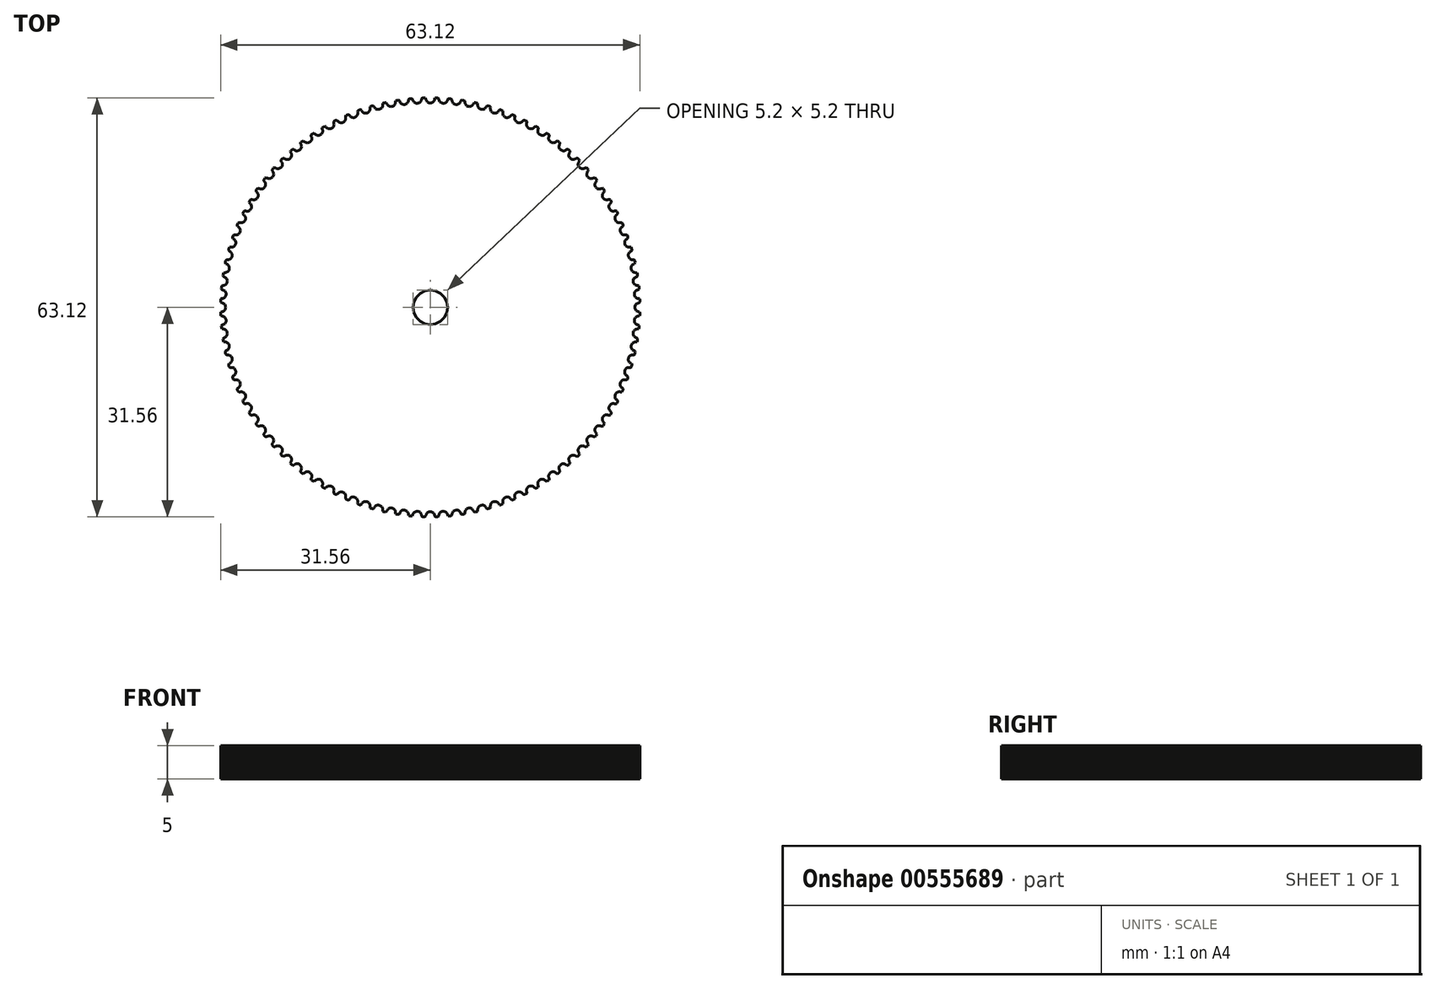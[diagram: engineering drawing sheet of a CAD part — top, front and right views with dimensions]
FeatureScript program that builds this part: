
annotation { "Feature Type Name" : "Feature", "Feature Type Description" : "" }
export const myFeature = defineFeature(function(context is Context, id is Id, definition is map)
    precondition{}
    {
        {
            assignVariable(context, id + "F0", {"name" : "thMat", "anyValue" : 5 * mm});
        }
        {
            var Q0;
            Q0=qCreatedBy(makeId("Top.planeOp"),FACE);
            var sketch = newSketch(context, id + "F1", { "sketchPlane" : qUnion([Q0])});
            skLineSegment(sketch, "E0", {"start": v(1, -31.56) * mm, "end": v(1.14, -31.56) * mm});
            skLineSegment(sketch, "E1", {"start": v(1.14, -31.56) * mm, "end": v(1.25, -31.51) * mm});
            skLineSegment(sketch, "E2", {"start": v(1.25, -31.51) * mm, "end": v(1.3, -31.42) * mm});
            skLineSegment(sketch, "E3", {"start": v(1.3, -31.42) * mm, "end": v(1.31, -31.3) * mm});
            skLineSegment(sketch, "E4", {"start": v(1.31, -31.3) * mm, "end": v(1.34, -31.2) * mm});
            skLineSegment(sketch, "E5", {"start": v(1.34, -31.2) * mm, "end": v(1.38, -31.1) * mm});
            skLineSegment(sketch, "E6", {"start": v(1.38, -31.1) * mm, "end": v(1.44, -31) * mm});
            skLineSegment(sketch, "E7", {"start": v(1.44, -31) * mm, "end": v(1.54, -30.9) * mm});
            skLineSegment(sketch, "E8", {"start": v(1.54, -30.9) * mm, "end": v(1.66, -30.82) * mm});
            skLineSegment(sketch, "E9", {"start": v(1.66, -30.82) * mm, "end": v(1.8, -30.76) * mm});
            skLineSegment(sketch, "E10", {"start": v(1.8, -30.76) * mm, "end": v(1.93, -30.74) * mm});
            skLineSegment(sketch, "E11", {"start": v(1.93, -30.74) * mm, "end": v(2.08, -30.75) * mm});
            skLineSegment(sketch, "E12", {"start": v(2.08, -30.75) * mm, "end": v(2.22, -30.78) * mm});
            skLineSegment(sketch, "E13", {"start": v(2.22, -30.78) * mm, "end": v(2.35, -30.84) * mm});
            skLineSegment(sketch, "E14", {"start": v(2.35, -30.84) * mm, "end": v(2.46, -30.93) * mm});
            skLineSegment(sketch, "E15", {"start": v(2.46, -30.93) * mm, "end": v(2.53, -31.02) * mm});
            skLineSegment(sketch, "E16", {"start": v(2.53, -31.02) * mm, "end": v(2.58, -31.12) * mm});
            skLineSegment(sketch, "E17", {"start": v(2.58, -31.12) * mm, "end": v(2.62, -31.22) * mm});
            skLineSegment(sketch, "E18", {"start": v(2.62, -31.22) * mm, "end": v(2.65, -31.33) * mm});
            skLineSegment(sketch, "E19", {"start": v(2.65, -31.33) * mm, "end": v(2.71, -31.42) * mm});
            skLineSegment(sketch, "E20", {"start": v(2.71, -31.42) * mm, "end": v(2.83, -31.45) * mm});
            skLineSegment(sketch, "E21", {"start": v(2.83, -31.45) * mm, "end": v(2.97, -31.44) * mm});
            skLineSegment(sketch, "E22", {"start": v(2.97, -31.44) * mm, "end": v(3.12, -31.42) * mm});
            skLineSegment(sketch, "E23", {"start": v(3.12, -31.42) * mm, "end": v(3.22, -31.37) * mm});
            skLineSegment(sketch, "E24", {"start": v(3.22, -31.37) * mm, "end": v(3.27, -31.27) * mm});
            skLineSegment(sketch, "E25", {"start": v(3.27, -31.27) * mm, "end": v(3.28, -31.16) * mm});
            skLineSegment(sketch, "E26", {"start": v(3.28, -31.16) * mm, "end": v(3.3, -31.05) * mm});
            skLineSegment(sketch, "E27", {"start": v(3.3, -31.05) * mm, "end": v(3.33, -30.95) * mm});
            skLineSegment(sketch, "E28", {"start": v(3.33, -30.95) * mm, "end": v(3.38, -30.85) * mm});
            skLineSegment(sketch, "E29", {"start": v(3.38, -30.85) * mm, "end": v(3.47, -30.74) * mm});
            skLineSegment(sketch, "E30", {"start": v(3.47, -30.74) * mm, "end": v(3.59, -30.65) * mm});
            skLineSegment(sketch, "E31", {"start": v(3.59, -30.65) * mm, "end": v(3.72, -30.6) * mm});
            skLineSegment(sketch, "E32", {"start": v(3.72, -30.6) * mm, "end": v(3.86, -30.56) * mm});
            skLineSegment(sketch, "E33", {"start": v(3.86, -30.56) * mm, "end": v(4, -30.55) * mm});
            skLineSegment(sketch, "E34", {"start": v(4, -30.55) * mm, "end": v(4.15, -30.58) * mm});
            skLineSegment(sketch, "E35", {"start": v(4.15, -30.58) * mm, "end": v(4.28, -30.63) * mm});
            skLineSegment(sketch, "E36", {"start": v(4.28, -30.63) * mm, "end": v(4.4, -30.72) * mm});
            skLineSegment(sketch, "E37", {"start": v(4.4, -30.72) * mm, "end": v(4.47, -30.8) * mm});
            skLineSegment(sketch, "E38", {"start": v(4.47, -30.8) * mm, "end": v(4.53, -30.9) * mm});
            skLineSegment(sketch, "E39", {"start": v(4.53, -30.9) * mm, "end": v(4.58, -31) * mm});
            skLineSegment(sketch, "E40", {"start": v(4.58, -31) * mm, "end": v(4.61, -31.1) * mm});
            skLineSegment(sketch, "E41", {"start": v(4.61, -31.1) * mm, "end": v(4.68, -31.19) * mm});
            skLineSegment(sketch, "E42", {"start": v(4.68, -31.19) * mm, "end": v(4.8, -31.21) * mm});
            skLineSegment(sketch, "E43", {"start": v(4.8, -31.21) * mm, "end": v(4.94, -31.19) * mm});
            skLineSegment(sketch, "E44", {"start": v(4.94, -31.19) * mm, "end": v(5.08, -31.16) * mm});
            skLineSegment(sketch, "E45", {"start": v(5.08, -31.16) * mm, "end": v(5.19, -31.1) * mm});
            skLineSegment(sketch, "E46", {"start": v(5.19, -31.1) * mm, "end": v(5.22, -31) * mm});
            skLineSegment(sketch, "E47", {"start": v(5.22, -31) * mm, "end": v(5.23, -30.9) * mm});
            skLineSegment(sketch, "E48", {"start": v(5.23, -30.9) * mm, "end": v(5.24, -30.79) * mm});
            skLineSegment(sketch, "E49", {"start": v(5.24, -30.79) * mm, "end": v(5.27, -30.68) * mm});
            skLineSegment(sketch, "E50", {"start": v(5.27, -30.68) * mm, "end": v(5.31, -30.57) * mm});
            skLineSegment(sketch, "E51", {"start": v(5.31, -30.57) * mm, "end": v(5.4, -30.46) * mm});
            skLineSegment(sketch, "E52", {"start": v(5.4, -30.46) * mm, "end": v(5.5, -30.36) * mm});
            skLineSegment(sketch, "E53", {"start": v(5.5, -30.36) * mm, "end": v(5.63, -30.3) * mm});
            skLineSegment(sketch, "E54", {"start": v(5.63, -30.3) * mm, "end": v(5.77, -30.26) * mm});
            skLineSegment(sketch, "E55", {"start": v(5.77, -30.26) * mm, "end": v(5.92, -30.24) * mm});
            skLineSegment(sketch, "E56", {"start": v(5.92, -30.24) * mm, "end": v(6.06, -30.26) * mm});
            skLineSegment(sketch, "E57", {"start": v(6.06, -30.26) * mm, "end": v(6.2, -30.3) * mm});
            skLineSegment(sketch, "E58", {"start": v(6.2, -30.3) * mm, "end": v(6.32, -30.38) * mm});
            skLineSegment(sketch, "E59", {"start": v(6.32, -30.38) * mm, "end": v(6.4, -30.46) * mm});
            skLineSegment(sketch, "E60", {"start": v(6.4, -30.46) * mm, "end": v(6.46, -30.55) * mm});
            skLineSegment(sketch, "E61", {"start": v(6.46, -30.55) * mm, "end": v(6.51, -30.65) * mm});
            skLineSegment(sketch, "E62", {"start": v(6.51, -30.65) * mm, "end": v(6.56, -30.75) * mm});
            skLineSegment(sketch, "E63", {"start": v(6.56, -30.75) * mm, "end": v(6.63, -30.83) * mm});
            skLineSegment(sketch, "E64", {"start": v(6.63, -30.83) * mm, "end": v(6.74, -30.85) * mm});
            skLineSegment(sketch, "E65", {"start": v(6.74, -30.85) * mm, "end": v(6.89, -30.82) * mm});
            skLineSegment(sketch, "E66", {"start": v(6.89, -30.82) * mm, "end": v(7.03, -30.78) * mm});
            skLineSegment(sketch, "E67", {"start": v(7.03, -30.78) * mm, "end": v(7.13, -30.72) * mm});
            skLineSegment(sketch, "E68", {"start": v(7.13, -30.72) * mm, "end": v(7.16, -30.62) * mm});
            skLineSegment(sketch, "E69", {"start": v(7.16, -30.62) * mm, "end": v(7.16, -30.5) * mm});
            skLineSegment(sketch, "E70", {"start": v(7.16, -30.5) * mm, "end": v(7.16, -30.4) * mm});
            skLineSegment(sketch, "E71", {"start": v(7.16, -30.4) * mm, "end": v(7.19, -30.29) * mm});
            skLineSegment(sketch, "E72", {"start": v(7.19, -30.29) * mm, "end": v(7.22, -30.18) * mm});
            skLineSegment(sketch, "E73", {"start": v(7.22, -30.18) * mm, "end": v(7.3, -30.06) * mm});
            skLineSegment(sketch, "E74", {"start": v(7.3, -30.06) * mm, "end": v(7.4, -29.96) * mm});
            skLineSegment(sketch, "E75", {"start": v(7.4, -29.96) * mm, "end": v(7.52, -29.88) * mm});
            skLineSegment(sketch, "E76", {"start": v(7.52, -29.88) * mm, "end": v(7.66, -29.83) * mm});
            skLineSegment(sketch, "E77", {"start": v(7.66, -29.83) * mm, "end": v(7.8, -29.81) * mm});
            skLineSegment(sketch, "E78", {"start": v(7.8, -29.81) * mm, "end": v(7.95, -29.82) * mm});
            skLineSegment(sketch, "E79", {"start": v(7.95, -29.82) * mm, "end": v(8.09, -29.86) * mm});
            skLineSegment(sketch, "E80", {"start": v(8.09, -29.86) * mm, "end": v(8.21, -29.92) * mm});
            skLineSegment(sketch, "E81", {"start": v(8.21, -29.92) * mm, "end": v(8.3, -30) * mm});
            skLineSegment(sketch, "E82", {"start": v(8.3, -30) * mm, "end": v(8.37, -30.09) * mm});
            skLineSegment(sketch, "E83", {"start": v(8.37, -30.09) * mm, "end": v(8.43, -30.18) * mm});
            skLineSegment(sketch, "E84", {"start": v(8.43, -30.18) * mm, "end": v(8.47, -30.28) * mm});
            skLineSegment(sketch, "E85", {"start": v(8.47, -30.28) * mm, "end": v(8.55, -30.36) * mm});
            skLineSegment(sketch, "E86", {"start": v(8.55, -30.36) * mm, "end": v(8.67, -30.36) * mm});
            skLineSegment(sketch, "E87", {"start": v(8.67, -30.36) * mm, "end": v(8.8, -30.32) * mm});
            skLineSegment(sketch, "E88", {"start": v(8.8, -30.32) * mm, "end": v(8.95, -30.28) * mm});
            skLineSegment(sketch, "E89", {"start": v(8.95, -30.28) * mm, "end": v(9.04, -30.21) * mm});
            skLineSegment(sketch, "E90", {"start": v(9.04, -30.21) * mm, "end": v(9.07, -30.1) * mm});
            skLineSegment(sketch, "E91", {"start": v(9.07, -30.1) * mm, "end": v(9.06, -30) * mm});
            skLineSegment(sketch, "E92", {"start": v(9.06, -30) * mm, "end": v(9.06, -29.89) * mm});
            skLineSegment(sketch, "E93", {"start": v(9.06, -29.89) * mm, "end": v(9.07, -29.78) * mm});
            skLineSegment(sketch, "E94", {"start": v(9.07, -29.78) * mm, "end": v(9.1, -29.67) * mm});
            skLineSegment(sketch, "E95", {"start": v(9.1, -29.67) * mm, "end": v(9.17, -29.54) * mm});
            skLineSegment(sketch, "E96", {"start": v(9.17, -29.54) * mm, "end": v(9.27, -29.44) * mm});
            skLineSegment(sketch, "E97", {"start": v(9.27, -29.44) * mm, "end": v(9.39, -29.35) * mm});
            skLineSegment(sketch, "E98", {"start": v(9.39, -29.35) * mm, "end": v(9.52, -29.3) * mm});
            skLineSegment(sketch, "E99", {"start": v(9.52, -29.3) * mm, "end": v(9.66, -29.26) * mm});
            skLineSegment(sketch, "E100", {"start": v(9.66, -29.26) * mm, "end": v(9.8, -29.26) * mm});
            skLineSegment(sketch, "E101", {"start": v(9.8, -29.26) * mm, "end": v(9.94, -29.29) * mm});
            skLineSegment(sketch, "E102", {"start": v(9.94, -29.29) * mm, "end": v(10.07, -29.35) * mm});
            skLineSegment(sketch, "E103", {"start": v(10.07, -29.35) * mm, "end": v(10.16, -29.42) * mm});
            skLineSegment(sketch, "E104", {"start": v(10.16, -29.42) * mm, "end": v(10.24, -29.5) * mm});
            skLineSegment(sketch, "E105", {"start": v(10.24, -29.5) * mm, "end": v(10.3, -29.6) * mm});
            skLineSegment(sketch, "E106", {"start": v(10.3, -29.6) * mm, "end": v(10.36, -29.69) * mm});
            skLineSegment(sketch, "E107", {"start": v(10.36, -29.69) * mm, "end": v(10.44, -29.76) * mm});
            skLineSegment(sketch, "E108", {"start": v(10.44, -29.76) * mm, "end": v(10.56, -29.76) * mm});
            skLineSegment(sketch, "E109", {"start": v(10.56, -29.76) * mm, "end": v(10.7, -29.71) * mm});
            skLineSegment(sketch, "E110", {"start": v(10.7, -29.71) * mm, "end": v(10.83, -29.66) * mm});
            skLineSegment(sketch, "E111", {"start": v(10.83, -29.66) * mm, "end": v(10.92, -29.58) * mm});
            skLineSegment(sketch, "E112", {"start": v(10.92, -29.58) * mm, "end": v(10.94, -29.48) * mm});
            skLineSegment(sketch, "E113", {"start": v(10.94, -29.48) * mm, "end": v(10.92, -29.37) * mm});
            skLineSegment(sketch, "E114", {"start": v(10.92, -29.37) * mm, "end": v(10.92, -29.26) * mm});
            skLineSegment(sketch, "E115", {"start": v(10.92, -29.26) * mm, "end": v(10.92, -29.15) * mm});
            skLineSegment(sketch, "E116", {"start": v(10.92, -29.15) * mm, "end": v(10.95, -29.04) * mm});
            skLineSegment(sketch, "E117", {"start": v(10.95, -29.04) * mm, "end": v(11, -28.9) * mm});
            skLineSegment(sketch, "E118", {"start": v(11, -28.9) * mm, "end": v(11.1, -28.8) * mm});
            skLineSegment(sketch, "E119", {"start": v(11.1, -28.8) * mm, "end": v(11.2, -28.7) * mm});
            skLineSegment(sketch, "E120", {"start": v(11.2, -28.7) * mm, "end": v(11.34, -28.64) * mm});
            skLineSegment(sketch, "E121", {"start": v(11.34, -28.64) * mm, "end": v(11.48, -28.6) * mm});
            skLineSegment(sketch, "E122", {"start": v(11.48, -28.6) * mm, "end": v(11.62, -28.59) * mm});
            skLineSegment(sketch, "E123", {"start": v(11.62, -28.59) * mm, "end": v(11.76, -28.6) * mm});
            skLineSegment(sketch, "E124", {"start": v(11.76, -28.6) * mm, "end": v(11.9, -28.66) * mm});
            skLineSegment(sketch, "E125", {"start": v(11.9, -28.66) * mm, "end": v(11.99, -28.73) * mm});
            skLineSegment(sketch, "E126", {"start": v(11.99, -28.73) * mm, "end": v(12.07, -28.8) * mm});
            skLineSegment(sketch, "E127", {"start": v(12.07, -28.8) * mm, "end": v(12.14, -28.89) * mm});
            skLineSegment(sketch, "E128", {"start": v(12.14, -28.89) * mm, "end": v(12.2, -28.98) * mm});
            skLineSegment(sketch, "E129", {"start": v(12.2, -28.98) * mm, "end": v(12.29, -29.04) * mm});
            skLineSegment(sketch, "E130", {"start": v(12.29, -29.04) * mm, "end": v(12.4, -29.04) * mm});
            skLineSegment(sketch, "E131", {"start": v(12.4, -29.04) * mm, "end": v(12.54, -28.98) * mm});
            skLineSegment(sketch, "E132", {"start": v(12.54, -28.98) * mm, "end": v(12.68, -28.92) * mm});
            skLineSegment(sketch, "E133", {"start": v(12.68, -28.92) * mm, "end": v(12.76, -28.84) * mm});
            skLineSegment(sketch, "E134", {"start": v(12.76, -28.84) * mm, "end": v(12.77, -28.73) * mm});
            skLineSegment(sketch, "E135", {"start": v(12.77, -28.73) * mm, "end": v(12.74, -28.62) * mm});
            skLineSegment(sketch, "E136", {"start": v(12.74, -28.62) * mm, "end": v(12.73, -28.52) * mm});
            skLineSegment(sketch, "E137", {"start": v(12.73, -28.52) * mm, "end": v(12.73, -28.4) * mm});
            skLineSegment(sketch, "E138", {"start": v(12.73, -28.4) * mm, "end": v(12.75, -28.3) * mm});
            skLineSegment(sketch, "E139", {"start": v(12.75, -28.3) * mm, "end": v(12.8, -28.16) * mm});
            skLineSegment(sketch, "E140", {"start": v(12.8, -28.16) * mm, "end": v(12.88, -28.04) * mm});
            skLineSegment(sketch, "E141", {"start": v(12.88, -28.04) * mm, "end": v(13, -27.94) * mm});
            skLineSegment(sketch, "E142", {"start": v(13, -27.94) * mm, "end": v(13.11, -27.87) * mm});
            skLineSegment(sketch, "E143", {"start": v(13.11, -27.87) * mm, "end": v(13.25, -27.82) * mm});
            skLineSegment(sketch, "E144", {"start": v(13.25, -27.82) * mm, "end": v(13.4, -27.8) * mm});
            skLineSegment(sketch, "E145", {"start": v(13.4, -27.8) * mm, "end": v(13.54, -27.81) * mm});
            skLineSegment(sketch, "E146", {"start": v(13.54, -27.81) * mm, "end": v(13.67, -27.86) * mm});
            skLineSegment(sketch, "E147", {"start": v(13.67, -27.86) * mm, "end": v(13.77, -27.92) * mm});
            skLineSegment(sketch, "E148", {"start": v(13.77, -27.92) * mm, "end": v(13.86, -27.99) * mm});
            skLineSegment(sketch, "E149", {"start": v(13.86, -27.99) * mm, "end": v(13.93, -28.07) * mm});
            skLineSegment(sketch, "E150", {"start": v(13.93, -28.07) * mm, "end": v(14, -28.15) * mm});
            skLineSegment(sketch, "E151", {"start": v(14, -28.15) * mm, "end": v(14.09, -28.21) * mm});
            skLineSegment(sketch, "E152", {"start": v(14.09, -28.21) * mm, "end": v(14.2, -28.2) * mm});
            skLineSegment(sketch, "E153", {"start": v(14.2, -28.2) * mm, "end": v(14.34, -28.14) * mm});
            skLineSegment(sketch, "E154", {"start": v(14.34, -28.14) * mm, "end": v(14.47, -28.07) * mm});
            skLineSegment(sketch, "E155", {"start": v(14.47, -28.07) * mm, "end": v(14.55, -27.98) * mm});
            skLineSegment(sketch, "E156", {"start": v(14.55, -27.98) * mm, "end": v(14.55, -27.87) * mm});
            skLineSegment(sketch, "E157", {"start": v(14.55, -27.87) * mm, "end": v(14.52, -27.77) * mm});
            skLineSegment(sketch, "E158", {"start": v(14.52, -27.77) * mm, "end": v(14.5, -27.66) * mm});
            skLineSegment(sketch, "E159", {"start": v(14.5, -27.66) * mm, "end": v(14.5, -27.55) * mm});
            skLineSegment(sketch, "E160", {"start": v(14.5, -27.55) * mm, "end": v(14.5, -27.43) * mm});
            skLineSegment(sketch, "E161", {"start": v(14.5, -27.43) * mm, "end": v(14.54, -27.3) * mm});
            skLineSegment(sketch, "E162", {"start": v(14.54, -27.3) * mm, "end": v(14.62, -27.18) * mm});
            skLineSegment(sketch, "E163", {"start": v(14.62, -27.18) * mm, "end": v(14.72, -27.07) * mm});
            skLineSegment(sketch, "E164", {"start": v(14.72, -27.07) * mm, "end": v(14.84, -27) * mm});
            skLineSegment(sketch, "E165", {"start": v(14.84, -27) * mm, "end": v(14.97, -26.93) * mm});
            skLineSegment(sketch, "E166", {"start": v(14.97, -26.93) * mm, "end": v(15.11, -26.9) * mm});
            skLineSegment(sketch, "E167", {"start": v(15.11, -26.9) * mm, "end": v(15.26, -26.9) * mm});
            skLineSegment(sketch, "E168", {"start": v(15.26, -26.9) * mm, "end": v(15.4, -26.94) * mm});
            skLineSegment(sketch, "E169", {"start": v(15.4, -26.94) * mm, "end": v(15.5, -27) * mm});
            skLineSegment(sketch, "E170", {"start": v(15.5, -27) * mm, "end": v(15.59, -27.06) * mm});
            skLineSegment(sketch, "E171", {"start": v(15.59, -27.06) * mm, "end": v(15.67, -27.14) * mm});
            skLineSegment(sketch, "E172", {"start": v(15.67, -27.14) * mm, "end": v(15.74, -27.22) * mm});
            skLineSegment(sketch, "E173", {"start": v(15.74, -27.22) * mm, "end": v(15.83, -27.27) * mm});
            skLineSegment(sketch, "E174", {"start": v(15.83, -27.27) * mm, "end": v(15.95, -27.25) * mm});
            skLineSegment(sketch, "E175", {"start": v(15.95, -27.25) * mm, "end": v(16.07, -27.18) * mm});
            skLineSegment(sketch, "E176", {"start": v(16.07, -27.18) * mm, "end": v(16.2, -27.1) * mm});
            skLineSegment(sketch, "E177", {"start": v(16.2, -27.1) * mm, "end": v(16.27, -27.01) * mm});
            skLineSegment(sketch, "E178", {"start": v(16.27, -27.01) * mm, "end": v(16.27, -26.9) * mm});
            skLineSegment(sketch, "E179", {"start": v(16.27, -26.9) * mm, "end": v(16.23, -26.8) * mm});
            skLineSegment(sketch, "E180", {"start": v(16.23, -26.8) * mm, "end": v(16.2, -26.7) * mm});
            skLineSegment(sketch, "E181", {"start": v(16.2, -26.7) * mm, "end": v(16.2, -26.58) * mm});
            skLineSegment(sketch, "E182", {"start": v(16.2, -26.58) * mm, "end": v(16.2, -26.47) * mm});
            skLineSegment(sketch, "E183", {"start": v(16.2, -26.47) * mm, "end": v(16.23, -26.33) * mm});
            skLineSegment(sketch, "E184", {"start": v(16.23, -26.33) * mm, "end": v(16.3, -26.2) * mm});
            skLineSegment(sketch, "E185", {"start": v(16.3, -26.2) * mm, "end": v(16.4, -26.1) * mm});
            skLineSegment(sketch, "E186", {"start": v(16.4, -26.1) * mm, "end": v(16.5, -26) * mm});
            skLineSegment(sketch, "E187", {"start": v(16.5, -26) * mm, "end": v(16.63, -25.94) * mm});
            skLineSegment(sketch, "E188", {"start": v(16.63, -25.94) * mm, "end": v(16.77, -25.9) * mm});
            skLineSegment(sketch, "E189", {"start": v(16.77, -25.9) * mm, "end": v(16.92, -25.9) * mm});
            skLineSegment(sketch, "E190", {"start": v(16.92, -25.9) * mm, "end": v(17.06, -25.92) * mm});
            skLineSegment(sketch, "E191", {"start": v(17.06, -25.92) * mm, "end": v(17.16, -25.97) * mm});
            skLineSegment(sketch, "E192", {"start": v(17.16, -25.97) * mm, "end": v(17.25, -26.03) * mm});
            skLineSegment(sketch, "E193", {"start": v(17.25, -26.03) * mm, "end": v(17.34, -26.1) * mm});
            skLineSegment(sketch, "E194", {"start": v(17.34, -26.1) * mm, "end": v(17.42, -26.18) * mm});
            skLineSegment(sketch, "E195", {"start": v(17.42, -26.18) * mm, "end": v(17.51, -26.23) * mm});
            skLineSegment(sketch, "E196", {"start": v(17.51, -26.23) * mm, "end": v(17.63, -26.2) * mm});
            skLineSegment(sketch, "E197", {"start": v(17.63, -26.2) * mm, "end": v(17.75, -26.12) * mm});
            skLineSegment(sketch, "E198", {"start": v(17.75, -26.12) * mm, "end": v(17.87, -26.03) * mm});
            skLineSegment(sketch, "E199", {"start": v(17.87, -26.03) * mm, "end": v(17.94, -25.94) * mm});
            skLineSegment(sketch, "E200", {"start": v(17.94, -25.94) * mm, "end": v(17.93, -25.83) * mm});
            skLineSegment(sketch, "E201", {"start": v(17.93, -25.83) * mm, "end": v(17.88, -25.73) * mm});
            skLineSegment(sketch, "E202", {"start": v(17.88, -25.73) * mm, "end": v(17.85, -25.62) * mm});
            skLineSegment(sketch, "E203", {"start": v(17.85, -25.62) * mm, "end": v(17.83, -25.51) * mm});
            skLineSegment(sketch, "E204", {"start": v(17.83, -25.51) * mm, "end": v(17.82, -25.4) * mm});
            skLineSegment(sketch, "E205", {"start": v(17.82, -25.4) * mm, "end": v(17.85, -25.26) * mm});
            skLineSegment(sketch, "E206", {"start": v(17.85, -25.26) * mm, "end": v(17.91, -25.13) * mm});
            skLineSegment(sketch, "E207", {"start": v(17.91, -25.13) * mm, "end": v(18, -25.02) * mm});
            skLineSegment(sketch, "E208", {"start": v(18, -25.02) * mm, "end": v(18.1, -24.92) * mm});
            skLineSegment(sketch, "E209", {"start": v(18.1, -24.92) * mm, "end": v(18.23, -24.85) * mm});
            skLineSegment(sketch, "E210", {"start": v(18.23, -24.85) * mm, "end": v(18.37, -24.8) * mm});
            skLineSegment(sketch, "E211", {"start": v(18.37, -24.8) * mm, "end": v(18.5, -24.78) * mm});
            skLineSegment(sketch, "E212", {"start": v(18.5, -24.78) * mm, "end": v(18.65, -24.8) * mm});
            skLineSegment(sketch, "E213", {"start": v(18.65, -24.8) * mm, "end": v(18.76, -24.84) * mm});
            skLineSegment(sketch, "E214", {"start": v(18.76, -24.84) * mm, "end": v(18.85, -24.9) * mm});
            skLineSegment(sketch, "E215", {"start": v(18.85, -24.9) * mm, "end": v(18.94, -24.96) * mm});
            skLineSegment(sketch, "E216", {"start": v(18.94, -24.96) * mm, "end": v(19.03, -25.03) * mm});
            skLineSegment(sketch, "E217", {"start": v(19.03, -25.03) * mm, "end": v(19.13, -25.08) * mm});
            skLineSegment(sketch, "E218", {"start": v(19.13, -25.08) * mm, "end": v(19.24, -25.04) * mm});
            skLineSegment(sketch, "E219", {"start": v(19.24, -25.04) * mm, "end": v(19.35, -24.95) * mm});
            skLineSegment(sketch, "E220", {"start": v(19.35, -24.95) * mm, "end": v(19.47, -24.86) * mm});
            skLineSegment(sketch, "E221", {"start": v(19.47, -24.86) * mm, "end": v(19.53, -24.76) * mm});
            skLineSegment(sketch, "E222", {"start": v(19.53, -24.76) * mm, "end": v(19.51, -24.65) * mm});
            skLineSegment(sketch, "E223", {"start": v(19.51, -24.65) * mm, "end": v(19.46, -24.56) * mm});
            skLineSegment(sketch, "E224", {"start": v(19.46, -24.56) * mm, "end": v(19.42, -24.45) * mm});
            skLineSegment(sketch, "E225", {"start": v(19.42, -24.45) * mm, "end": v(19.4, -24.34) * mm});
            skLineSegment(sketch, "E226", {"start": v(19.4, -24.34) * mm, "end": v(19.38, -24.23) * mm});
            skLineSegment(sketch, "E227", {"start": v(19.38, -24.23) * mm, "end": v(19.4, -24.09) * mm});
            skLineSegment(sketch, "E228", {"start": v(19.4, -24.09) * mm, "end": v(19.45, -23.96) * mm});
            skLineSegment(sketch, "E229", {"start": v(19.45, -23.96) * mm, "end": v(19.53, -23.84) * mm});
            skLineSegment(sketch, "E230", {"start": v(19.53, -23.84) * mm, "end": v(19.63, -23.73) * mm});
            skLineSegment(sketch, "E231", {"start": v(19.63, -23.73) * mm, "end": v(19.75, -23.65) * mm});
            skLineSegment(sketch, "E232", {"start": v(19.75, -23.65) * mm, "end": v(19.89, -23.6) * mm});
            skLineSegment(sketch, "E233", {"start": v(19.89, -23.6) * mm, "end": v(20.03, -23.57) * mm});
            skLineSegment(sketch, "E234", {"start": v(20.03, -23.57) * mm, "end": v(20.17, -23.58) * mm});
            skLineSegment(sketch, "E235", {"start": v(20.17, -23.58) * mm, "end": v(20.28, -23.62) * mm});
            skLineSegment(sketch, "E236", {"start": v(20.28, -23.62) * mm, "end": v(20.38, -23.66) * mm});
            skLineSegment(sketch, "E237", {"start": v(20.38, -23.66) * mm, "end": v(20.47, -23.72) * mm});
            skLineSegment(sketch, "E238", {"start": v(20.47, -23.72) * mm, "end": v(20.56, -23.79) * mm});
            skLineSegment(sketch, "E239", {"start": v(20.56, -23.79) * mm, "end": v(20.66, -23.82) * mm});
            skLineSegment(sketch, "E240", {"start": v(20.66, -23.82) * mm, "end": v(20.77, -23.78) * mm});
            skLineSegment(sketch, "E241", {"start": v(20.77, -23.78) * mm, "end": v(20.88, -23.69) * mm});
            skLineSegment(sketch, "E242", {"start": v(20.88, -23.69) * mm, "end": v(21, -23.59) * mm});
            skLineSegment(sketch, "E243", {"start": v(21, -23.59) * mm, "end": v(21.05, -23.49) * mm});
            skLineSegment(sketch, "E244", {"start": v(21.05, -23.49) * mm, "end": v(21.02, -23.38) * mm});
            skLineSegment(sketch, "E245", {"start": v(21.02, -23.38) * mm, "end": v(20.97, -23.29) * mm});
            skLineSegment(sketch, "E246", {"start": v(20.97, -23.29) * mm, "end": v(20.92, -23.19) * mm});
            skLineSegment(sketch, "E247", {"start": v(20.92, -23.19) * mm, "end": v(20.89, -23.08) * mm});
            skLineSegment(sketch, "E248", {"start": v(20.89, -23.08) * mm, "end": v(20.87, -22.97) * mm});
            skLineSegment(sketch, "E249", {"start": v(20.87, -22.97) * mm, "end": v(20.88, -22.82) * mm});
            skLineSegment(sketch, "E250", {"start": v(20.88, -22.82) * mm, "end": v(20.92, -22.69) * mm});
            skLineSegment(sketch, "E251", {"start": v(20.92, -22.69) * mm, "end": v(20.99, -22.56) * mm});
            skLineSegment(sketch, "E252", {"start": v(20.99, -22.56) * mm, "end": v(21.08, -22.45) * mm});
            skLineSegment(sketch, "E253", {"start": v(21.08, -22.45) * mm, "end": v(21.2, -22.36) * mm});
            skLineSegment(sketch, "E254", {"start": v(21.2, -22.36) * mm, "end": v(21.33, -22.3) * mm});
            skLineSegment(sketch, "E255", {"start": v(21.33, -22.3) * mm, "end": v(21.47, -22.27) * mm});
            skLineSegment(sketch, "E256", {"start": v(21.47, -22.27) * mm, "end": v(21.61, -22.27) * mm});
            skLineSegment(sketch, "E257", {"start": v(21.61, -22.27) * mm, "end": v(21.72, -22.3) * mm});
            skLineSegment(sketch, "E258", {"start": v(21.72, -22.3) * mm, "end": v(21.83, -22.34) * mm});
            skLineSegment(sketch, "E259", {"start": v(21.83, -22.34) * mm, "end": v(21.92, -22.39) * mm});
            skLineSegment(sketch, "E260", {"start": v(21.92, -22.39) * mm, "end": v(22.01, -22.45) * mm});
            skLineSegment(sketch, "E261", {"start": v(22.01, -22.45) * mm, "end": v(22.12, -22.48) * mm});
            skLineSegment(sketch, "E262", {"start": v(22.12, -22.48) * mm, "end": v(22.22, -22.43) * mm});
            skLineSegment(sketch, "E263", {"start": v(22.22, -22.43) * mm, "end": v(22.33, -22.33) * mm});
            skLineSegment(sketch, "E264", {"start": v(22.33, -22.33) * mm, "end": v(22.43, -22.22) * mm});
            skLineSegment(sketch, "E265", {"start": v(22.43, -22.22) * mm, "end": v(22.48, -22.12) * mm});
            skLineSegment(sketch, "E266", {"start": v(22.48, -22.12) * mm, "end": v(22.45, -22.01) * mm});
            skLineSegment(sketch, "E267", {"start": v(22.45, -22.01) * mm, "end": v(22.39, -21.92) * mm});
            skLineSegment(sketch, "E268", {"start": v(22.39, -21.92) * mm, "end": v(22.34, -21.83) * mm});
            skLineSegment(sketch, "E269", {"start": v(22.34, -21.83) * mm, "end": v(22.3, -21.72) * mm});
            skLineSegment(sketch, "E270", {"start": v(22.3, -21.72) * mm, "end": v(22.27, -21.61) * mm});
            skLineSegment(sketch, "E271", {"start": v(22.27, -21.61) * mm, "end": v(22.27, -21.47) * mm});
            skLineSegment(sketch, "E272", {"start": v(22.27, -21.47) * mm, "end": v(22.3, -21.33) * mm});
            skLineSegment(sketch, "E273", {"start": v(22.3, -21.33) * mm, "end": v(22.36, -21.2) * mm});
            skLineSegment(sketch, "E274", {"start": v(22.36, -21.2) * mm, "end": v(22.45, -21.08) * mm});
            skLineSegment(sketch, "E275", {"start": v(22.45, -21.08) * mm, "end": v(22.56, -20.99) * mm});
            skLineSegment(sketch, "E276", {"start": v(22.56, -20.99) * mm, "end": v(22.69, -20.92) * mm});
            skLineSegment(sketch, "E277", {"start": v(22.69, -20.92) * mm, "end": v(22.82, -20.88) * mm});
            skLineSegment(sketch, "E278", {"start": v(22.82, -20.88) * mm, "end": v(22.97, -20.87) * mm});
            skLineSegment(sketch, "E279", {"start": v(22.97, -20.87) * mm, "end": v(23.08, -20.89) * mm});
            skLineSegment(sketch, "E280", {"start": v(23.08, -20.89) * mm, "end": v(23.19, -20.92) * mm});
            skLineSegment(sketch, "E281", {"start": v(23.19, -20.92) * mm, "end": v(23.29, -20.97) * mm});
            skLineSegment(sketch, "E282", {"start": v(23.29, -20.97) * mm, "end": v(23.38, -21.02) * mm});
            skLineSegment(sketch, "E283", {"start": v(23.38, -21.02) * mm, "end": v(23.49, -21.05) * mm});
            skLineSegment(sketch, "E284", {"start": v(23.49, -21.05) * mm, "end": v(23.59, -21) * mm});
            skLineSegment(sketch, "E285", {"start": v(23.59, -21) * mm, "end": v(23.69, -20.88) * mm});
            skLineSegment(sketch, "E286", {"start": v(23.69, -20.88) * mm, "end": v(23.78, -20.77) * mm});
            skLineSegment(sketch, "E287", {"start": v(23.78, -20.77) * mm, "end": v(23.82, -20.66) * mm});
            skLineSegment(sketch, "E288", {"start": v(23.82, -20.66) * mm, "end": v(23.79, -20.56) * mm});
            skLineSegment(sketch, "E289", {"start": v(23.79, -20.56) * mm, "end": v(23.72, -20.47) * mm});
            skLineSegment(sketch, "E290", {"start": v(23.72, -20.47) * mm, "end": v(23.66, -20.38) * mm});
            skLineSegment(sketch, "E291", {"start": v(23.66, -20.38) * mm, "end": v(23.62, -20.28) * mm});
            skLineSegment(sketch, "E292", {"start": v(23.62, -20.28) * mm, "end": v(23.58, -20.17) * mm});
            skLineSegment(sketch, "E293", {"start": v(23.58, -20.17) * mm, "end": v(23.57, -20.03) * mm});
            skLineSegment(sketch, "E294", {"start": v(23.57, -20.03) * mm, "end": v(23.6, -19.89) * mm});
            skLineSegment(sketch, "E295", {"start": v(23.6, -19.89) * mm, "end": v(23.65, -19.75) * mm});
            skLineSegment(sketch, "E296", {"start": v(23.65, -19.75) * mm, "end": v(23.73, -19.63) * mm});
            skLineSegment(sketch, "E297", {"start": v(23.73, -19.63) * mm, "end": v(23.84, -19.53) * mm});
            skLineSegment(sketch, "E298", {"start": v(23.84, -19.53) * mm, "end": v(23.96, -19.45) * mm});
            skLineSegment(sketch, "E299", {"start": v(23.96, -19.45) * mm, "end": v(24.09, -19.4) * mm});
            skLineSegment(sketch, "E300", {"start": v(24.09, -19.4) * mm, "end": v(24.23, -19.38) * mm});
            skLineSegment(sketch, "E301", {"start": v(24.23, -19.38) * mm, "end": v(24.34, -19.4) * mm});
            skLineSegment(sketch, "E302", {"start": v(24.34, -19.4) * mm, "end": v(24.45, -19.42) * mm});
            skLineSegment(sketch, "E303", {"start": v(24.45, -19.42) * mm, "end": v(24.56, -19.46) * mm});
            skLineSegment(sketch, "E304", {"start": v(24.56, -19.46) * mm, "end": v(24.65, -19.51) * mm});
            skLineSegment(sketch, "E305", {"start": v(24.65, -19.51) * mm, "end": v(24.76, -19.53) * mm});
            skLineSegment(sketch, "E306", {"start": v(24.76, -19.53) * mm, "end": v(24.86, -19.47) * mm});
            skLineSegment(sketch, "E307", {"start": v(24.86, -19.47) * mm, "end": v(24.95, -19.35) * mm});
            skLineSegment(sketch, "E308", {"start": v(24.95, -19.35) * mm, "end": v(25.04, -19.24) * mm});
            skLineSegment(sketch, "E309", {"start": v(25.04, -19.24) * mm, "end": v(25.08, -19.13) * mm});
            skLineSegment(sketch, "E310", {"start": v(25.08, -19.13) * mm, "end": v(25.03, -19.03) * mm});
            skLineSegment(sketch, "E311", {"start": v(25.03, -19.03) * mm, "end": v(24.96, -18.94) * mm});
            skLineSegment(sketch, "E312", {"start": v(24.96, -18.94) * mm, "end": v(24.9, -18.85) * mm});
            skLineSegment(sketch, "E313", {"start": v(24.9, -18.85) * mm, "end": v(24.84, -18.76) * mm});
            skLineSegment(sketch, "E314", {"start": v(24.84, -18.76) * mm, "end": v(24.8, -18.65) * mm});
            skLineSegment(sketch, "E315", {"start": v(24.8, -18.65) * mm, "end": v(24.78, -18.5) * mm});
            skLineSegment(sketch, "E316", {"start": v(24.78, -18.5) * mm, "end": v(24.8, -18.37) * mm});
            skLineSegment(sketch, "E317", {"start": v(24.8, -18.37) * mm, "end": v(24.85, -18.23) * mm});
            skLineSegment(sketch, "E318", {"start": v(24.85, -18.23) * mm, "end": v(24.92, -18.1) * mm});
            skLineSegment(sketch, "E319", {"start": v(24.92, -18.1) * mm, "end": v(25.02, -18) * mm});
            skLineSegment(sketch, "E320", {"start": v(25.02, -18) * mm, "end": v(25.13, -17.91) * mm});
            skLineSegment(sketch, "E321", {"start": v(25.13, -17.91) * mm, "end": v(25.26, -17.85) * mm});
            skLineSegment(sketch, "E322", {"start": v(25.26, -17.85) * mm, "end": v(25.4, -17.82) * mm});
            skLineSegment(sketch, "E323", {"start": v(25.4, -17.82) * mm, "end": v(25.51, -17.83) * mm});
            skLineSegment(sketch, "E324", {"start": v(25.51, -17.83) * mm, "end": v(25.62, -17.85) * mm});
            skLineSegment(sketch, "E325", {"start": v(25.62, -17.85) * mm, "end": v(25.73, -17.88) * mm});
            skLineSegment(sketch, "E326", {"start": v(25.73, -17.88) * mm, "end": v(25.83, -17.93) * mm});
            skLineSegment(sketch, "E327", {"start": v(25.83, -17.93) * mm, "end": v(25.94, -17.94) * mm});
            skLineSegment(sketch, "E328", {"start": v(25.94, -17.94) * mm, "end": v(26.03, -17.87) * mm});
            skLineSegment(sketch, "E329", {"start": v(26.03, -17.87) * mm, "end": v(26.12, -17.75) * mm});
            skLineSegment(sketch, "E330", {"start": v(26.12, -17.75) * mm, "end": v(26.2, -17.63) * mm});
            skLineSegment(sketch, "E331", {"start": v(26.2, -17.63) * mm, "end": v(26.23, -17.51) * mm});
            skLineSegment(sketch, "E332", {"start": v(26.23, -17.51) * mm, "end": v(26.18, -17.42) * mm});
            skLineSegment(sketch, "E333", {"start": v(26.18, -17.42) * mm, "end": v(26.1, -17.34) * mm});
            skLineSegment(sketch, "E334", {"start": v(26.1, -17.34) * mm, "end": v(26.03, -17.25) * mm});
            skLineSegment(sketch, "E335", {"start": v(26.03, -17.25) * mm, "end": v(25.97, -17.16) * mm});
            skLineSegment(sketch, "E336", {"start": v(25.97, -17.16) * mm, "end": v(25.92, -17.06) * mm});
            skLineSegment(sketch, "E337", {"start": v(25.92, -17.06) * mm, "end": v(25.9, -16.92) * mm});
            skLineSegment(sketch, "E338", {"start": v(25.9, -16.92) * mm, "end": v(25.9, -16.77) * mm});
            skLineSegment(sketch, "E339", {"start": v(25.9, -16.77) * mm, "end": v(25.94, -16.63) * mm});
            skLineSegment(sketch, "E340", {"start": v(25.94, -16.63) * mm, "end": v(26, -16.5) * mm});
            skLineSegment(sketch, "E341", {"start": v(26, -16.5) * mm, "end": v(26.1, -16.4) * mm});
            skLineSegment(sketch, "E342", {"start": v(26.1, -16.4) * mm, "end": v(26.2, -16.3) * mm});
            skLineSegment(sketch, "E343", {"start": v(26.2, -16.3) * mm, "end": v(26.33, -16.23) * mm});
            skLineSegment(sketch, "E344", {"start": v(26.33, -16.23) * mm, "end": v(26.47, -16.2) * mm});
            skLineSegment(sketch, "E345", {"start": v(26.47, -16.2) * mm, "end": v(26.58, -16.2) * mm});
            skLineSegment(sketch, "E346", {"start": v(26.58, -16.2) * mm, "end": v(26.7, -16.2) * mm});
            skLineSegment(sketch, "E347", {"start": v(26.7, -16.2) * mm, "end": v(26.8, -16.23) * mm});
            skLineSegment(sketch, "E348", {"start": v(26.8, -16.23) * mm, "end": v(26.9, -16.27) * mm});
            skLineSegment(sketch, "E349", {"start": v(26.9, -16.27) * mm, "end": v(27.01, -16.27) * mm});
            skLineSegment(sketch, "E350", {"start": v(27.01, -16.27) * mm, "end": v(27.1, -16.2) * mm});
            skLineSegment(sketch, "E351", {"start": v(27.1, -16.2) * mm, "end": v(27.18, -16.07) * mm});
            skLineSegment(sketch, "E352", {"start": v(27.18, -16.07) * mm, "end": v(27.25, -15.95) * mm});
            skLineSegment(sketch, "E353", {"start": v(27.25, -15.95) * mm, "end": v(27.27, -15.83) * mm});
            skLineSegment(sketch, "E354", {"start": v(27.27, -15.83) * mm, "end": v(27.22, -15.74) * mm});
            skLineSegment(sketch, "E355", {"start": v(27.22, -15.74) * mm, "end": v(27.14, -15.67) * mm});
            skLineSegment(sketch, "E356", {"start": v(27.14, -15.67) * mm, "end": v(27.06, -15.59) * mm});
            skLineSegment(sketch, "E357", {"start": v(27.06, -15.59) * mm, "end": v(27, -15.5) * mm});
            skLineSegment(sketch, "E358", {"start": v(27, -15.5) * mm, "end": v(26.94, -15.4) * mm});
            skLineSegment(sketch, "E359", {"start": v(26.94, -15.4) * mm, "end": v(26.9, -15.26) * mm});
            skLineSegment(sketch, "E360", {"start": v(26.9, -15.26) * mm, "end": v(26.9, -15.11) * mm});
            skLineSegment(sketch, "E361", {"start": v(26.9, -15.11) * mm, "end": v(26.93, -14.97) * mm});
            skLineSegment(sketch, "E362", {"start": v(26.93, -14.97) * mm, "end": v(27, -14.84) * mm});
            skLineSegment(sketch, "E363", {"start": v(27, -14.84) * mm, "end": v(27.07, -14.72) * mm});
            skLineSegment(sketch, "E364", {"start": v(27.07, -14.72) * mm, "end": v(27.18, -14.62) * mm});
            skLineSegment(sketch, "E365", {"start": v(27.18, -14.62) * mm, "end": v(27.3, -14.54) * mm});
            skLineSegment(sketch, "E366", {"start": v(27.3, -14.54) * mm, "end": v(27.43, -14.5) * mm});
            skLineSegment(sketch, "E367", {"start": v(27.43, -14.5) * mm, "end": v(27.55, -14.5) * mm});
            skLineSegment(sketch, "E368", {"start": v(27.55, -14.5) * mm, "end": v(27.66, -14.5) * mm});
            skLineSegment(sketch, "E369", {"start": v(27.66, -14.5) * mm, "end": v(27.77, -14.52) * mm});
            skLineSegment(sketch, "E370", {"start": v(27.77, -14.52) * mm, "end": v(27.87, -14.55) * mm});
            skLineSegment(sketch, "E371", {"start": v(27.87, -14.55) * mm, "end": v(27.98, -14.55) * mm});
            skLineSegment(sketch, "E372", {"start": v(27.98, -14.55) * mm, "end": v(28.07, -14.47) * mm});
            skLineSegment(sketch, "E373", {"start": v(28.07, -14.47) * mm, "end": v(28.14, -14.34) * mm});
            skLineSegment(sketch, "E374", {"start": v(28.14, -14.34) * mm, "end": v(28.2, -14.2) * mm});
            skLineSegment(sketch, "E375", {"start": v(28.2, -14.2) * mm, "end": v(28.21, -14.09) * mm});
            skLineSegment(sketch, "E376", {"start": v(28.21, -14.09) * mm, "end": v(28.15, -14) * mm});
            skLineSegment(sketch, "E377", {"start": v(28.15, -14) * mm, "end": v(28.07, -13.93) * mm});
            skLineSegment(sketch, "E378", {"start": v(28.07, -13.93) * mm, "end": v(27.99, -13.86) * mm});
            skLineSegment(sketch, "E379", {"start": v(27.99, -13.86) * mm, "end": v(27.92, -13.77) * mm});
            skLineSegment(sketch, "E380", {"start": v(27.92, -13.77) * mm, "end": v(27.86, -13.67) * mm});
            skLineSegment(sketch, "E381", {"start": v(27.86, -13.67) * mm, "end": v(27.81, -13.54) * mm});
            skLineSegment(sketch, "E382", {"start": v(27.81, -13.54) * mm, "end": v(27.8, -13.4) * mm});
            skLineSegment(sketch, "E383", {"start": v(27.8, -13.4) * mm, "end": v(27.82, -13.25) * mm});
            skLineSegment(sketch, "E384", {"start": v(27.82, -13.25) * mm, "end": v(27.87, -13.11) * mm});
            skLineSegment(sketch, "E385", {"start": v(27.87, -13.11) * mm, "end": v(27.94, -13) * mm});
            skLineSegment(sketch, "E386", {"start": v(27.94, -13) * mm, "end": v(28.04, -12.88) * mm});
            skLineSegment(sketch, "E387", {"start": v(28.04, -12.88) * mm, "end": v(28.16, -12.8) * mm});
            skLineSegment(sketch, "E388", {"start": v(28.16, -12.8) * mm, "end": v(28.3, -12.75) * mm});
            skLineSegment(sketch, "E389", {"start": v(28.3, -12.75) * mm, "end": v(28.4, -12.73) * mm});
            skLineSegment(sketch, "E390", {"start": v(28.4, -12.73) * mm, "end": v(28.52, -12.73) * mm});
            skLineSegment(sketch, "E391", {"start": v(28.52, -12.73) * mm, "end": v(28.62, -12.74) * mm});
            skLineSegment(sketch, "E392", {"start": v(28.62, -12.74) * mm, "end": v(28.73, -12.77) * mm});
            skLineSegment(sketch, "E393", {"start": v(28.73, -12.77) * mm, "end": v(28.84, -12.76) * mm});
            skLineSegment(sketch, "E394", {"start": v(28.84, -12.76) * mm, "end": v(28.92, -12.68) * mm});
            skLineSegment(sketch, "E395", {"start": v(28.92, -12.68) * mm, "end": v(28.98, -12.54) * mm});
            skLineSegment(sketch, "E396", {"start": v(28.98, -12.54) * mm, "end": v(29.04, -12.4) * mm});
            skLineSegment(sketch, "E397", {"start": v(29.04, -12.4) * mm, "end": v(29.04, -12.29) * mm});
            skLineSegment(sketch, "E398", {"start": v(29.04, -12.29) * mm, "end": v(28.98, -12.2) * mm});
            skLineSegment(sketch, "E399", {"start": v(28.98, -12.2) * mm, "end": v(28.89, -12.14) * mm});
            skLineSegment(sketch, "E400", {"start": v(28.89, -12.14) * mm, "end": v(28.8, -12.07) * mm});
            skLineSegment(sketch, "E401", {"start": v(28.8, -12.07) * mm, "end": v(28.73, -11.99) * mm});
            skLineSegment(sketch, "E402", {"start": v(28.73, -11.99) * mm, "end": v(28.66, -11.9) * mm});
            skLineSegment(sketch, "E403", {"start": v(28.66, -11.9) * mm, "end": v(28.6, -11.76) * mm});
            skLineSegment(sketch, "E404", {"start": v(28.6, -11.76) * mm, "end": v(28.59, -11.62) * mm});
            skLineSegment(sketch, "E405", {"start": v(28.59, -11.62) * mm, "end": v(28.6, -11.48) * mm});
            skLineSegment(sketch, "E406", {"start": v(28.6, -11.48) * mm, "end": v(28.64, -11.34) * mm});
            skLineSegment(sketch, "E407", {"start": v(28.64, -11.34) * mm, "end": v(28.7, -11.2) * mm});
            skLineSegment(sketch, "E408", {"start": v(28.7, -11.2) * mm, "end": v(28.8, -11.1) * mm});
            skLineSegment(sketch, "E409", {"start": v(28.8, -11.1) * mm, "end": v(28.9, -11) * mm});
            skLineSegment(sketch, "E410", {"start": v(28.9, -11) * mm, "end": v(29.04, -10.95) * mm});
            skLineSegment(sketch, "E411", {"start": v(29.04, -10.95) * mm, "end": v(29.15, -10.92) * mm});
            skLineSegment(sketch, "E412", {"start": v(29.15, -10.92) * mm, "end": v(29.26, -10.92) * mm});
            skLineSegment(sketch, "E413", {"start": v(29.26, -10.92) * mm, "end": v(29.37, -10.92) * mm});
            skLineSegment(sketch, "E414", {"start": v(29.37, -10.92) * mm, "end": v(29.48, -10.94) * mm});
            skLineSegment(sketch, "E415", {"start": v(29.48, -10.94) * mm, "end": v(29.58, -10.92) * mm});
            skLineSegment(sketch, "E416", {"start": v(29.58, -10.92) * mm, "end": v(29.66, -10.83) * mm});
            skLineSegment(sketch, "E417", {"start": v(29.66, -10.83) * mm, "end": v(29.71, -10.7) * mm});
            skLineSegment(sketch, "E418", {"start": v(29.71, -10.7) * mm, "end": v(29.76, -10.56) * mm});
            skLineSegment(sketch, "E419", {"start": v(29.76, -10.56) * mm, "end": v(29.76, -10.44) * mm});
            skLineSegment(sketch, "E420", {"start": v(29.76, -10.44) * mm, "end": v(29.69, -10.36) * mm});
            skLineSegment(sketch, "E421", {"start": v(29.69, -10.36) * mm, "end": v(29.6, -10.3) * mm});
            skLineSegment(sketch, "E422", {"start": v(29.6, -10.3) * mm, "end": v(29.5, -10.24) * mm});
            skLineSegment(sketch, "E423", {"start": v(29.5, -10.24) * mm, "end": v(29.42, -10.16) * mm});
            skLineSegment(sketch, "E424", {"start": v(29.42, -10.16) * mm, "end": v(29.35, -10.07) * mm});
            skLineSegment(sketch, "E425", {"start": v(29.35, -10.07) * mm, "end": v(29.29, -9.94) * mm});
            skLineSegment(sketch, "E426", {"start": v(29.29, -9.94) * mm, "end": v(29.26, -9.8) * mm});
            skLineSegment(sketch, "E427", {"start": v(29.26, -9.8) * mm, "end": v(29.26, -9.66) * mm});
            skLineSegment(sketch, "E428", {"start": v(29.26, -9.66) * mm, "end": v(29.3, -9.52) * mm});
            skLineSegment(sketch, "E429", {"start": v(29.3, -9.52) * mm, "end": v(29.35, -9.39) * mm});
            skLineSegment(sketch, "E430", {"start": v(29.35, -9.39) * mm, "end": v(29.44, -9.27) * mm});
            skLineSegment(sketch, "E431", {"start": v(29.44, -9.27) * mm, "end": v(29.54, -9.17) * mm});
            skLineSegment(sketch, "E432", {"start": v(29.54, -9.17) * mm, "end": v(29.67, -9.1) * mm});
            skLineSegment(sketch, "E433", {"start": v(29.67, -9.1) * mm, "end": v(29.78, -9.07) * mm});
            skLineSegment(sketch, "E434", {"start": v(29.78, -9.07) * mm, "end": v(29.89, -9.06) * mm});
            skLineSegment(sketch, "E435", {"start": v(29.89, -9.06) * mm, "end": v(30, -9.06) * mm});
            skLineSegment(sketch, "E436", {"start": v(30, -9.06) * mm, "end": v(30.1, -9.07) * mm});
            skLineSegment(sketch, "E437", {"start": v(30.1, -9.07) * mm, "end": v(30.21, -9.04) * mm});
            skLineSegment(sketch, "E438", {"start": v(30.21, -9.04) * mm, "end": v(30.28, -8.95) * mm});
            skLineSegment(sketch, "E439", {"start": v(30.28, -8.95) * mm, "end": v(30.32, -8.8) * mm});
            skLineSegment(sketch, "E440", {"start": v(30.32, -8.8) * mm, "end": v(30.36, -8.67) * mm});
            skLineSegment(sketch, "E441", {"start": v(30.36, -8.67) * mm, "end": v(30.36, -8.55) * mm});
            skLineSegment(sketch, "E442", {"start": v(30.36, -8.55) * mm, "end": v(30.28, -8.47) * mm});
            skLineSegment(sketch, "E443", {"start": v(30.28, -8.47) * mm, "end": v(30.18, -8.43) * mm});
            skLineSegment(sketch, "E444", {"start": v(30.18, -8.43) * mm, "end": v(30.09, -8.37) * mm});
            skLineSegment(sketch, "E445", {"start": v(30.09, -8.37) * mm, "end": v(30, -8.3) * mm});
            skLineSegment(sketch, "E446", {"start": v(30, -8.3) * mm, "end": v(29.92, -8.21) * mm});
            skLineSegment(sketch, "E447", {"start": v(29.92, -8.21) * mm, "end": v(29.86, -8.09) * mm});
            skLineSegment(sketch, "E448", {"start": v(29.86, -8.09) * mm, "end": v(29.82, -7.95) * mm});
            skLineSegment(sketch, "E449", {"start": v(29.82, -7.95) * mm, "end": v(29.81, -7.8) * mm});
            skLineSegment(sketch, "E450", {"start": v(29.81, -7.8) * mm, "end": v(29.83, -7.66) * mm});
            skLineSegment(sketch, "E451", {"start": v(29.83, -7.66) * mm, "end": v(29.88, -7.52) * mm});
            skLineSegment(sketch, "E452", {"start": v(29.88, -7.52) * mm, "end": v(29.96, -7.4) * mm});
            skLineSegment(sketch, "E453", {"start": v(29.96, -7.4) * mm, "end": v(30.06, -7.3) * mm});
            skLineSegment(sketch, "E454", {"start": v(30.06, -7.3) * mm, "end": v(30.18, -7.22) * mm});
            skLineSegment(sketch, "E455", {"start": v(30.18, -7.22) * mm, "end": v(30.29, -7.19) * mm});
            skLineSegment(sketch, "E456", {"start": v(30.29, -7.19) * mm, "end": v(30.4, -7.16) * mm});
            skLineSegment(sketch, "E457", {"start": v(30.4, -7.16) * mm, "end": v(30.5, -7.16) * mm});
            skLineSegment(sketch, "E458", {"start": v(30.5, -7.16) * mm, "end": v(30.62, -7.16) * mm});
            skLineSegment(sketch, "E459", {"start": v(30.62, -7.16) * mm, "end": v(30.72, -7.13) * mm});
            skLineSegment(sketch, "E460", {"start": v(30.72, -7.13) * mm, "end": v(30.78, -7.03) * mm});
            skLineSegment(sketch, "E461", {"start": v(30.78, -7.03) * mm, "end": v(30.82, -6.89) * mm});
            skLineSegment(sketch, "E462", {"start": v(30.82, -6.89) * mm, "end": v(30.85, -6.74) * mm});
            skLineSegment(sketch, "E463", {"start": v(30.85, -6.74) * mm, "end": v(30.83, -6.63) * mm});
            skLineSegment(sketch, "E464", {"start": v(30.83, -6.63) * mm, "end": v(30.75, -6.56) * mm});
            skLineSegment(sketch, "E465", {"start": v(30.75, -6.56) * mm, "end": v(30.65, -6.51) * mm});
            skLineSegment(sketch, "E466", {"start": v(30.65, -6.51) * mm, "end": v(30.55, -6.46) * mm});
            skLineSegment(sketch, "E467", {"start": v(30.55, -6.46) * mm, "end": v(30.46, -6.4) * mm});
            skLineSegment(sketch, "E468", {"start": v(30.46, -6.4) * mm, "end": v(30.38, -6.32) * mm});
            skLineSegment(sketch, "E469", {"start": v(30.38, -6.32) * mm, "end": v(30.3, -6.2) * mm});
            skLineSegment(sketch, "E470", {"start": v(30.3, -6.2) * mm, "end": v(30.26, -6.06) * mm});
            skLineSegment(sketch, "E471", {"start": v(30.26, -6.06) * mm, "end": v(30.24, -5.92) * mm});
            skLineSegment(sketch, "E472", {"start": v(30.24, -5.92) * mm, "end": v(30.26, -5.77) * mm});
            skLineSegment(sketch, "E473", {"start": v(30.26, -5.77) * mm, "end": v(30.3, -5.63) * mm});
            skLineSegment(sketch, "E474", {"start": v(30.3, -5.63) * mm, "end": v(30.36, -5.5) * mm});
            skLineSegment(sketch, "E475", {"start": v(30.36, -5.5) * mm, "end": v(30.46, -5.4) * mm});
            skLineSegment(sketch, "E476", {"start": v(30.46, -5.4) * mm, "end": v(30.57, -5.31) * mm});
            skLineSegment(sketch, "E477", {"start": v(30.57, -5.31) * mm, "end": v(30.68, -5.27) * mm});
            skLineSegment(sketch, "E478", {"start": v(30.68, -5.27) * mm, "end": v(30.79, -5.24) * mm});
            skLineSegment(sketch, "E479", {"start": v(30.79, -5.24) * mm, "end": v(30.9, -5.23) * mm});
            skLineSegment(sketch, "E480", {"start": v(30.9, -5.23) * mm, "end": v(31, -5.22) * mm});
            skLineSegment(sketch, "E481", {"start": v(31, -5.22) * mm, "end": v(31.1, -5.19) * mm});
            skLineSegment(sketch, "E482", {"start": v(31.1, -5.19) * mm, "end": v(31.16, -5.08) * mm});
            skLineSegment(sketch, "E483", {"start": v(31.16, -5.08) * mm, "end": v(31.19, -4.94) * mm});
            skLineSegment(sketch, "E484", {"start": v(31.19, -4.94) * mm, "end": v(31.21, -4.8) * mm});
            skLineSegment(sketch, "E485", {"start": v(31.21, -4.8) * mm, "end": v(31.19, -4.68) * mm});
            skLineSegment(sketch, "E486", {"start": v(31.19, -4.68) * mm, "end": v(31.1, -4.61) * mm});
            skLineSegment(sketch, "E487", {"start": v(31.1, -4.61) * mm, "end": v(31, -4.58) * mm});
            skLineSegment(sketch, "E488", {"start": v(31, -4.58) * mm, "end": v(30.9, -4.53) * mm});
            skLineSegment(sketch, "E489", {"start": v(30.9, -4.53) * mm, "end": v(30.8, -4.47) * mm});
            skLineSegment(sketch, "E490", {"start": v(30.8, -4.47) * mm, "end": v(30.72, -4.4) * mm});
            skLineSegment(sketch, "E491", {"start": v(30.72, -4.4) * mm, "end": v(30.63, -4.28) * mm});
            skLineSegment(sketch, "E492", {"start": v(30.63, -4.28) * mm, "end": v(30.58, -4.15) * mm});
            skLineSegment(sketch, "E493", {"start": v(30.58, -4.15) * mm, "end": v(30.55, -4) * mm});
            skLineSegment(sketch, "E494", {"start": v(30.55, -4) * mm, "end": v(30.56, -3.86) * mm});
            skLineSegment(sketch, "E495", {"start": v(30.56, -3.86) * mm, "end": v(30.6, -3.72) * mm});
            skLineSegment(sketch, "E496", {"start": v(30.6, -3.72) * mm, "end": v(30.65, -3.59) * mm});
            skLineSegment(sketch, "E497", {"start": v(30.65, -3.59) * mm, "end": v(30.74, -3.47) * mm});
            skLineSegment(sketch, "E498", {"start": v(30.74, -3.47) * mm, "end": v(30.85, -3.38) * mm});
            skLineSegment(sketch, "E499", {"start": v(30.85, -3.38) * mm, "end": v(30.95, -3.33) * mm});
            skLineSegment(sketch, "E500", {"start": v(30.95, -3.33) * mm, "end": v(31.05, -3.3) * mm});
            skLineSegment(sketch, "E501", {"start": v(31.05, -3.3) * mm, "end": v(31.16, -3.28) * mm});
            skLineSegment(sketch, "E502", {"start": v(31.16, -3.28) * mm, "end": v(31.27, -3.27) * mm});
            skLineSegment(sketch, "E503", {"start": v(31.27, -3.27) * mm, "end": v(31.37, -3.22) * mm});
            skLineSegment(sketch, "E504", {"start": v(31.37, -3.22) * mm, "end": v(31.42, -3.12) * mm});
            skLineSegment(sketch, "E505", {"start": v(31.42, -3.12) * mm, "end": v(31.44, -2.97) * mm});
            skLineSegment(sketch, "E506", {"start": v(31.44, -2.97) * mm, "end": v(31.45, -2.83) * mm});
            skLineSegment(sketch, "E507", {"start": v(31.45, -2.83) * mm, "end": v(31.42, -2.71) * mm});
            skLineSegment(sketch, "E508", {"start": v(31.42, -2.71) * mm, "end": v(31.33, -2.65) * mm});
            skLineSegment(sketch, "E509", {"start": v(31.33, -2.65) * mm, "end": v(31.22, -2.62) * mm});
            skLineSegment(sketch, "E510", {"start": v(31.22, -2.62) * mm, "end": v(31.12, -2.58) * mm});
            skLineSegment(sketch, "E511", {"start": v(31.12, -2.58) * mm, "end": v(31.02, -2.53) * mm});
            skLineSegment(sketch, "E512", {"start": v(31.02, -2.53) * mm, "end": v(30.93, -2.46) * mm});
            skLineSegment(sketch, "E513", {"start": v(30.93, -2.46) * mm, "end": v(30.84, -2.35) * mm});
            skLineSegment(sketch, "E514", {"start": v(30.84, -2.35) * mm, "end": v(30.78, -2.22) * mm});
            skLineSegment(sketch, "E515", {"start": v(30.78, -2.22) * mm, "end": v(30.75, -2.08) * mm});
            skLineSegment(sketch, "E516", {"start": v(30.75, -2.08) * mm, "end": v(30.74, -1.93) * mm});
            skLineSegment(sketch, "E517", {"start": v(30.74, -1.93) * mm, "end": v(30.76, -1.8) * mm});
            skLineSegment(sketch, "E518", {"start": v(30.76, -1.8) * mm, "end": v(30.82, -1.66) * mm});
            skLineSegment(sketch, "E519", {"start": v(30.82, -1.66) * mm, "end": v(30.9, -1.54) * mm});
            skLineSegment(sketch, "E520", {"start": v(30.9, -1.54) * mm, "end": v(31, -1.44) * mm});
            skLineSegment(sketch, "E521", {"start": v(31, -1.44) * mm, "end": v(31.1, -1.38) * mm});
            skLineSegment(sketch, "E522", {"start": v(31.1, -1.38) * mm, "end": v(31.2, -1.34) * mm});
            skLineSegment(sketch, "E523", {"start": v(31.2, -1.34) * mm, "end": v(31.3, -1.31) * mm});
            skLineSegment(sketch, "E524", {"start": v(31.3, -1.31) * mm, "end": v(31.42, -1.3) * mm});
            skLineSegment(sketch, "E525", {"start": v(31.42, -1.3) * mm, "end": v(31.51, -1.25) * mm});
            skLineSegment(sketch, "E526", {"start": v(31.51, -1.25) * mm, "end": v(31.56, -1.14) * mm});
            skLineSegment(sketch, "E527", {"start": v(31.56, -1.14) * mm, "end": v(31.56, -1) * mm});
            skLineSegment(sketch, "E528", {"start": v(31.56, -1) * mm, "end": v(31.56, -0.84) * mm});
            skLineSegment(sketch, "E529", {"start": v(31.56, -0.84) * mm, "end": v(31.53, -0.73) * mm});
            skLineSegment(sketch, "E530", {"start": v(31.53, -0.73) * mm, "end": v(31.44, -0.68) * mm});
            skLineSegment(sketch, "E531", {"start": v(31.44, -0.68) * mm, "end": v(31.33, -0.66) * mm});
            skLineSegment(sketch, "E532", {"start": v(31.33, -0.66) * mm, "end": v(31.22, -0.62) * mm});
            skLineSegment(sketch, "E533", {"start": v(31.22, -0.62) * mm, "end": v(31.12, -0.57) * mm});
            skLineSegment(sketch, "E534", {"start": v(31.12, -0.57) * mm, "end": v(31.03, -0.51) * mm});
            skLineSegment(sketch, "E535", {"start": v(31.03, -0.51) * mm, "end": v(30.93, -0.4) * mm});
            skLineSegment(sketch, "E536", {"start": v(30.93, -0.4) * mm, "end": v(30.86, -0.28) * mm});
            skLineSegment(sketch, "E537", {"start": v(30.86, -0.28) * mm, "end": v(30.82, -0.14) * mm});
            skLineSegment(sketch, "E538", {"start": v(30.82, -0.14) * mm, "end": v(30.8, 0) * mm});
            skLineSegment(sketch, "E539", {"start": v(30.8, 0) * mm, "end": v(30.82, 0.14) * mm});
            skLineSegment(sketch, "E540", {"start": v(30.82, 0.14) * mm, "end": v(30.86, 0.28) * mm});
            skLineSegment(sketch, "E541", {"start": v(30.86, 0.28) * mm, "end": v(30.93, 0.4) * mm});
            skLineSegment(sketch, "E542", {"start": v(30.93, 0.4) * mm, "end": v(31.03, 0.51) * mm});
            skLineSegment(sketch, "E543", {"start": v(31.03, 0.51) * mm, "end": v(31.12, 0.57) * mm});
            skLineSegment(sketch, "E544", {"start": v(31.12, 0.57) * mm, "end": v(31.22, 0.62) * mm});
            skLineSegment(sketch, "E545", {"start": v(31.22, 0.62) * mm, "end": v(31.33, 0.66) * mm});
            skLineSegment(sketch, "E546", {"start": v(31.33, 0.66) * mm, "end": v(31.44, 0.68) * mm});
            skLineSegment(sketch, "E547", {"start": v(31.44, 0.68) * mm, "end": v(31.53, 0.73) * mm});
            skLineSegment(sketch, "E548", {"start": v(31.53, 0.73) * mm, "end": v(31.56, 0.84) * mm});
            skLineSegment(sketch, "E549", {"start": v(31.56, 0.84) * mm, "end": v(31.56, 1) * mm});
            skLineSegment(sketch, "E550", {"start": v(31.56, 1) * mm, "end": v(31.56, 1.14) * mm});
            skLineSegment(sketch, "E551", {"start": v(31.56, 1.14) * mm, "end": v(31.51, 1.25) * mm});
            skLineSegment(sketch, "E552", {"start": v(31.51, 1.25) * mm, "end": v(31.42, 1.3) * mm});
            skLineSegment(sketch, "E553", {"start": v(31.42, 1.3) * mm, "end": v(31.3, 1.31) * mm});
            skLineSegment(sketch, "E554", {"start": v(31.3, 1.31) * mm, "end": v(31.2, 1.34) * mm});
            skLineSegment(sketch, "E555", {"start": v(31.2, 1.34) * mm, "end": v(31.1, 1.38) * mm});
            skLineSegment(sketch, "E556", {"start": v(31.1, 1.38) * mm, "end": v(31, 1.44) * mm});
            skLineSegment(sketch, "E557", {"start": v(31, 1.44) * mm, "end": v(30.9, 1.54) * mm});
            skLineSegment(sketch, "E558", {"start": v(30.9, 1.54) * mm, "end": v(30.82, 1.66) * mm});
            skLineSegment(sketch, "E559", {"start": v(30.82, 1.66) * mm, "end": v(30.76, 1.8) * mm});
            skLineSegment(sketch, "E560", {"start": v(30.76, 1.8) * mm, "end": v(30.74, 1.93) * mm});
            skLineSegment(sketch, "E561", {"start": v(30.74, 1.93) * mm, "end": v(30.75, 2.08) * mm});
            skLineSegment(sketch, "E562", {"start": v(30.75, 2.08) * mm, "end": v(30.78, 2.22) * mm});
            skLineSegment(sketch, "E563", {"start": v(30.78, 2.22) * mm, "end": v(30.84, 2.35) * mm});
            skLineSegment(sketch, "E564", {"start": v(30.84, 2.35) * mm, "end": v(30.93, 2.46) * mm});
            skLineSegment(sketch, "E565", {"start": v(30.93, 2.46) * mm, "end": v(31.02, 2.53) * mm});
            skLineSegment(sketch, "E566", {"start": v(31.02, 2.53) * mm, "end": v(31.12, 2.58) * mm});
            skLineSegment(sketch, "E567", {"start": v(31.12, 2.58) * mm, "end": v(31.22, 2.62) * mm});
            skLineSegment(sketch, "E568", {"start": v(31.22, 2.62) * mm, "end": v(31.33, 2.65) * mm});
            skLineSegment(sketch, "E569", {"start": v(31.33, 2.65) * mm, "end": v(31.42, 2.71) * mm});
            skLineSegment(sketch, "E570", {"start": v(31.42, 2.71) * mm, "end": v(31.45, 2.83) * mm});
            skLineSegment(sketch, "E571", {"start": v(31.45, 2.83) * mm, "end": v(31.44, 2.97) * mm});
            skLineSegment(sketch, "E572", {"start": v(31.44, 2.97) * mm, "end": v(31.42, 3.12) * mm});
            skLineSegment(sketch, "E573", {"start": v(31.42, 3.12) * mm, "end": v(31.37, 3.22) * mm});
            skLineSegment(sketch, "E574", {"start": v(31.37, 3.22) * mm, "end": v(31.27, 3.27) * mm});
            skLineSegment(sketch, "E575", {"start": v(31.27, 3.27) * mm, "end": v(31.16, 3.28) * mm});
            skLineSegment(sketch, "E576", {"start": v(31.16, 3.28) * mm, "end": v(31.05, 3.3) * mm});
            skLineSegment(sketch, "E577", {"start": v(31.05, 3.3) * mm, "end": v(30.95, 3.33) * mm});
            skLineSegment(sketch, "E578", {"start": v(30.95, 3.33) * mm, "end": v(30.85, 3.38) * mm});
            skLineSegment(sketch, "E579", {"start": v(30.85, 3.38) * mm, "end": v(30.74, 3.47) * mm});
            skLineSegment(sketch, "E580", {"start": v(30.74, 3.47) * mm, "end": v(30.65, 3.59) * mm});
            skLineSegment(sketch, "E581", {"start": v(30.65, 3.59) * mm, "end": v(30.6, 3.72) * mm});
            skLineSegment(sketch, "E582", {"start": v(30.6, 3.72) * mm, "end": v(30.56, 3.86) * mm});
            skLineSegment(sketch, "E583", {"start": v(30.56, 3.86) * mm, "end": v(30.55, 4) * mm});
            skLineSegment(sketch, "E584", {"start": v(30.55, 4) * mm, "end": v(30.58, 4.15) * mm});
            skLineSegment(sketch, "E585", {"start": v(30.58, 4.15) * mm, "end": v(30.63, 4.28) * mm});
            skLineSegment(sketch, "E586", {"start": v(30.63, 4.28) * mm, "end": v(30.72, 4.4) * mm});
            skLineSegment(sketch, "E587", {"start": v(30.72, 4.4) * mm, "end": v(30.8, 4.47) * mm});
            skLineSegment(sketch, "E588", {"start": v(30.8, 4.47) * mm, "end": v(30.9, 4.53) * mm});
            skLineSegment(sketch, "E589", {"start": v(30.9, 4.53) * mm, "end": v(31, 4.58) * mm});
            skLineSegment(sketch, "E590", {"start": v(31, 4.58) * mm, "end": v(31.1, 4.61) * mm});
            skLineSegment(sketch, "E591", {"start": v(31.1, 4.61) * mm, "end": v(31.19, 4.68) * mm});
            skLineSegment(sketch, "E592", {"start": v(31.19, 4.68) * mm, "end": v(31.21, 4.8) * mm});
            skLineSegment(sketch, "E593", {"start": v(31.21, 4.8) * mm, "end": v(31.19, 4.94) * mm});
            skLineSegment(sketch, "E594", {"start": v(31.19, 4.94) * mm, "end": v(31.16, 5.08) * mm});
            skLineSegment(sketch, "E595", {"start": v(31.16, 5.08) * mm, "end": v(31.1, 5.19) * mm});
            skLineSegment(sketch, "E596", {"start": v(31.1, 5.19) * mm, "end": v(31, 5.22) * mm});
            skLineSegment(sketch, "E597", {"start": v(31, 5.22) * mm, "end": v(30.9, 5.23) * mm});
            skLineSegment(sketch, "E598", {"start": v(30.9, 5.23) * mm, "end": v(30.79, 5.24) * mm});
            skLineSegment(sketch, "E599", {"start": v(30.79, 5.24) * mm, "end": v(30.68, 5.27) * mm});
            skLineSegment(sketch, "E600", {"start": v(30.68, 5.27) * mm, "end": v(30.57, 5.31) * mm});
            skLineSegment(sketch, "E601", {"start": v(30.57, 5.31) * mm, "end": v(30.46, 5.4) * mm});
            skLineSegment(sketch, "E602", {"start": v(30.46, 5.4) * mm, "end": v(30.36, 5.5) * mm});
            skLineSegment(sketch, "E603", {"start": v(30.36, 5.5) * mm, "end": v(30.3, 5.63) * mm});
            skLineSegment(sketch, "E604", {"start": v(30.3, 5.63) * mm, "end": v(30.26, 5.77) * mm});
            skLineSegment(sketch, "E605", {"start": v(30.26, 5.77) * mm, "end": v(30.24, 5.92) * mm});
            skLineSegment(sketch, "E606", {"start": v(30.24, 5.92) * mm, "end": v(30.26, 6.06) * mm});
            skLineSegment(sketch, "E607", {"start": v(30.26, 6.06) * mm, "end": v(30.3, 6.2) * mm});
            skLineSegment(sketch, "E608", {"start": v(30.3, 6.2) * mm, "end": v(30.38, 6.32) * mm});
            skLineSegment(sketch, "E609", {"start": v(30.38, 6.32) * mm, "end": v(30.46, 6.4) * mm});
            skLineSegment(sketch, "E610", {"start": v(30.46, 6.4) * mm, "end": v(30.55, 6.46) * mm});
            skLineSegment(sketch, "E611", {"start": v(30.55, 6.46) * mm, "end": v(30.65, 6.51) * mm});
            skLineSegment(sketch, "E612", {"start": v(30.65, 6.51) * mm, "end": v(30.75, 6.56) * mm});
            skLineSegment(sketch, "E613", {"start": v(30.75, 6.56) * mm, "end": v(30.83, 6.63) * mm});
            skLineSegment(sketch, "E614", {"start": v(30.83, 6.63) * mm, "end": v(30.85, 6.74) * mm});
            skLineSegment(sketch, "E615", {"start": v(30.85, 6.74) * mm, "end": v(30.82, 6.89) * mm});
            skLineSegment(sketch, "E616", {"start": v(30.82, 6.89) * mm, "end": v(30.78, 7.03) * mm});
            skLineSegment(sketch, "E617", {"start": v(30.78, 7.03) * mm, "end": v(30.72, 7.13) * mm});
            skLineSegment(sketch, "E618", {"start": v(30.72, 7.13) * mm, "end": v(30.62, 7.16) * mm});
            skLineSegment(sketch, "E619", {"start": v(30.62, 7.16) * mm, "end": v(30.5, 7.16) * mm});
            skLineSegment(sketch, "E620", {"start": v(30.5, 7.16) * mm, "end": v(30.4, 7.16) * mm});
            skLineSegment(sketch, "E621", {"start": v(30.4, 7.16) * mm, "end": v(30.29, 7.19) * mm});
            skLineSegment(sketch, "E622", {"start": v(30.29, 7.19) * mm, "end": v(30.18, 7.22) * mm});
            skLineSegment(sketch, "E623", {"start": v(30.18, 7.22) * mm, "end": v(30.06, 7.3) * mm});
            skLineSegment(sketch, "E624", {"start": v(30.06, 7.3) * mm, "end": v(29.96, 7.4) * mm});
            skLineSegment(sketch, "E625", {"start": v(29.96, 7.4) * mm, "end": v(29.88, 7.52) * mm});
            skLineSegment(sketch, "E626", {"start": v(29.88, 7.52) * mm, "end": v(29.83, 7.66) * mm});
            skLineSegment(sketch, "E627", {"start": v(29.83, 7.66) * mm, "end": v(29.81, 7.8) * mm});
            skLineSegment(sketch, "E628", {"start": v(29.81, 7.8) * mm, "end": v(29.82, 7.95) * mm});
            skLineSegment(sketch, "E629", {"start": v(29.82, 7.95) * mm, "end": v(29.86, 8.09) * mm});
            skLineSegment(sketch, "E630", {"start": v(29.86, 8.09) * mm, "end": v(29.92, 8.21) * mm});
            skLineSegment(sketch, "E631", {"start": v(29.92, 8.21) * mm, "end": v(30, 8.3) * mm});
            skLineSegment(sketch, "E632", {"start": v(30, 8.3) * mm, "end": v(30.09, 8.37) * mm});
            skLineSegment(sketch, "E633", {"start": v(30.09, 8.37) * mm, "end": v(30.18, 8.43) * mm});
            skLineSegment(sketch, "E634", {"start": v(30.18, 8.43) * mm, "end": v(30.28, 8.47) * mm});
            skLineSegment(sketch, "E635", {"start": v(30.28, 8.47) * mm, "end": v(30.36, 8.55) * mm});
            skLineSegment(sketch, "E636", {"start": v(30.36, 8.55) * mm, "end": v(30.36, 8.67) * mm});
            skLineSegment(sketch, "E637", {"start": v(30.36, 8.67) * mm, "end": v(30.32, 8.8) * mm});
            skLineSegment(sketch, "E638", {"start": v(30.32, 8.8) * mm, "end": v(30.28, 8.95) * mm});
            skLineSegment(sketch, "E639", {"start": v(30.28, 8.95) * mm, "end": v(30.21, 9.04) * mm});
            skLineSegment(sketch, "E640", {"start": v(30.21, 9.04) * mm, "end": v(30.1, 9.07) * mm});
            skLineSegment(sketch, "E641", {"start": v(30.1, 9.07) * mm, "end": v(30, 9.06) * mm});
            skLineSegment(sketch, "E642", {"start": v(30, 9.06) * mm, "end": v(29.89, 9.06) * mm});
            skLineSegment(sketch, "E643", {"start": v(29.89, 9.06) * mm, "end": v(29.78, 9.07) * mm});
            skLineSegment(sketch, "E644", {"start": v(29.78, 9.07) * mm, "end": v(29.67, 9.1) * mm});
            skLineSegment(sketch, "E645", {"start": v(29.67, 9.1) * mm, "end": v(29.54, 9.17) * mm});
            skLineSegment(sketch, "E646", {"start": v(29.54, 9.17) * mm, "end": v(29.44, 9.27) * mm});
            skLineSegment(sketch, "E647", {"start": v(29.44, 9.27) * mm, "end": v(29.35, 9.39) * mm});
            skLineSegment(sketch, "E648", {"start": v(29.35, 9.39) * mm, "end": v(29.3, 9.52) * mm});
            skLineSegment(sketch, "E649", {"start": v(29.3, 9.52) * mm, "end": v(29.26, 9.66) * mm});
            skLineSegment(sketch, "E650", {"start": v(29.26, 9.66) * mm, "end": v(29.26, 9.8) * mm});
            skLineSegment(sketch, "E651", {"start": v(29.26, 9.8) * mm, "end": v(29.29, 9.94) * mm});
            skLineSegment(sketch, "E652", {"start": v(29.29, 9.94) * mm, "end": v(29.35, 10.07) * mm});
            skLineSegment(sketch, "E653", {"start": v(29.35, 10.07) * mm, "end": v(29.42, 10.16) * mm});
            skLineSegment(sketch, "E654", {"start": v(29.42, 10.16) * mm, "end": v(29.5, 10.24) * mm});
            skLineSegment(sketch, "E655", {"start": v(29.5, 10.24) * mm, "end": v(29.6, 10.3) * mm});
            skLineSegment(sketch, "E656", {"start": v(29.6, 10.3) * mm, "end": v(29.69, 10.36) * mm});
            skLineSegment(sketch, "E657", {"start": v(29.69, 10.36) * mm, "end": v(29.76, 10.44) * mm});
            skLineSegment(sketch, "E658", {"start": v(29.76, 10.44) * mm, "end": v(29.76, 10.56) * mm});
            skLineSegment(sketch, "E659", {"start": v(29.76, 10.56) * mm, "end": v(29.71, 10.7) * mm});
            skLineSegment(sketch, "E660", {"start": v(29.71, 10.7) * mm, "end": v(29.66, 10.83) * mm});
            skLineSegment(sketch, "E661", {"start": v(29.66, 10.83) * mm, "end": v(29.58, 10.92) * mm});
            skLineSegment(sketch, "E662", {"start": v(29.58, 10.92) * mm, "end": v(29.48, 10.94) * mm});
            skLineSegment(sketch, "E663", {"start": v(29.48, 10.94) * mm, "end": v(29.37, 10.92) * mm});
            skLineSegment(sketch, "E664", {"start": v(29.37, 10.92) * mm, "end": v(29.26, 10.92) * mm});
            skLineSegment(sketch, "E665", {"start": v(29.26, 10.92) * mm, "end": v(29.15, 10.92) * mm});
            skLineSegment(sketch, "E666", {"start": v(29.15, 10.92) * mm, "end": v(29.04, 10.95) * mm});
            skLineSegment(sketch, "E667", {"start": v(29.04, 10.95) * mm, "end": v(28.9, 11) * mm});
            skLineSegment(sketch, "E668", {"start": v(28.9, 11) * mm, "end": v(28.8, 11.1) * mm});
            skLineSegment(sketch, "E669", {"start": v(28.8, 11.1) * mm, "end": v(28.7, 11.2) * mm});
            skLineSegment(sketch, "E670", {"start": v(28.7, 11.2) * mm, "end": v(28.64, 11.34) * mm});
            skLineSegment(sketch, "E671", {"start": v(28.64, 11.34) * mm, "end": v(28.6, 11.48) * mm});
            skLineSegment(sketch, "E672", {"start": v(28.6, 11.48) * mm, "end": v(28.59, 11.62) * mm});
            skLineSegment(sketch, "E673", {"start": v(28.59, 11.62) * mm, "end": v(28.6, 11.76) * mm});
            skLineSegment(sketch, "E674", {"start": v(28.6, 11.76) * mm, "end": v(28.66, 11.9) * mm});
            skLineSegment(sketch, "E675", {"start": v(28.66, 11.9) * mm, "end": v(28.73, 11.99) * mm});
            skLineSegment(sketch, "E676", {"start": v(28.73, 11.99) * mm, "end": v(28.8, 12.07) * mm});
            skLineSegment(sketch, "E677", {"start": v(28.8, 12.07) * mm, "end": v(28.89, 12.14) * mm});
            skLineSegment(sketch, "E678", {"start": v(28.89, 12.14) * mm, "end": v(28.98, 12.2) * mm});
            skLineSegment(sketch, "E679", {"start": v(28.98, 12.2) * mm, "end": v(29.04, 12.29) * mm});
            skLineSegment(sketch, "E680", {"start": v(29.04, 12.29) * mm, "end": v(29.04, 12.4) * mm});
            skLineSegment(sketch, "E681", {"start": v(29.04, 12.4) * mm, "end": v(28.98, 12.54) * mm});
            skLineSegment(sketch, "E682", {"start": v(28.98, 12.54) * mm, "end": v(28.92, 12.68) * mm});
            skLineSegment(sketch, "E683", {"start": v(28.92, 12.68) * mm, "end": v(28.84, 12.76) * mm});
            skLineSegment(sketch, "E684", {"start": v(28.84, 12.76) * mm, "end": v(28.73, 12.77) * mm});
            skLineSegment(sketch, "E685", {"start": v(28.73, 12.77) * mm, "end": v(28.62, 12.74) * mm});
            skLineSegment(sketch, "E686", {"start": v(28.62, 12.74) * mm, "end": v(28.52, 12.73) * mm});
            skLineSegment(sketch, "E687", {"start": v(28.52, 12.73) * mm, "end": v(28.4, 12.73) * mm});
            skLineSegment(sketch, "E688", {"start": v(28.4, 12.73) * mm, "end": v(28.3, 12.75) * mm});
            skLineSegment(sketch, "E689", {"start": v(28.3, 12.75) * mm, "end": v(28.16, 12.8) * mm});
            skLineSegment(sketch, "E690", {"start": v(28.16, 12.8) * mm, "end": v(28.04, 12.88) * mm});
            skLineSegment(sketch, "E691", {"start": v(28.04, 12.88) * mm, "end": v(27.94, 13) * mm});
            skLineSegment(sketch, "E692", {"start": v(27.94, 13) * mm, "end": v(27.87, 13.11) * mm});
            skLineSegment(sketch, "E693", {"start": v(27.87, 13.11) * mm, "end": v(27.82, 13.25) * mm});
            skLineSegment(sketch, "E694", {"start": v(27.82, 13.25) * mm, "end": v(27.8, 13.4) * mm});
            skLineSegment(sketch, "E695", {"start": v(27.8, 13.4) * mm, "end": v(27.81, 13.54) * mm});
            skLineSegment(sketch, "E696", {"start": v(27.81, 13.54) * mm, "end": v(27.86, 13.67) * mm});
            skLineSegment(sketch, "E697", {"start": v(27.86, 13.67) * mm, "end": v(27.92, 13.77) * mm});
            skLineSegment(sketch, "E698", {"start": v(27.92, 13.77) * mm, "end": v(27.99, 13.86) * mm});
            skLineSegment(sketch, "E699", {"start": v(27.99, 13.86) * mm, "end": v(28.07, 13.93) * mm});
            skLineSegment(sketch, "E700", {"start": v(28.07, 13.93) * mm, "end": v(28.15, 14) * mm});
            skLineSegment(sketch, "E701", {"start": v(28.15, 14) * mm, "end": v(28.21, 14.09) * mm});
            skLineSegment(sketch, "E702", {"start": v(28.21, 14.09) * mm, "end": v(28.2, 14.2) * mm});
            skLineSegment(sketch, "E703", {"start": v(28.2, 14.2) * mm, "end": v(28.14, 14.34) * mm});
            skLineSegment(sketch, "E704", {"start": v(28.14, 14.34) * mm, "end": v(28.07, 14.47) * mm});
            skLineSegment(sketch, "E705", {"start": v(28.07, 14.47) * mm, "end": v(27.98, 14.55) * mm});
            skLineSegment(sketch, "E706", {"start": v(27.98, 14.55) * mm, "end": v(27.87, 14.55) * mm});
            skLineSegment(sketch, "E707", {"start": v(27.87, 14.55) * mm, "end": v(27.77, 14.52) * mm});
            skLineSegment(sketch, "E708", {"start": v(27.77, 14.52) * mm, "end": v(27.66, 14.5) * mm});
            skLineSegment(sketch, "E709", {"start": v(27.66, 14.5) * mm, "end": v(27.55, 14.5) * mm});
            skLineSegment(sketch, "E710", {"start": v(27.55, 14.5) * mm, "end": v(27.43, 14.5) * mm});
            skLineSegment(sketch, "E711", {"start": v(27.43, 14.5) * mm, "end": v(27.3, 14.54) * mm});
            skLineSegment(sketch, "E712", {"start": v(27.3, 14.54) * mm, "end": v(27.18, 14.62) * mm});
            skLineSegment(sketch, "E713", {"start": v(27.18, 14.62) * mm, "end": v(27.07, 14.72) * mm});
            skLineSegment(sketch, "E714", {"start": v(27.07, 14.72) * mm, "end": v(27, 14.84) * mm});
            skLineSegment(sketch, "E715", {"start": v(27, 14.84) * mm, "end": v(26.93, 14.97) * mm});
            skLineSegment(sketch, "E716", {"start": v(26.93, 14.97) * mm, "end": v(26.9, 15.11) * mm});
            skLineSegment(sketch, "E717", {"start": v(26.9, 15.11) * mm, "end": v(26.9, 15.26) * mm});
            skLineSegment(sketch, "E718", {"start": v(26.9, 15.26) * mm, "end": v(26.94, 15.4) * mm});
            skLineSegment(sketch, "E719", {"start": v(26.94, 15.4) * mm, "end": v(27, 15.5) * mm});
            skLineSegment(sketch, "E720", {"start": v(27, 15.5) * mm, "end": v(27.06, 15.59) * mm});
            skLineSegment(sketch, "E721", {"start": v(27.06, 15.59) * mm, "end": v(27.14, 15.67) * mm});
            skLineSegment(sketch, "E722", {"start": v(27.14, 15.67) * mm, "end": v(27.22, 15.74) * mm});
            skLineSegment(sketch, "E723", {"start": v(27.22, 15.74) * mm, "end": v(27.27, 15.83) * mm});
            skLineSegment(sketch, "E724", {"start": v(27.27, 15.83) * mm, "end": v(27.25, 15.95) * mm});
            skLineSegment(sketch, "E725", {"start": v(27.25, 15.95) * mm, "end": v(27.18, 16.07) * mm});
            skLineSegment(sketch, "E726", {"start": v(27.18, 16.07) * mm, "end": v(27.1, 16.2) * mm});
            skLineSegment(sketch, "E727", {"start": v(27.1, 16.2) * mm, "end": v(27.01, 16.27) * mm});
            skLineSegment(sketch, "E728", {"start": v(27.01, 16.27) * mm, "end": v(26.9, 16.27) * mm});
            skLineSegment(sketch, "E729", {"start": v(26.9, 16.27) * mm, "end": v(26.8, 16.23) * mm});
            skLineSegment(sketch, "E730", {"start": v(26.8, 16.23) * mm, "end": v(26.7, 16.2) * mm});
            skLineSegment(sketch, "E731", {"start": v(26.7, 16.2) * mm, "end": v(26.58, 16.2) * mm});
            skLineSegment(sketch, "E732", {"start": v(26.58, 16.2) * mm, "end": v(26.47, 16.2) * mm});
            skLineSegment(sketch, "E733", {"start": v(26.47, 16.2) * mm, "end": v(26.33, 16.23) * mm});
            skLineSegment(sketch, "E734", {"start": v(26.33, 16.23) * mm, "end": v(26.2, 16.3) * mm});
            skLineSegment(sketch, "E735", {"start": v(26.2, 16.3) * mm, "end": v(26.1, 16.4) * mm});
            skLineSegment(sketch, "E736", {"start": v(26.1, 16.4) * mm, "end": v(26, 16.5) * mm});
            skLineSegment(sketch, "E737", {"start": v(26, 16.5) * mm, "end": v(25.94, 16.63) * mm});
            skLineSegment(sketch, "E738", {"start": v(25.94, 16.63) * mm, "end": v(25.9, 16.77) * mm});
            skLineSegment(sketch, "E739", {"start": v(25.9, 16.77) * mm, "end": v(25.9, 16.92) * mm});
            skLineSegment(sketch, "E740", {"start": v(25.9, 16.92) * mm, "end": v(25.92, 17.06) * mm});
            skLineSegment(sketch, "E741", {"start": v(25.92, 17.06) * mm, "end": v(25.97, 17.16) * mm});
            skLineSegment(sketch, "E742", {"start": v(25.97, 17.16) * mm, "end": v(26.03, 17.25) * mm});
            skLineSegment(sketch, "E743", {"start": v(26.03, 17.25) * mm, "end": v(26.1, 17.34) * mm});
            skLineSegment(sketch, "E744", {"start": v(26.1, 17.34) * mm, "end": v(26.18, 17.42) * mm});
            skLineSegment(sketch, "E745", {"start": v(26.18, 17.42) * mm, "end": v(26.23, 17.51) * mm});
            skLineSegment(sketch, "E746", {"start": v(26.23, 17.51) * mm, "end": v(26.2, 17.63) * mm});
            skLineSegment(sketch, "E747", {"start": v(26.2, 17.63) * mm, "end": v(26.12, 17.75) * mm});
            skLineSegment(sketch, "E748", {"start": v(26.12, 17.75) * mm, "end": v(26.03, 17.87) * mm});
            skLineSegment(sketch, "E749", {"start": v(26.03, 17.87) * mm, "end": v(25.94, 17.94) * mm});
            skLineSegment(sketch, "E750", {"start": v(25.94, 17.94) * mm, "end": v(25.83, 17.93) * mm});
            skLineSegment(sketch, "E751", {"start": v(25.83, 17.93) * mm, "end": v(25.73, 17.88) * mm});
            skLineSegment(sketch, "E752", {"start": v(25.73, 17.88) * mm, "end": v(25.62, 17.85) * mm});
            skLineSegment(sketch, "E753", {"start": v(25.62, 17.85) * mm, "end": v(25.51, 17.83) * mm});
            skLineSegment(sketch, "E754", {"start": v(25.51, 17.83) * mm, "end": v(25.4, 17.82) * mm});
            skLineSegment(sketch, "E755", {"start": v(25.4, 17.82) * mm, "end": v(25.26, 17.85) * mm});
            skLineSegment(sketch, "E756", {"start": v(25.26, 17.85) * mm, "end": v(25.13, 17.91) * mm});
            skLineSegment(sketch, "E757", {"start": v(25.13, 17.91) * mm, "end": v(25.02, 18) * mm});
            skLineSegment(sketch, "E758", {"start": v(25.02, 18) * mm, "end": v(24.92, 18.1) * mm});
            skLineSegment(sketch, "E759", {"start": v(24.92, 18.1) * mm, "end": v(24.85, 18.23) * mm});
            skLineSegment(sketch, "E760", {"start": v(24.85, 18.23) * mm, "end": v(24.8, 18.37) * mm});
            skLineSegment(sketch, "E761", {"start": v(24.8, 18.37) * mm, "end": v(24.78, 18.5) * mm});
            skLineSegment(sketch, "E762", {"start": v(24.78, 18.5) * mm, "end": v(24.8, 18.65) * mm});
            skLineSegment(sketch, "E763", {"start": v(24.8, 18.65) * mm, "end": v(24.84, 18.76) * mm});
            skLineSegment(sketch, "E764", {"start": v(24.84, 18.76) * mm, "end": v(24.9, 18.85) * mm});
            skLineSegment(sketch, "E765", {"start": v(24.9, 18.85) * mm, "end": v(24.96, 18.94) * mm});
            skLineSegment(sketch, "E766", {"start": v(24.96, 18.94) * mm, "end": v(25.03, 19.03) * mm});
            skLineSegment(sketch, "E767", {"start": v(25.03, 19.03) * mm, "end": v(25.08, 19.13) * mm});
            skLineSegment(sketch, "E768", {"start": v(25.08, 19.13) * mm, "end": v(25.04, 19.24) * mm});
            skLineSegment(sketch, "E769", {"start": v(25.04, 19.24) * mm, "end": v(24.95, 19.35) * mm});
            skLineSegment(sketch, "E770", {"start": v(24.95, 19.35) * mm, "end": v(24.86, 19.47) * mm});
            skLineSegment(sketch, "E771", {"start": v(24.86, 19.47) * mm, "end": v(24.76, 19.53) * mm});
            skLineSegment(sketch, "E772", {"start": v(24.76, 19.53) * mm, "end": v(24.65, 19.51) * mm});
            skLineSegment(sketch, "E773", {"start": v(24.65, 19.51) * mm, "end": v(24.56, 19.46) * mm});
            skLineSegment(sketch, "E774", {"start": v(24.56, 19.46) * mm, "end": v(24.45, 19.42) * mm});
            skLineSegment(sketch, "E775", {"start": v(24.45, 19.42) * mm, "end": v(24.34, 19.4) * mm});
            skLineSegment(sketch, "E776", {"start": v(24.34, 19.4) * mm, "end": v(24.23, 19.38) * mm});
            skLineSegment(sketch, "E777", {"start": v(24.23, 19.38) * mm, "end": v(24.09, 19.4) * mm});
            skLineSegment(sketch, "E778", {"start": v(24.09, 19.4) * mm, "end": v(23.96, 19.45) * mm});
            skLineSegment(sketch, "E779", {"start": v(23.96, 19.45) * mm, "end": v(23.84, 19.53) * mm});
            skLineSegment(sketch, "E780", {"start": v(23.84, 19.53) * mm, "end": v(23.73, 19.63) * mm});
            skLineSegment(sketch, "E781", {"start": v(23.73, 19.63) * mm, "end": v(23.65, 19.75) * mm});
            skLineSegment(sketch, "E782", {"start": v(23.65, 19.75) * mm, "end": v(23.6, 19.89) * mm});
            skLineSegment(sketch, "E783", {"start": v(23.6, 19.89) * mm, "end": v(23.57, 20.03) * mm});
            skLineSegment(sketch, "E784", {"start": v(23.57, 20.03) * mm, "end": v(23.58, 20.17) * mm});
            skLineSegment(sketch, "E785", {"start": v(23.58, 20.17) * mm, "end": v(23.62, 20.28) * mm});
            skLineSegment(sketch, "E786", {"start": v(23.62, 20.28) * mm, "end": v(23.66, 20.38) * mm});
            skLineSegment(sketch, "E787", {"start": v(23.66, 20.38) * mm, "end": v(23.72, 20.47) * mm});
            skLineSegment(sketch, "E788", {"start": v(23.72, 20.47) * mm, "end": v(23.79, 20.56) * mm});
            skLineSegment(sketch, "E789", {"start": v(23.79, 20.56) * mm, "end": v(23.82, 20.66) * mm});
            skLineSegment(sketch, "E790", {"start": v(23.82, 20.66) * mm, "end": v(23.78, 20.77) * mm});
            skLineSegment(sketch, "E791", {"start": v(23.78, 20.77) * mm, "end": v(23.69, 20.88) * mm});
            skLineSegment(sketch, "E792", {"start": v(23.69, 20.88) * mm, "end": v(23.59, 21) * mm});
            skLineSegment(sketch, "E793", {"start": v(23.59, 21) * mm, "end": v(23.49, 21.05) * mm});
            skLineSegment(sketch, "E794", {"start": v(23.49, 21.05) * mm, "end": v(23.38, 21.02) * mm});
            skLineSegment(sketch, "E795", {"start": v(23.38, 21.02) * mm, "end": v(23.29, 20.97) * mm});
            skLineSegment(sketch, "E796", {"start": v(23.29, 20.97) * mm, "end": v(23.19, 20.92) * mm});
            skLineSegment(sketch, "E797", {"start": v(23.19, 20.92) * mm, "end": v(23.08, 20.89) * mm});
            skLineSegment(sketch, "E798", {"start": v(23.08, 20.89) * mm, "end": v(22.97, 20.87) * mm});
            skLineSegment(sketch, "E799", {"start": v(22.97, 20.87) * mm, "end": v(22.82, 20.88) * mm});
            skLineSegment(sketch, "E800", {"start": v(22.82, 20.88) * mm, "end": v(22.69, 20.92) * mm});
            skLineSegment(sketch, "E801", {"start": v(22.69, 20.92) * mm, "end": v(22.56, 20.99) * mm});
            skLineSegment(sketch, "E802", {"start": v(22.56, 20.99) * mm, "end": v(22.45, 21.08) * mm});
            skLineSegment(sketch, "E803", {"start": v(22.45, 21.08) * mm, "end": v(22.36, 21.2) * mm});
            skLineSegment(sketch, "E804", {"start": v(22.36, 21.2) * mm, "end": v(22.3, 21.33) * mm});
            skLineSegment(sketch, "E805", {"start": v(22.3, 21.33) * mm, "end": v(22.27, 21.47) * mm});
            skLineSegment(sketch, "E806", {"start": v(22.27, 21.47) * mm, "end": v(22.27, 21.61) * mm});
            skLineSegment(sketch, "E807", {"start": v(22.27, 21.61) * mm, "end": v(22.3, 21.72) * mm});
            skLineSegment(sketch, "E808", {"start": v(22.3, 21.72) * mm, "end": v(22.34, 21.83) * mm});
            skLineSegment(sketch, "E809", {"start": v(22.34, 21.83) * mm, "end": v(22.39, 21.92) * mm});
            skLineSegment(sketch, "E810", {"start": v(22.39, 21.92) * mm, "end": v(22.45, 22.01) * mm});
            skLineSegment(sketch, "E811", {"start": v(22.45, 22.01) * mm, "end": v(22.48, 22.12) * mm});
            skLineSegment(sketch, "E812", {"start": v(22.48, 22.12) * mm, "end": v(22.43, 22.22) * mm});
            skLineSegment(sketch, "E813", {"start": v(22.43, 22.22) * mm, "end": v(22.33, 22.33) * mm});
            skLineSegment(sketch, "E814", {"start": v(22.33, 22.33) * mm, "end": v(22.22, 22.43) * mm});
            skLineSegment(sketch, "E815", {"start": v(22.22, 22.43) * mm, "end": v(22.12, 22.48) * mm});
            skLineSegment(sketch, "E816", {"start": v(22.12, 22.48) * mm, "end": v(22.01, 22.45) * mm});
            skLineSegment(sketch, "E817", {"start": v(22.01, 22.45) * mm, "end": v(21.92, 22.39) * mm});
            skLineSegment(sketch, "E818", {"start": v(21.92, 22.39) * mm, "end": v(21.83, 22.34) * mm});
            skLineSegment(sketch, "E819", {"start": v(21.83, 22.34) * mm, "end": v(21.72, 22.3) * mm});
            skLineSegment(sketch, "E820", {"start": v(21.72, 22.3) * mm, "end": v(21.61, 22.27) * mm});
            skLineSegment(sketch, "E821", {"start": v(21.61, 22.27) * mm, "end": v(21.47, 22.27) * mm});
            skLineSegment(sketch, "E822", {"start": v(21.47, 22.27) * mm, "end": v(21.33, 22.3) * mm});
            skLineSegment(sketch, "E823", {"start": v(21.33, 22.3) * mm, "end": v(21.2, 22.36) * mm});
            skLineSegment(sketch, "E824", {"start": v(21.2, 22.36) * mm, "end": v(21.08, 22.45) * mm});
            skLineSegment(sketch, "E825", {"start": v(21.08, 22.45) * mm, "end": v(20.99, 22.56) * mm});
            skLineSegment(sketch, "E826", {"start": v(20.99, 22.56) * mm, "end": v(20.92, 22.69) * mm});
            skLineSegment(sketch, "E827", {"start": v(20.92, 22.69) * mm, "end": v(20.88, 22.82) * mm});
            skLineSegment(sketch, "E828", {"start": v(20.88, 22.82) * mm, "end": v(20.87, 22.97) * mm});
            skLineSegment(sketch, "E829", {"start": v(20.87, 22.97) * mm, "end": v(20.89, 23.08) * mm});
            skLineSegment(sketch, "E830", {"start": v(20.89, 23.08) * mm, "end": v(20.92, 23.19) * mm});
            skLineSegment(sketch, "E831", {"start": v(20.92, 23.19) * mm, "end": v(20.97, 23.29) * mm});
            skLineSegment(sketch, "E832", {"start": v(20.97, 23.29) * mm, "end": v(21.02, 23.38) * mm});
            skLineSegment(sketch, "E833", {"start": v(21.02, 23.38) * mm, "end": v(21.05, 23.49) * mm});
            skLineSegment(sketch, "E834", {"start": v(21.05, 23.49) * mm, "end": v(21, 23.59) * mm});
            skLineSegment(sketch, "E835", {"start": v(21, 23.59) * mm, "end": v(20.88, 23.69) * mm});
            skLineSegment(sketch, "E836", {"start": v(20.88, 23.69) * mm, "end": v(20.77, 23.78) * mm});
            skLineSegment(sketch, "E837", {"start": v(20.77, 23.78) * mm, "end": v(20.66, 23.82) * mm});
            skLineSegment(sketch, "E838", {"start": v(20.66, 23.82) * mm, "end": v(20.56, 23.79) * mm});
            skLineSegment(sketch, "E839", {"start": v(20.56, 23.79) * mm, "end": v(20.47, 23.72) * mm});
            skLineSegment(sketch, "E840", {"start": v(20.47, 23.72) * mm, "end": v(20.38, 23.66) * mm});
            skLineSegment(sketch, "E841", {"start": v(20.38, 23.66) * mm, "end": v(20.28, 23.62) * mm});
            skLineSegment(sketch, "E842", {"start": v(20.28, 23.62) * mm, "end": v(20.17, 23.58) * mm});
            skLineSegment(sketch, "E843", {"start": v(20.17, 23.58) * mm, "end": v(20.03, 23.57) * mm});
            skLineSegment(sketch, "E844", {"start": v(20.03, 23.57) * mm, "end": v(19.89, 23.6) * mm});
            skLineSegment(sketch, "E845", {"start": v(19.89, 23.6) * mm, "end": v(19.75, 23.65) * mm});
            skLineSegment(sketch, "E846", {"start": v(19.75, 23.65) * mm, "end": v(19.63, 23.73) * mm});
            skLineSegment(sketch, "E847", {"start": v(19.63, 23.73) * mm, "end": v(19.53, 23.84) * mm});
            skLineSegment(sketch, "E848", {"start": v(19.53, 23.84) * mm, "end": v(19.45, 23.96) * mm});
            skLineSegment(sketch, "E849", {"start": v(19.45, 23.96) * mm, "end": v(19.4, 24.09) * mm});
            skLineSegment(sketch, "E850", {"start": v(19.4, 24.09) * mm, "end": v(19.38, 24.23) * mm});
            skLineSegment(sketch, "E851", {"start": v(19.38, 24.23) * mm, "end": v(19.4, 24.34) * mm});
            skLineSegment(sketch, "E852", {"start": v(19.4, 24.34) * mm, "end": v(19.42, 24.45) * mm});
            skLineSegment(sketch, "E853", {"start": v(19.42, 24.45) * mm, "end": v(19.46, 24.56) * mm});
            skLineSegment(sketch, "E854", {"start": v(19.46, 24.56) * mm, "end": v(19.51, 24.65) * mm});
            skLineSegment(sketch, "E855", {"start": v(19.51, 24.65) * mm, "end": v(19.53, 24.76) * mm});
            skLineSegment(sketch, "E856", {"start": v(19.53, 24.76) * mm, "end": v(19.47, 24.86) * mm});
            skLineSegment(sketch, "E857", {"start": v(19.47, 24.86) * mm, "end": v(19.35, 24.95) * mm});
            skLineSegment(sketch, "E858", {"start": v(19.35, 24.95) * mm, "end": v(19.24, 25.04) * mm});
            skLineSegment(sketch, "E859", {"start": v(19.24, 25.04) * mm, "end": v(19.13, 25.08) * mm});
            skLineSegment(sketch, "E860", {"start": v(19.13, 25.08) * mm, "end": v(19.03, 25.03) * mm});
            skLineSegment(sketch, "E861", {"start": v(19.03, 25.03) * mm, "end": v(18.94, 24.96) * mm});
            skLineSegment(sketch, "E862", {"start": v(18.94, 24.96) * mm, "end": v(18.85, 24.9) * mm});
            skLineSegment(sketch, "E863", {"start": v(18.85, 24.9) * mm, "end": v(18.76, 24.84) * mm});
            skLineSegment(sketch, "E864", {"start": v(18.76, 24.84) * mm, "end": v(18.65, 24.8) * mm});
            skLineSegment(sketch, "E865", {"start": v(18.65, 24.8) * mm, "end": v(18.5, 24.78) * mm});
            skLineSegment(sketch, "E866", {"start": v(18.5, 24.78) * mm, "end": v(18.37, 24.8) * mm});
            skLineSegment(sketch, "E867", {"start": v(18.37, 24.8) * mm, "end": v(18.23, 24.85) * mm});
            skLineSegment(sketch, "E868", {"start": v(18.23, 24.85) * mm, "end": v(18.1, 24.92) * mm});
            skLineSegment(sketch, "E869", {"start": v(18.1, 24.92) * mm, "end": v(18, 25.02) * mm});
            skLineSegment(sketch, "E870", {"start": v(18, 25.02) * mm, "end": v(17.91, 25.13) * mm});
            skLineSegment(sketch, "E871", {"start": v(17.91, 25.13) * mm, "end": v(17.85, 25.26) * mm});
            skLineSegment(sketch, "E872", {"start": v(17.85, 25.26) * mm, "end": v(17.82, 25.4) * mm});
            skLineSegment(sketch, "E873", {"start": v(17.82, 25.4) * mm, "end": v(17.83, 25.51) * mm});
            skLineSegment(sketch, "E874", {"start": v(17.83, 25.51) * mm, "end": v(17.85, 25.62) * mm});
            skLineSegment(sketch, "E875", {"start": v(17.85, 25.62) * mm, "end": v(17.88, 25.73) * mm});
            skLineSegment(sketch, "E876", {"start": v(17.88, 25.73) * mm, "end": v(17.93, 25.83) * mm});
            skLineSegment(sketch, "E877", {"start": v(17.93, 25.83) * mm, "end": v(17.94, 25.94) * mm});
            skLineSegment(sketch, "E878", {"start": v(17.94, 25.94) * mm, "end": v(17.87, 26.03) * mm});
            skLineSegment(sketch, "E879", {"start": v(17.87, 26.03) * mm, "end": v(17.75, 26.12) * mm});
            skLineSegment(sketch, "E880", {"start": v(17.75, 26.12) * mm, "end": v(17.63, 26.2) * mm});
            skLineSegment(sketch, "E881", {"start": v(17.63, 26.2) * mm, "end": v(17.51, 26.23) * mm});
            skLineSegment(sketch, "E882", {"start": v(17.51, 26.23) * mm, "end": v(17.42, 26.18) * mm});
            skLineSegment(sketch, "E883", {"start": v(17.42, 26.18) * mm, "end": v(17.34, 26.1) * mm});
            skLineSegment(sketch, "E884", {"start": v(17.34, 26.1) * mm, "end": v(17.25, 26.03) * mm});
            skLineSegment(sketch, "E885", {"start": v(17.25, 26.03) * mm, "end": v(17.16, 25.97) * mm});
            skLineSegment(sketch, "E886", {"start": v(17.16, 25.97) * mm, "end": v(17.06, 25.92) * mm});
            skLineSegment(sketch, "E887", {"start": v(17.06, 25.92) * mm, "end": v(16.92, 25.9) * mm});
            skLineSegment(sketch, "E888", {"start": v(16.92, 25.9) * mm, "end": v(16.77, 25.9) * mm});
            skLineSegment(sketch, "E889", {"start": v(16.77, 25.9) * mm, "end": v(16.63, 25.94) * mm});
            skLineSegment(sketch, "E890", {"start": v(16.63, 25.94) * mm, "end": v(16.5, 26) * mm});
            skLineSegment(sketch, "E891", {"start": v(16.5, 26) * mm, "end": v(16.4, 26.1) * mm});
            skLineSegment(sketch, "E892", {"start": v(16.4, 26.1) * mm, "end": v(16.3, 26.2) * mm});
            skLineSegment(sketch, "E893", {"start": v(16.3, 26.2) * mm, "end": v(16.23, 26.33) * mm});
            skLineSegment(sketch, "E894", {"start": v(16.23, 26.33) * mm, "end": v(16.2, 26.47) * mm});
            skLineSegment(sketch, "E895", {"start": v(16.2, 26.47) * mm, "end": v(16.2, 26.58) * mm});
            skLineSegment(sketch, "E896", {"start": v(16.2, 26.58) * mm, "end": v(16.2, 26.7) * mm});
            skLineSegment(sketch, "E897", {"start": v(16.2, 26.7) * mm, "end": v(16.23, 26.8) * mm});
            skLineSegment(sketch, "E898", {"start": v(16.23, 26.8) * mm, "end": v(16.27, 26.9) * mm});
            skLineSegment(sketch, "E899", {"start": v(16.27, 26.9) * mm, "end": v(16.27, 27.01) * mm});
            skLineSegment(sketch, "E900", {"start": v(16.27, 27.01) * mm, "end": v(16.2, 27.1) * mm});
            skLineSegment(sketch, "E901", {"start": v(16.2, 27.1) * mm, "end": v(16.07, 27.18) * mm});
            skLineSegment(sketch, "E902", {"start": v(16.07, 27.18) * mm, "end": v(15.95, 27.25) * mm});
            skLineSegment(sketch, "E903", {"start": v(15.95, 27.25) * mm, "end": v(15.83, 27.27) * mm});
            skLineSegment(sketch, "E904", {"start": v(15.83, 27.27) * mm, "end": v(15.74, 27.22) * mm});
            skLineSegment(sketch, "E905", {"start": v(15.74, 27.22) * mm, "end": v(15.67, 27.14) * mm});
            skLineSegment(sketch, "E906", {"start": v(15.67, 27.14) * mm, "end": v(15.59, 27.06) * mm});
            skLineSegment(sketch, "E907", {"start": v(15.59, 27.06) * mm, "end": v(15.5, 27) * mm});
            skLineSegment(sketch, "E908", {"start": v(15.5, 27) * mm, "end": v(15.4, 26.94) * mm});
            skLineSegment(sketch, "E909", {"start": v(15.4, 26.94) * mm, "end": v(15.26, 26.9) * mm});
            skLineSegment(sketch, "E910", {"start": v(15.26, 26.9) * mm, "end": v(15.11, 26.9) * mm});
            skLineSegment(sketch, "E911", {"start": v(15.11, 26.9) * mm, "end": v(14.97, 26.93) * mm});
            skLineSegment(sketch, "E912", {"start": v(14.97, 26.93) * mm, "end": v(14.84, 27) * mm});
            skLineSegment(sketch, "E913", {"start": v(14.84, 27) * mm, "end": v(14.72, 27.07) * mm});
            skLineSegment(sketch, "E914", {"start": v(14.72, 27.07) * mm, "end": v(14.62, 27.18) * mm});
            skLineSegment(sketch, "E915", {"start": v(14.62, 27.18) * mm, "end": v(14.54, 27.3) * mm});
            skLineSegment(sketch, "E916", {"start": v(14.54, 27.3) * mm, "end": v(14.5, 27.43) * mm});
            skLineSegment(sketch, "E917", {"start": v(14.5, 27.43) * mm, "end": v(14.5, 27.55) * mm});
            skLineSegment(sketch, "E918", {"start": v(14.5, 27.55) * mm, "end": v(14.5, 27.66) * mm});
            skLineSegment(sketch, "E919", {"start": v(14.5, 27.66) * mm, "end": v(14.52, 27.77) * mm});
            skLineSegment(sketch, "E920", {"start": v(14.52, 27.77) * mm, "end": v(14.55, 27.87) * mm});
            skLineSegment(sketch, "E921", {"start": v(14.55, 27.87) * mm, "end": v(14.55, 27.98) * mm});
            skLineSegment(sketch, "E922", {"start": v(14.55, 27.98) * mm, "end": v(14.47, 28.07) * mm});
            skLineSegment(sketch, "E923", {"start": v(14.47, 28.07) * mm, "end": v(14.34, 28.14) * mm});
            skLineSegment(sketch, "E924", {"start": v(14.34, 28.14) * mm, "end": v(14.2, 28.2) * mm});
            skLineSegment(sketch, "E925", {"start": v(14.2, 28.2) * mm, "end": v(14.09, 28.21) * mm});
            skLineSegment(sketch, "E926", {"start": v(14.09, 28.21) * mm, "end": v(14, 28.15) * mm});
            skLineSegment(sketch, "E927", {"start": v(14, 28.15) * mm, "end": v(13.93, 28.07) * mm});
            skLineSegment(sketch, "E928", {"start": v(13.93, 28.07) * mm, "end": v(13.86, 27.99) * mm});
            skLineSegment(sketch, "E929", {"start": v(13.86, 27.99) * mm, "end": v(13.77, 27.92) * mm});
            skLineSegment(sketch, "E930", {"start": v(13.77, 27.92) * mm, "end": v(13.67, 27.86) * mm});
            skLineSegment(sketch, "E931", {"start": v(13.67, 27.86) * mm, "end": v(13.54, 27.81) * mm});
            skLineSegment(sketch, "E932", {"start": v(13.54, 27.81) * mm, "end": v(13.4, 27.8) * mm});
            skLineSegment(sketch, "E933", {"start": v(13.4, 27.8) * mm, "end": v(13.25, 27.82) * mm});
            skLineSegment(sketch, "E934", {"start": v(13.25, 27.82) * mm, "end": v(13.11, 27.87) * mm});
            skLineSegment(sketch, "E935", {"start": v(13.11, 27.87) * mm, "end": v(13, 27.94) * mm});
            skLineSegment(sketch, "E936", {"start": v(13, 27.94) * mm, "end": v(12.88, 28.04) * mm});
            skLineSegment(sketch, "E937", {"start": v(12.88, 28.04) * mm, "end": v(12.8, 28.16) * mm});
            skLineSegment(sketch, "E938", {"start": v(12.8, 28.16) * mm, "end": v(12.75, 28.3) * mm});
            skLineSegment(sketch, "E939", {"start": v(12.75, 28.3) * mm, "end": v(12.73, 28.4) * mm});
            skLineSegment(sketch, "E940", {"start": v(12.73, 28.4) * mm, "end": v(12.73, 28.52) * mm});
            skLineSegment(sketch, "E941", {"start": v(12.73, 28.52) * mm, "end": v(12.74, 28.62) * mm});
            skLineSegment(sketch, "E942", {"start": v(12.74, 28.62) * mm, "end": v(12.77, 28.73) * mm});
            skLineSegment(sketch, "E943", {"start": v(12.77, 28.73) * mm, "end": v(12.76, 28.84) * mm});
            skLineSegment(sketch, "E944", {"start": v(12.76, 28.84) * mm, "end": v(12.68, 28.92) * mm});
            skLineSegment(sketch, "E945", {"start": v(12.68, 28.92) * mm, "end": v(12.54, 28.98) * mm});
            skLineSegment(sketch, "E946", {"start": v(12.54, 28.98) * mm, "end": v(12.4, 29.04) * mm});
            skLineSegment(sketch, "E947", {"start": v(12.4, 29.04) * mm, "end": v(12.29, 29.04) * mm});
            skLineSegment(sketch, "E948", {"start": v(12.29, 29.04) * mm, "end": v(12.2, 28.98) * mm});
            skLineSegment(sketch, "E949", {"start": v(12.2, 28.98) * mm, "end": v(12.14, 28.89) * mm});
            skLineSegment(sketch, "E950", {"start": v(12.14, 28.89) * mm, "end": v(12.07, 28.8) * mm});
            skLineSegment(sketch, "E951", {"start": v(12.07, 28.8) * mm, "end": v(11.99, 28.73) * mm});
            skLineSegment(sketch, "E952", {"start": v(11.99, 28.73) * mm, "end": v(11.9, 28.66) * mm});
            skLineSegment(sketch, "E953", {"start": v(11.9, 28.66) * mm, "end": v(11.76, 28.6) * mm});
            skLineSegment(sketch, "E954", {"start": v(11.76, 28.6) * mm, "end": v(11.62, 28.59) * mm});
            skLineSegment(sketch, "E955", {"start": v(11.62, 28.59) * mm, "end": v(11.48, 28.6) * mm});
            skLineSegment(sketch, "E956", {"start": v(11.48, 28.6) * mm, "end": v(11.34, 28.64) * mm});
            skLineSegment(sketch, "E957", {"start": v(11.34, 28.64) * mm, "end": v(11.2, 28.7) * mm});
            skLineSegment(sketch, "E958", {"start": v(11.2, 28.7) * mm, "end": v(11.1, 28.8) * mm});
            skLineSegment(sketch, "E959", {"start": v(11.1, 28.8) * mm, "end": v(11, 28.9) * mm});
            skLineSegment(sketch, "E960", {"start": v(11, 28.9) * mm, "end": v(10.95, 29.04) * mm});
            skLineSegment(sketch, "E961", {"start": v(10.95, 29.04) * mm, "end": v(10.92, 29.15) * mm});
            skLineSegment(sketch, "E962", {"start": v(10.92, 29.15) * mm, "end": v(10.92, 29.26) * mm});
            skLineSegment(sketch, "E963", {"start": v(10.92, 29.26) * mm, "end": v(10.92, 29.37) * mm});
            skLineSegment(sketch, "E964", {"start": v(10.92, 29.37) * mm, "end": v(10.94, 29.48) * mm});
            skLineSegment(sketch, "E965", {"start": v(10.94, 29.48) * mm, "end": v(10.92, 29.58) * mm});
            skLineSegment(sketch, "E966", {"start": v(10.92, 29.58) * mm, "end": v(10.83, 29.66) * mm});
            skLineSegment(sketch, "E967", {"start": v(10.83, 29.66) * mm, "end": v(10.7, 29.71) * mm});
            skLineSegment(sketch, "E968", {"start": v(10.7, 29.71) * mm, "end": v(10.56, 29.76) * mm});
            skLineSegment(sketch, "E969", {"start": v(10.56, 29.76) * mm, "end": v(10.44, 29.76) * mm});
            skLineSegment(sketch, "E970", {"start": v(10.44, 29.76) * mm, "end": v(10.36, 29.69) * mm});
            skLineSegment(sketch, "E971", {"start": v(10.36, 29.69) * mm, "end": v(10.3, 29.6) * mm});
            skLineSegment(sketch, "E972", {"start": v(10.3, 29.6) * mm, "end": v(10.24, 29.5) * mm});
            skLineSegment(sketch, "E973", {"start": v(10.24, 29.5) * mm, "end": v(10.16, 29.42) * mm});
            skLineSegment(sketch, "E974", {"start": v(10.16, 29.42) * mm, "end": v(10.07, 29.35) * mm});
            skLineSegment(sketch, "E975", {"start": v(10.07, 29.35) * mm, "end": v(9.94, 29.29) * mm});
            skLineSegment(sketch, "E976", {"start": v(9.94, 29.29) * mm, "end": v(9.8, 29.26) * mm});
            skLineSegment(sketch, "E977", {"start": v(9.8, 29.26) * mm, "end": v(9.66, 29.26) * mm});
            skLineSegment(sketch, "E978", {"start": v(9.66, 29.26) * mm, "end": v(9.52, 29.3) * mm});
            skLineSegment(sketch, "E979", {"start": v(9.52, 29.3) * mm, "end": v(9.39, 29.35) * mm});
            skLineSegment(sketch, "E980", {"start": v(9.39, 29.35) * mm, "end": v(9.27, 29.44) * mm});
            skLineSegment(sketch, "E981", {"start": v(9.27, 29.44) * mm, "end": v(9.17, 29.54) * mm});
            skLineSegment(sketch, "E982", {"start": v(9.17, 29.54) * mm, "end": v(9.1, 29.67) * mm});
            skLineSegment(sketch, "E983", {"start": v(9.1, 29.67) * mm, "end": v(9.07, 29.78) * mm});
            skLineSegment(sketch, "E984", {"start": v(9.07, 29.78) * mm, "end": v(9.06, 29.89) * mm});
            skLineSegment(sketch, "E985", {"start": v(9.06, 29.89) * mm, "end": v(9.06, 30) * mm});
            skLineSegment(sketch, "E986", {"start": v(9.06, 30) * mm, "end": v(9.07, 30.1) * mm});
            skLineSegment(sketch, "E987", {"start": v(9.07, 30.1) * mm, "end": v(9.04, 30.21) * mm});
            skLineSegment(sketch, "E988", {"start": v(9.04, 30.21) * mm, "end": v(8.95, 30.28) * mm});
            skLineSegment(sketch, "E989", {"start": v(8.95, 30.28) * mm, "end": v(8.8, 30.32) * mm});
            skLineSegment(sketch, "E990", {"start": v(8.8, 30.32) * mm, "end": v(8.67, 30.36) * mm});
            skLineSegment(sketch, "E991", {"start": v(8.67, 30.36) * mm, "end": v(8.55, 30.36) * mm});
            skLineSegment(sketch, "E992", {"start": v(8.55, 30.36) * mm, "end": v(8.47, 30.28) * mm});
            skLineSegment(sketch, "E993", {"start": v(8.47, 30.28) * mm, "end": v(8.43, 30.18) * mm});
            skLineSegment(sketch, "E994", {"start": v(8.43, 30.18) * mm, "end": v(8.37, 30.09) * mm});
            skLineSegment(sketch, "E995", {"start": v(8.37, 30.09) * mm, "end": v(8.3, 30) * mm});
            skLineSegment(sketch, "E996", {"start": v(8.3, 30) * mm, "end": v(8.21, 29.92) * mm});
            skLineSegment(sketch, "E997", {"start": v(8.21, 29.92) * mm, "end": v(8.09, 29.86) * mm});
            skLineSegment(sketch, "E998", {"start": v(8.09, 29.86) * mm, "end": v(7.95, 29.82) * mm});
            skLineSegment(sketch, "E999", {"start": v(7.95, 29.82) * mm, "end": v(7.8, 29.81) * mm});
            skLineSegment(sketch, "E1000", {"start": v(7.8, 29.81) * mm, "end": v(7.66, 29.83) * mm});
            skLineSegment(sketch, "E1001", {"start": v(7.66, 29.83) * mm, "end": v(7.52, 29.88) * mm});
            skLineSegment(sketch, "E1002", {"start": v(7.52, 29.88) * mm, "end": v(7.4, 29.96) * mm});
            skLineSegment(sketch, "E1003", {"start": v(7.4, 29.96) * mm, "end": v(7.3, 30.06) * mm});
            skLineSegment(sketch, "E1004", {"start": v(7.3, 30.06) * mm, "end": v(7.22, 30.18) * mm});
            skLineSegment(sketch, "E1005", {"start": v(7.22, 30.18) * mm, "end": v(7.19, 30.29) * mm});
            skLineSegment(sketch, "E1006", {"start": v(7.19, 30.29) * mm, "end": v(7.16, 30.4) * mm});
            skLineSegment(sketch, "E1007", {"start": v(7.16, 30.4) * mm, "end": v(7.16, 30.5) * mm});
            skLineSegment(sketch, "E1008", {"start": v(7.16, 30.5) * mm, "end": v(7.16, 30.62) * mm});
            skLineSegment(sketch, "E1009", {"start": v(7.16, 30.62) * mm, "end": v(7.13, 30.72) * mm});
            skLineSegment(sketch, "E1010", {"start": v(7.13, 30.72) * mm, "end": v(7.03, 30.78) * mm});
            skLineSegment(sketch, "E1011", {"start": v(7.03, 30.78) * mm, "end": v(6.89, 30.82) * mm});
            skLineSegment(sketch, "E1012", {"start": v(6.89, 30.82) * mm, "end": v(6.74, 30.85) * mm});
            skLineSegment(sketch, "E1013", {"start": v(6.74, 30.85) * mm, "end": v(6.63, 30.83) * mm});
            skLineSegment(sketch, "E1014", {"start": v(6.63, 30.83) * mm, "end": v(6.56, 30.75) * mm});
            skLineSegment(sketch, "E1015", {"start": v(6.56, 30.75) * mm, "end": v(6.51, 30.65) * mm});
            skLineSegment(sketch, "E1016", {"start": v(6.51, 30.65) * mm, "end": v(6.46, 30.55) * mm});
            skLineSegment(sketch, "E1017", {"start": v(6.46, 30.55) * mm, "end": v(6.4, 30.46) * mm});
            skLineSegment(sketch, "E1018", {"start": v(6.4, 30.46) * mm, "end": v(6.32, 30.38) * mm});
            skLineSegment(sketch, "E1019", {"start": v(6.32, 30.38) * mm, "end": v(6.2, 30.3) * mm});
            skLineSegment(sketch, "E1020", {"start": v(6.2, 30.3) * mm, "end": v(6.06, 30.26) * mm});
            skLineSegment(sketch, "E1021", {"start": v(6.06, 30.26) * mm, "end": v(5.92, 30.24) * mm});
            skLineSegment(sketch, "E1022", {"start": v(5.92, 30.24) * mm, "end": v(5.77, 30.26) * mm});
            skLineSegment(sketch, "E1023", {"start": v(5.77, 30.26) * mm, "end": v(5.63, 30.3) * mm});
            skLineSegment(sketch, "E1024", {"start": v(5.63, 30.3) * mm, "end": v(5.5, 30.36) * mm});
            skLineSegment(sketch, "E1025", {"start": v(5.5, 30.36) * mm, "end": v(5.4, 30.46) * mm});
            skLineSegment(sketch, "E1026", {"start": v(5.4, 30.46) * mm, "end": v(5.31, 30.57) * mm});
            skLineSegment(sketch, "E1027", {"start": v(5.31, 30.57) * mm, "end": v(5.27, 30.68) * mm});
            skLineSegment(sketch, "E1028", {"start": v(5.27, 30.68) * mm, "end": v(5.24, 30.79) * mm});
            skLineSegment(sketch, "E1029", {"start": v(5.24, 30.79) * mm, "end": v(5.23, 30.9) * mm});
            skLineSegment(sketch, "E1030", {"start": v(5.23, 30.9) * mm, "end": v(5.22, 31) * mm});
            skLineSegment(sketch, "E1031", {"start": v(5.22, 31) * mm, "end": v(5.19, 31.1) * mm});
            skLineSegment(sketch, "E1032", {"start": v(5.19, 31.1) * mm, "end": v(5.08, 31.16) * mm});
            skLineSegment(sketch, "E1033", {"start": v(5.08, 31.16) * mm, "end": v(4.94, 31.19) * mm});
            skLineSegment(sketch, "E1034", {"start": v(4.94, 31.19) * mm, "end": v(4.8, 31.21) * mm});
            skLineSegment(sketch, "E1035", {"start": v(4.8, 31.21) * mm, "end": v(4.68, 31.19) * mm});
            skLineSegment(sketch, "E1036", {"start": v(4.68, 31.19) * mm, "end": v(4.61, 31.1) * mm});
            skLineSegment(sketch, "E1037", {"start": v(4.61, 31.1) * mm, "end": v(4.58, 31) * mm});
            skLineSegment(sketch, "E1038", {"start": v(4.58, 31) * mm, "end": v(4.53, 30.9) * mm});
            skLineSegment(sketch, "E1039", {"start": v(4.53, 30.9) * mm, "end": v(4.47, 30.8) * mm});
            skLineSegment(sketch, "E1040", {"start": v(4.47, 30.8) * mm, "end": v(4.4, 30.72) * mm});
            skLineSegment(sketch, "E1041", {"start": v(4.4, 30.72) * mm, "end": v(4.28, 30.63) * mm});
            skLineSegment(sketch, "E1042", {"start": v(4.28, 30.63) * mm, "end": v(4.15, 30.58) * mm});
            skLineSegment(sketch, "E1043", {"start": v(4.15, 30.58) * mm, "end": v(4, 30.55) * mm});
            skLineSegment(sketch, "E1044", {"start": v(4, 30.55) * mm, "end": v(3.86, 30.56) * mm});
            skLineSegment(sketch, "E1045", {"start": v(3.86, 30.56) * mm, "end": v(3.72, 30.6) * mm});
            skLineSegment(sketch, "E1046", {"start": v(3.72, 30.6) * mm, "end": v(3.59, 30.65) * mm});
            skLineSegment(sketch, "E1047", {"start": v(3.59, 30.65) * mm, "end": v(3.47, 30.74) * mm});
            skLineSegment(sketch, "E1048", {"start": v(3.47, 30.74) * mm, "end": v(3.38, 30.85) * mm});
            skLineSegment(sketch, "E1049", {"start": v(3.38, 30.85) * mm, "end": v(3.33, 30.95) * mm});
            skLineSegment(sketch, "E1050", {"start": v(3.33, 30.95) * mm, "end": v(3.3, 31.05) * mm});
            skLineSegment(sketch, "E1051", {"start": v(3.3, 31.05) * mm, "end": v(3.28, 31.16) * mm});
            skLineSegment(sketch, "E1052", {"start": v(3.28, 31.16) * mm, "end": v(3.27, 31.27) * mm});
            skLineSegment(sketch, "E1053", {"start": v(3.27, 31.27) * mm, "end": v(3.22, 31.37) * mm});
            skLineSegment(sketch, "E1054", {"start": v(3.22, 31.37) * mm, "end": v(3.12, 31.42) * mm});
            skLineSegment(sketch, "E1055", {"start": v(3.12, 31.42) * mm, "end": v(2.97, 31.44) * mm});
            skLineSegment(sketch, "E1056", {"start": v(2.97, 31.44) * mm, "end": v(2.83, 31.45) * mm});
            skLineSegment(sketch, "E1057", {"start": v(2.83, 31.45) * mm, "end": v(2.71, 31.42) * mm});
            skLineSegment(sketch, "E1058", {"start": v(2.71, 31.42) * mm, "end": v(2.65, 31.33) * mm});
            skLineSegment(sketch, "E1059", {"start": v(2.65, 31.33) * mm, "end": v(2.62, 31.22) * mm});
            skLineSegment(sketch, "E1060", {"start": v(2.62, 31.22) * mm, "end": v(2.58, 31.12) * mm});
            skLineSegment(sketch, "E1061", {"start": v(2.58, 31.12) * mm, "end": v(2.53, 31.02) * mm});
            skLineSegment(sketch, "E1062", {"start": v(2.53, 31.02) * mm, "end": v(2.46, 30.93) * mm});
            skLineSegment(sketch, "E1063", {"start": v(2.46, 30.93) * mm, "end": v(2.35, 30.84) * mm});
            skLineSegment(sketch, "E1064", {"start": v(2.35, 30.84) * mm, "end": v(2.22, 30.78) * mm});
            skLineSegment(sketch, "E1065", {"start": v(2.22, 30.78) * mm, "end": v(2.08, 30.75) * mm});
            skLineSegment(sketch, "E1066", {"start": v(2.08, 30.75) * mm, "end": v(1.93, 30.74) * mm});
            skLineSegment(sketch, "E1067", {"start": v(1.93, 30.74) * mm, "end": v(1.8, 30.76) * mm});
            skLineSegment(sketch, "E1068", {"start": v(1.8, 30.76) * mm, "end": v(1.66, 30.82) * mm});
            skLineSegment(sketch, "E1069", {"start": v(1.66, 30.82) * mm, "end": v(1.54, 30.9) * mm});
            skLineSegment(sketch, "E1070", {"start": v(1.54, 30.9) * mm, "end": v(1.44, 31) * mm});
            skLineSegment(sketch, "E1071", {"start": v(1.44, 31) * mm, "end": v(1.38, 31.1) * mm});
            skLineSegment(sketch, "E1072", {"start": v(1.38, 31.1) * mm, "end": v(1.34, 31.2) * mm});
            skLineSegment(sketch, "E1073", {"start": v(1.34, 31.2) * mm, "end": v(1.31, 31.3) * mm});
            skLineSegment(sketch, "E1074", {"start": v(1.31, 31.3) * mm, "end": v(1.3, 31.42) * mm});
            skLineSegment(sketch, "E1075", {"start": v(1.3, 31.42) * mm, "end": v(1.25, 31.51) * mm});
            skLineSegment(sketch, "E1076", {"start": v(1.25, 31.51) * mm, "end": v(1.14, 31.56) * mm});
            skLineSegment(sketch, "E1077", {"start": v(1.14, 31.56) * mm, "end": v(1, 31.56) * mm});
            skLineSegment(sketch, "E1078", {"start": v(1, 31.56) * mm, "end": v(0.84, 31.56) * mm});
            skLineSegment(sketch, "E1079", {"start": v(0.84, 31.56) * mm, "end": v(0.73, 31.53) * mm});
            skLineSegment(sketch, "E1080", {"start": v(0.73, 31.53) * mm, "end": v(0.68, 31.44) * mm});
            skLineSegment(sketch, "E1081", {"start": v(0.68, 31.44) * mm, "end": v(0.66, 31.33) * mm});
            skLineSegment(sketch, "E1082", {"start": v(0.66, 31.33) * mm, "end": v(0.62, 31.22) * mm});
            skLineSegment(sketch, "E1083", {"start": v(0.62, 31.22) * mm, "end": v(0.57, 31.12) * mm});
            skLineSegment(sketch, "E1084", {"start": v(0.57, 31.12) * mm, "end": v(0.51, 31.03) * mm});
            skLineSegment(sketch, "E1085", {"start": v(0.51, 31.03) * mm, "end": v(0.4, 30.93) * mm});
            skLineSegment(sketch, "E1086", {"start": v(0.4, 30.93) * mm, "end": v(0.28, 30.86) * mm});
            skLineSegment(sketch, "E1087", {"start": v(0.28, 30.86) * mm, "end": v(0.14, 30.82) * mm});
            skLineSegment(sketch, "E1088", {"start": v(0.14, 30.82) * mm, "end": v(0, 30.8) * mm});
            skLineSegment(sketch, "E1089", {"start": v(0, 30.8) * mm, "end": v(-0.14, 30.82) * mm});
            skLineSegment(sketch, "E1090", {"start": v(-0.14, 30.82) * mm, "end": v(-0.28, 30.86) * mm});
            skLineSegment(sketch, "E1091", {"start": v(-0.28, 30.86) * mm, "end": v(-0.4, 30.93) * mm});
            skLineSegment(sketch, "E1092", {"start": v(-0.4, 30.93) * mm, "end": v(-0.51, 31.03) * mm});
            skLineSegment(sketch, "E1093", {"start": v(-0.51, 31.03) * mm, "end": v(-0.57, 31.12) * mm});
            skLineSegment(sketch, "E1094", {"start": v(-0.57, 31.12) * mm, "end": v(-0.62, 31.22) * mm});
            skLineSegment(sketch, "E1095", {"start": v(-0.62, 31.22) * mm, "end": v(-0.66, 31.33) * mm});
            skLineSegment(sketch, "E1096", {"start": v(-0.66, 31.33) * mm, "end": v(-0.68, 31.44) * mm});
            skLineSegment(sketch, "E1097", {"start": v(-0.68, 31.44) * mm, "end": v(-0.73, 31.53) * mm});
            skLineSegment(sketch, "E1098", {"start": v(-0.73, 31.53) * mm, "end": v(-0.84, 31.56) * mm});
            skLineSegment(sketch, "E1099", {"start": v(-0.84, 31.56) * mm, "end": v(-1, 31.56) * mm});
            skLineSegment(sketch, "E1100", {"start": v(-1, 31.56) * mm, "end": v(-1.14, 31.56) * mm});
            skLineSegment(sketch, "E1101", {"start": v(-1.14, 31.56) * mm, "end": v(-1.25, 31.51) * mm});
            skLineSegment(sketch, "E1102", {"start": v(-1.25, 31.51) * mm, "end": v(-1.3, 31.42) * mm});
            skLineSegment(sketch, "E1103", {"start": v(-1.3, 31.42) * mm, "end": v(-1.31, 31.3) * mm});
            skLineSegment(sketch, "E1104", {"start": v(-1.31, 31.3) * mm, "end": v(-1.34, 31.2) * mm});
            skLineSegment(sketch, "E1105", {"start": v(-1.34, 31.2) * mm, "end": v(-1.38, 31.1) * mm});
            skLineSegment(sketch, "E1106", {"start": v(-1.38, 31.1) * mm, "end": v(-1.44, 31) * mm});
            skLineSegment(sketch, "E1107", {"start": v(-1.44, 31) * mm, "end": v(-1.54, 30.9) * mm});
            skLineSegment(sketch, "E1108", {"start": v(-1.54, 30.9) * mm, "end": v(-1.66, 30.82) * mm});
            skLineSegment(sketch, "E1109", {"start": v(-1.66, 30.82) * mm, "end": v(-1.8, 30.76) * mm});
            skLineSegment(sketch, "E1110", {"start": v(-1.8, 30.76) * mm, "end": v(-1.93, 30.74) * mm});
            skLineSegment(sketch, "E1111", {"start": v(-1.93, 30.74) * mm, "end": v(-2.08, 30.75) * mm});
            skLineSegment(sketch, "E1112", {"start": v(-2.08, 30.75) * mm, "end": v(-2.22, 30.78) * mm});
            skLineSegment(sketch, "E1113", {"start": v(-2.22, 30.78) * mm, "end": v(-2.35, 30.84) * mm});
            skLineSegment(sketch, "E1114", {"start": v(-2.35, 30.84) * mm, "end": v(-2.46, 30.93) * mm});
            skLineSegment(sketch, "E1115", {"start": v(-2.46, 30.93) * mm, "end": v(-2.53, 31.02) * mm});
            skLineSegment(sketch, "E1116", {"start": v(-2.53, 31.02) * mm, "end": v(-2.58, 31.12) * mm});
            skLineSegment(sketch, "E1117", {"start": v(-2.58, 31.12) * mm, "end": v(-2.62, 31.22) * mm});
            skLineSegment(sketch, "E1118", {"start": v(-2.62, 31.22) * mm, "end": v(-2.65, 31.33) * mm});
            skLineSegment(sketch, "E1119", {"start": v(-2.65, 31.33) * mm, "end": v(-2.71, 31.42) * mm});
            skLineSegment(sketch, "E1120", {"start": v(-2.71, 31.42) * mm, "end": v(-2.83, 31.45) * mm});
            skLineSegment(sketch, "E1121", {"start": v(-2.83, 31.45) * mm, "end": v(-2.97, 31.44) * mm});
            skLineSegment(sketch, "E1122", {"start": v(-2.97, 31.44) * mm, "end": v(-3.12, 31.42) * mm});
            skLineSegment(sketch, "E1123", {"start": v(-3.12, 31.42) * mm, "end": v(-3.22, 31.37) * mm});
            skLineSegment(sketch, "E1124", {"start": v(-3.22, 31.37) * mm, "end": v(-3.27, 31.27) * mm});
            skLineSegment(sketch, "E1125", {"start": v(-3.27, 31.27) * mm, "end": v(-3.28, 31.16) * mm});
            skLineSegment(sketch, "E1126", {"start": v(-3.28, 31.16) * mm, "end": v(-3.3, 31.05) * mm});
            skLineSegment(sketch, "E1127", {"start": v(-3.3, 31.05) * mm, "end": v(-3.33, 30.95) * mm});
            skLineSegment(sketch, "E1128", {"start": v(-3.33, 30.95) * mm, "end": v(-3.38, 30.85) * mm});
            skLineSegment(sketch, "E1129", {"start": v(-3.38, 30.85) * mm, "end": v(-3.47, 30.74) * mm});
            skLineSegment(sketch, "E1130", {"start": v(-3.47, 30.74) * mm, "end": v(-3.59, 30.65) * mm});
            skLineSegment(sketch, "E1131", {"start": v(-3.59, 30.65) * mm, "end": v(-3.72, 30.6) * mm});
            skLineSegment(sketch, "E1132", {"start": v(-3.72, 30.6) * mm, "end": v(-3.86, 30.56) * mm});
            skLineSegment(sketch, "E1133", {"start": v(-3.86, 30.56) * mm, "end": v(-4, 30.55) * mm});
            skLineSegment(sketch, "E1134", {"start": v(-4, 30.55) * mm, "end": v(-4.15, 30.58) * mm});
            skLineSegment(sketch, "E1135", {"start": v(-4.15, 30.58) * mm, "end": v(-4.28, 30.63) * mm});
            skLineSegment(sketch, "E1136", {"start": v(-4.28, 30.63) * mm, "end": v(-4.4, 30.72) * mm});
            skLineSegment(sketch, "E1137", {"start": v(-4.4, 30.72) * mm, "end": v(-4.47, 30.8) * mm});
            skLineSegment(sketch, "E1138", {"start": v(-4.47, 30.8) * mm, "end": v(-4.53, 30.9) * mm});
            skLineSegment(sketch, "E1139", {"start": v(-4.53, 30.9) * mm, "end": v(-4.58, 31) * mm});
            skLineSegment(sketch, "E1140", {"start": v(-4.58, 31) * mm, "end": v(-4.61, 31.1) * mm});
            skLineSegment(sketch, "E1141", {"start": v(-4.61, 31.1) * mm, "end": v(-4.68, 31.19) * mm});
            skLineSegment(sketch, "E1142", {"start": v(-4.68, 31.19) * mm, "end": v(-4.8, 31.21) * mm});
            skLineSegment(sketch, "E1143", {"start": v(-4.8, 31.21) * mm, "end": v(-4.94, 31.19) * mm});
            skLineSegment(sketch, "E1144", {"start": v(-4.94, 31.19) * mm, "end": v(-5.08, 31.16) * mm});
            skLineSegment(sketch, "E1145", {"start": v(-5.08, 31.16) * mm, "end": v(-5.19, 31.1) * mm});
            skLineSegment(sketch, "E1146", {"start": v(-5.19, 31.1) * mm, "end": v(-5.22, 31) * mm});
            skLineSegment(sketch, "E1147", {"start": v(-5.22, 31) * mm, "end": v(-5.23, 30.9) * mm});
            skLineSegment(sketch, "E1148", {"start": v(-5.23, 30.9) * mm, "end": v(-5.24, 30.79) * mm});
            skLineSegment(sketch, "E1149", {"start": v(-5.24, 30.79) * mm, "end": v(-5.27, 30.68) * mm});
            skLineSegment(sketch, "E1150", {"start": v(-5.27, 30.68) * mm, "end": v(-5.31, 30.57) * mm});
            skLineSegment(sketch, "E1151", {"start": v(-5.31, 30.57) * mm, "end": v(-5.4, 30.46) * mm});
            skLineSegment(sketch, "E1152", {"start": v(-5.4, 30.46) * mm, "end": v(-5.5, 30.36) * mm});
            skLineSegment(sketch, "E1153", {"start": v(-5.5, 30.36) * mm, "end": v(-5.63, 30.3) * mm});
            skLineSegment(sketch, "E1154", {"start": v(-5.63, 30.3) * mm, "end": v(-5.77, 30.26) * mm});
            skLineSegment(sketch, "E1155", {"start": v(-5.77, 30.26) * mm, "end": v(-5.92, 30.24) * mm});
            skLineSegment(sketch, "E1156", {"start": v(-5.92, 30.24) * mm, "end": v(-6.06, 30.26) * mm});
            skLineSegment(sketch, "E1157", {"start": v(-6.06, 30.26) * mm, "end": v(-6.2, 30.3) * mm});
            skLineSegment(sketch, "E1158", {"start": v(-6.2, 30.3) * mm, "end": v(-6.32, 30.38) * mm});
            skLineSegment(sketch, "E1159", {"start": v(-6.32, 30.38) * mm, "end": v(-6.4, 30.46) * mm});
            skLineSegment(sketch, "E1160", {"start": v(-6.4, 30.46) * mm, "end": v(-6.46, 30.55) * mm});
            skLineSegment(sketch, "E1161", {"start": v(-6.46, 30.55) * mm, "end": v(-6.51, 30.65) * mm});
            skLineSegment(sketch, "E1162", {"start": v(-6.51, 30.65) * mm, "end": v(-6.56, 30.75) * mm});
            skLineSegment(sketch, "E1163", {"start": v(-6.56, 30.75) * mm, "end": v(-6.63, 30.83) * mm});
            skLineSegment(sketch, "E1164", {"start": v(-6.63, 30.83) * mm, "end": v(-6.74, 30.85) * mm});
            skLineSegment(sketch, "E1165", {"start": v(-6.74, 30.85) * mm, "end": v(-6.89, 30.82) * mm});
            skLineSegment(sketch, "E1166", {"start": v(-6.89, 30.82) * mm, "end": v(-7.03, 30.78) * mm});
            skLineSegment(sketch, "E1167", {"start": v(-7.03, 30.78) * mm, "end": v(-7.13, 30.72) * mm});
            skLineSegment(sketch, "E1168", {"start": v(-7.13, 30.72) * mm, "end": v(-7.16, 30.62) * mm});
            skLineSegment(sketch, "E1169", {"start": v(-7.16, 30.62) * mm, "end": v(-7.16, 30.5) * mm});
            skLineSegment(sketch, "E1170", {"start": v(-7.16, 30.5) * mm, "end": v(-7.16, 30.4) * mm});
            skLineSegment(sketch, "E1171", {"start": v(-7.16, 30.4) * mm, "end": v(-7.19, 30.29) * mm});
            skLineSegment(sketch, "E1172", {"start": v(-7.19, 30.29) * mm, "end": v(-7.22, 30.18) * mm});
            skLineSegment(sketch, "E1173", {"start": v(-7.22, 30.18) * mm, "end": v(-7.3, 30.06) * mm});
            skLineSegment(sketch, "E1174", {"start": v(-7.3, 30.06) * mm, "end": v(-7.4, 29.96) * mm});
            skLineSegment(sketch, "E1175", {"start": v(-7.4, 29.96) * mm, "end": v(-7.52, 29.88) * mm});
            skLineSegment(sketch, "E1176", {"start": v(-7.52, 29.88) * mm, "end": v(-7.66, 29.83) * mm});
            skLineSegment(sketch, "E1177", {"start": v(-7.66, 29.83) * mm, "end": v(-7.8, 29.81) * mm});
            skLineSegment(sketch, "E1178", {"start": v(-7.8, 29.81) * mm, "end": v(-7.95, 29.82) * mm});
            skLineSegment(sketch, "E1179", {"start": v(-7.95, 29.82) * mm, "end": v(-8.09, 29.86) * mm});
            skLineSegment(sketch, "E1180", {"start": v(-8.09, 29.86) * mm, "end": v(-8.21, 29.92) * mm});
            skLineSegment(sketch, "E1181", {"start": v(-8.21, 29.92) * mm, "end": v(-8.3, 30) * mm});
            skLineSegment(sketch, "E1182", {"start": v(-8.3, 30) * mm, "end": v(-8.37, 30.09) * mm});
            skLineSegment(sketch, "E1183", {"start": v(-8.37, 30.09) * mm, "end": v(-8.43, 30.18) * mm});
            skLineSegment(sketch, "E1184", {"start": v(-8.43, 30.18) * mm, "end": v(-8.47, 30.28) * mm});
            skLineSegment(sketch, "E1185", {"start": v(-8.47, 30.28) * mm, "end": v(-8.55, 30.36) * mm});
            skLineSegment(sketch, "E1186", {"start": v(-8.55, 30.36) * mm, "end": v(-8.67, 30.36) * mm});
            skLineSegment(sketch, "E1187", {"start": v(-8.67, 30.36) * mm, "end": v(-8.8, 30.32) * mm});
            skLineSegment(sketch, "E1188", {"start": v(-8.8, 30.32) * mm, "end": v(-8.95, 30.28) * mm});
            skLineSegment(sketch, "E1189", {"start": v(-8.95, 30.28) * mm, "end": v(-9.04, 30.21) * mm});
            skLineSegment(sketch, "E1190", {"start": v(-9.04, 30.21) * mm, "end": v(-9.07, 30.1) * mm});
            skLineSegment(sketch, "E1191", {"start": v(-9.07, 30.1) * mm, "end": v(-9.06, 30) * mm});
            skLineSegment(sketch, "E1192", {"start": v(-9.06, 30) * mm, "end": v(-9.06, 29.89) * mm});
            skLineSegment(sketch, "E1193", {"start": v(-9.06, 29.89) * mm, "end": v(-9.07, 29.78) * mm});
            skLineSegment(sketch, "E1194", {"start": v(-9.07, 29.78) * mm, "end": v(-9.1, 29.67) * mm});
            skLineSegment(sketch, "E1195", {"start": v(-9.1, 29.67) * mm, "end": v(-9.17, 29.54) * mm});
            skLineSegment(sketch, "E1196", {"start": v(-9.17, 29.54) * mm, "end": v(-9.27, 29.44) * mm});
            skLineSegment(sketch, "E1197", {"start": v(-9.27, 29.44) * mm, "end": v(-9.39, 29.35) * mm});
            skLineSegment(sketch, "E1198", {"start": v(-9.39, 29.35) * mm, "end": v(-9.52, 29.3) * mm});
            skLineSegment(sketch, "E1199", {"start": v(-9.52, 29.3) * mm, "end": v(-9.66, 29.26) * mm});
            skLineSegment(sketch, "E1200", {"start": v(-9.66, 29.26) * mm, "end": v(-9.8, 29.26) * mm});
            skLineSegment(sketch, "E1201", {"start": v(-9.8, 29.26) * mm, "end": v(-9.94, 29.29) * mm});
            skLineSegment(sketch, "E1202", {"start": v(-9.94, 29.29) * mm, "end": v(-10.07, 29.35) * mm});
            skLineSegment(sketch, "E1203", {"start": v(-10.07, 29.35) * mm, "end": v(-10.16, 29.42) * mm});
            skLineSegment(sketch, "E1204", {"start": v(-10.16, 29.42) * mm, "end": v(-10.24, 29.5) * mm});
            skLineSegment(sketch, "E1205", {"start": v(-10.24, 29.5) * mm, "end": v(-10.3, 29.6) * mm});
            skLineSegment(sketch, "E1206", {"start": v(-10.3, 29.6) * mm, "end": v(-10.36, 29.69) * mm});
            skLineSegment(sketch, "E1207", {"start": v(-10.36, 29.69) * mm, "end": v(-10.44, 29.76) * mm});
            skLineSegment(sketch, "E1208", {"start": v(-10.44, 29.76) * mm, "end": v(-10.56, 29.76) * mm});
            skLineSegment(sketch, "E1209", {"start": v(-10.56, 29.76) * mm, "end": v(-10.7, 29.71) * mm});
            skLineSegment(sketch, "E1210", {"start": v(-10.7, 29.71) * mm, "end": v(-10.83, 29.66) * mm});
            skLineSegment(sketch, "E1211", {"start": v(-10.83, 29.66) * mm, "end": v(-10.92, 29.58) * mm});
            skLineSegment(sketch, "E1212", {"start": v(-10.92, 29.58) * mm, "end": v(-10.94, 29.48) * mm});
            skLineSegment(sketch, "E1213", {"start": v(-10.94, 29.48) * mm, "end": v(-10.92, 29.37) * mm});
            skLineSegment(sketch, "E1214", {"start": v(-10.92, 29.37) * mm, "end": v(-10.92, 29.26) * mm});
            skLineSegment(sketch, "E1215", {"start": v(-10.92, 29.26) * mm, "end": v(-10.92, 29.15) * mm});
            skLineSegment(sketch, "E1216", {"start": v(-10.92, 29.15) * mm, "end": v(-10.95, 29.04) * mm});
            skLineSegment(sketch, "E1217", {"start": v(-10.95, 29.04) * mm, "end": v(-11, 28.9) * mm});
            skLineSegment(sketch, "E1218", {"start": v(-11, 28.9) * mm, "end": v(-11.1, 28.8) * mm});
            skLineSegment(sketch, "E1219", {"start": v(-11.1, 28.8) * mm, "end": v(-11.2, 28.7) * mm});
            skLineSegment(sketch, "E1220", {"start": v(-11.2, 28.7) * mm, "end": v(-11.34, 28.64) * mm});
            skLineSegment(sketch, "E1221", {"start": v(-11.34, 28.64) * mm, "end": v(-11.48, 28.6) * mm});
            skLineSegment(sketch, "E1222", {"start": v(-11.48, 28.6) * mm, "end": v(-11.62, 28.59) * mm});
            skLineSegment(sketch, "E1223", {"start": v(-11.62, 28.59) * mm, "end": v(-11.76, 28.6) * mm});
            skLineSegment(sketch, "E1224", {"start": v(-11.76, 28.6) * mm, "end": v(-11.9, 28.66) * mm});
            skLineSegment(sketch, "E1225", {"start": v(-11.9, 28.66) * mm, "end": v(-11.99, 28.73) * mm});
            skLineSegment(sketch, "E1226", {"start": v(-11.99, 28.73) * mm, "end": v(-12.07, 28.8) * mm});
            skLineSegment(sketch, "E1227", {"start": v(-12.07, 28.8) * mm, "end": v(-12.14, 28.89) * mm});
            skLineSegment(sketch, "E1228", {"start": v(-12.14, 28.89) * mm, "end": v(-12.2, 28.98) * mm});
            skLineSegment(sketch, "E1229", {"start": v(-12.2, 28.98) * mm, "end": v(-12.29, 29.04) * mm});
            skLineSegment(sketch, "E1230", {"start": v(-12.29, 29.04) * mm, "end": v(-12.4, 29.04) * mm});
            skLineSegment(sketch, "E1231", {"start": v(-12.4, 29.04) * mm, "end": v(-12.54, 28.98) * mm});
            skLineSegment(sketch, "E1232", {"start": v(-12.54, 28.98) * mm, "end": v(-12.68, 28.92) * mm});
            skLineSegment(sketch, "E1233", {"start": v(-12.68, 28.92) * mm, "end": v(-12.76, 28.84) * mm});
            skLineSegment(sketch, "E1234", {"start": v(-12.76, 28.84) * mm, "end": v(-12.77, 28.73) * mm});
            skLineSegment(sketch, "E1235", {"start": v(-12.77, 28.73) * mm, "end": v(-12.74, 28.62) * mm});
            skLineSegment(sketch, "E1236", {"start": v(-12.74, 28.62) * mm, "end": v(-12.73, 28.52) * mm});
            skLineSegment(sketch, "E1237", {"start": v(-12.73, 28.52) * mm, "end": v(-12.73, 28.4) * mm});
            skLineSegment(sketch, "E1238", {"start": v(-12.73, 28.4) * mm, "end": v(-12.75, 28.3) * mm});
            skLineSegment(sketch, "E1239", {"start": v(-12.75, 28.3) * mm, "end": v(-12.8, 28.16) * mm});
            skLineSegment(sketch, "E1240", {"start": v(-12.8, 28.16) * mm, "end": v(-12.88, 28.04) * mm});
            skLineSegment(sketch, "E1241", {"start": v(-12.88, 28.04) * mm, "end": v(-13, 27.94) * mm});
            skLineSegment(sketch, "E1242", {"start": v(-13, 27.94) * mm, "end": v(-13.11, 27.87) * mm});
            skLineSegment(sketch, "E1243", {"start": v(-13.11, 27.87) * mm, "end": v(-13.25, 27.82) * mm});
            skLineSegment(sketch, "E1244", {"start": v(-13.25, 27.82) * mm, "end": v(-13.4, 27.8) * mm});
            skLineSegment(sketch, "E1245", {"start": v(-13.4, 27.8) * mm, "end": v(-13.54, 27.81) * mm});
            skLineSegment(sketch, "E1246", {"start": v(-13.54, 27.81) * mm, "end": v(-13.67, 27.86) * mm});
            skLineSegment(sketch, "E1247", {"start": v(-13.67, 27.86) * mm, "end": v(-13.77, 27.92) * mm});
            skLineSegment(sketch, "E1248", {"start": v(-13.77, 27.92) * mm, "end": v(-13.86, 27.99) * mm});
            skLineSegment(sketch, "E1249", {"start": v(-13.86, 27.99) * mm, "end": v(-13.93, 28.07) * mm});
            skLineSegment(sketch, "E1250", {"start": v(-13.93, 28.07) * mm, "end": v(-14, 28.15) * mm});
            skLineSegment(sketch, "E1251", {"start": v(-14, 28.15) * mm, "end": v(-14.09, 28.21) * mm});
            skLineSegment(sketch, "E1252", {"start": v(-14.09, 28.21) * mm, "end": v(-14.2, 28.2) * mm});
            skLineSegment(sketch, "E1253", {"start": v(-14.2, 28.2) * mm, "end": v(-14.34, 28.14) * mm});
            skLineSegment(sketch, "E1254", {"start": v(-14.34, 28.14) * mm, "end": v(-14.47, 28.07) * mm});
            skLineSegment(sketch, "E1255", {"start": v(-14.47, 28.07) * mm, "end": v(-14.55, 27.98) * mm});
            skLineSegment(sketch, "E1256", {"start": v(-14.55, 27.98) * mm, "end": v(-14.55, 27.87) * mm});
            skLineSegment(sketch, "E1257", {"start": v(-14.55, 27.87) * mm, "end": v(-14.52, 27.77) * mm});
            skLineSegment(sketch, "E1258", {"start": v(-14.52, 27.77) * mm, "end": v(-14.5, 27.66) * mm});
            skLineSegment(sketch, "E1259", {"start": v(-14.5, 27.66) * mm, "end": v(-14.5, 27.55) * mm});
            skLineSegment(sketch, "E1260", {"start": v(-14.5, 27.55) * mm, "end": v(-14.5, 27.43) * mm});
            skLineSegment(sketch, "E1261", {"start": v(-14.5, 27.43) * mm, "end": v(-14.54, 27.3) * mm});
            skLineSegment(sketch, "E1262", {"start": v(-14.54, 27.3) * mm, "end": v(-14.62, 27.18) * mm});
            skLineSegment(sketch, "E1263", {"start": v(-14.62, 27.18) * mm, "end": v(-14.72, 27.07) * mm});
            skLineSegment(sketch, "E1264", {"start": v(-14.72, 27.07) * mm, "end": v(-14.84, 27) * mm});
            skLineSegment(sketch, "E1265", {"start": v(-14.84, 27) * mm, "end": v(-14.97, 26.93) * mm});
            skLineSegment(sketch, "E1266", {"start": v(-14.97, 26.93) * mm, "end": v(-15.11, 26.9) * mm});
            skLineSegment(sketch, "E1267", {"start": v(-15.11, 26.9) * mm, "end": v(-15.26, 26.9) * mm});
            skLineSegment(sketch, "E1268", {"start": v(-15.26, 26.9) * mm, "end": v(-15.4, 26.94) * mm});
            skLineSegment(sketch, "E1269", {"start": v(-15.4, 26.94) * mm, "end": v(-15.5, 27) * mm});
            skLineSegment(sketch, "E1270", {"start": v(-15.5, 27) * mm, "end": v(-15.59, 27.06) * mm});
            skLineSegment(sketch, "E1271", {"start": v(-15.59, 27.06) * mm, "end": v(-15.67, 27.14) * mm});
            skLineSegment(sketch, "E1272", {"start": v(-15.67, 27.14) * mm, "end": v(-15.74, 27.22) * mm});
            skLineSegment(sketch, "E1273", {"start": v(-15.74, 27.22) * mm, "end": v(-15.83, 27.27) * mm});
            skLineSegment(sketch, "E1274", {"start": v(-15.83, 27.27) * mm, "end": v(-15.95, 27.25) * mm});
            skLineSegment(sketch, "E1275", {"start": v(-15.95, 27.25) * mm, "end": v(-16.07, 27.18) * mm});
            skLineSegment(sketch, "E1276", {"start": v(-16.07, 27.18) * mm, "end": v(-16.2, 27.1) * mm});
            skLineSegment(sketch, "E1277", {"start": v(-16.2, 27.1) * mm, "end": v(-16.27, 27.01) * mm});
            skLineSegment(sketch, "E1278", {"start": v(-16.27, 27.01) * mm, "end": v(-16.27, 26.9) * mm});
            skLineSegment(sketch, "E1279", {"start": v(-16.27, 26.9) * mm, "end": v(-16.23, 26.8) * mm});
            skLineSegment(sketch, "E1280", {"start": v(-16.23, 26.8) * mm, "end": v(-16.2, 26.7) * mm});
            skLineSegment(sketch, "E1281", {"start": v(-16.2, 26.7) * mm, "end": v(-16.2, 26.58) * mm});
            skLineSegment(sketch, "E1282", {"start": v(-16.2, 26.58) * mm, "end": v(-16.2, 26.47) * mm});
            skLineSegment(sketch, "E1283", {"start": v(-16.2, 26.47) * mm, "end": v(-16.23, 26.33) * mm});
            skLineSegment(sketch, "E1284", {"start": v(-16.23, 26.33) * mm, "end": v(-16.3, 26.2) * mm});
            skLineSegment(sketch, "E1285", {"start": v(-16.3, 26.2) * mm, "end": v(-16.4, 26.1) * mm});
            skLineSegment(sketch, "E1286", {"start": v(-16.4, 26.1) * mm, "end": v(-16.5, 26) * mm});
            skLineSegment(sketch, "E1287", {"start": v(-16.5, 26) * mm, "end": v(-16.63, 25.94) * mm});
            skLineSegment(sketch, "E1288", {"start": v(-16.63, 25.94) * mm, "end": v(-16.77, 25.9) * mm});
            skLineSegment(sketch, "E1289", {"start": v(-16.77, 25.9) * mm, "end": v(-16.92, 25.9) * mm});
            skLineSegment(sketch, "E1290", {"start": v(-16.92, 25.9) * mm, "end": v(-17.06, 25.92) * mm});
            skLineSegment(sketch, "E1291", {"start": v(-17.06, 25.92) * mm, "end": v(-17.16, 25.97) * mm});
            skLineSegment(sketch, "E1292", {"start": v(-17.16, 25.97) * mm, "end": v(-17.25, 26.03) * mm});
            skLineSegment(sketch, "E1293", {"start": v(-17.25, 26.03) * mm, "end": v(-17.34, 26.1) * mm});
            skLineSegment(sketch, "E1294", {"start": v(-17.34, 26.1) * mm, "end": v(-17.42, 26.18) * mm});
            skLineSegment(sketch, "E1295", {"start": v(-17.42, 26.18) * mm, "end": v(-17.51, 26.23) * mm});
            skLineSegment(sketch, "E1296", {"start": v(-17.51, 26.23) * mm, "end": v(-17.63, 26.2) * mm});
            skLineSegment(sketch, "E1297", {"start": v(-17.63, 26.2) * mm, "end": v(-17.75, 26.12) * mm});
            skLineSegment(sketch, "E1298", {"start": v(-17.75, 26.12) * mm, "end": v(-17.87, 26.03) * mm});
            skLineSegment(sketch, "E1299", {"start": v(-17.87, 26.03) * mm, "end": v(-17.94, 25.94) * mm});
            skLineSegment(sketch, "E1300", {"start": v(-17.94, 25.94) * mm, "end": v(-17.93, 25.83) * mm});
            skLineSegment(sketch, "E1301", {"start": v(-17.93, 25.83) * mm, "end": v(-17.88, 25.73) * mm});
            skLineSegment(sketch, "E1302", {"start": v(-17.88, 25.73) * mm, "end": v(-17.85, 25.62) * mm});
            skLineSegment(sketch, "E1303", {"start": v(-17.85, 25.62) * mm, "end": v(-17.83, 25.51) * mm});
            skLineSegment(sketch, "E1304", {"start": v(-17.83, 25.51) * mm, "end": v(-17.82, 25.4) * mm});
            skLineSegment(sketch, "E1305", {"start": v(-17.82, 25.4) * mm, "end": v(-17.85, 25.26) * mm});
            skLineSegment(sketch, "E1306", {"start": v(-17.85, 25.26) * mm, "end": v(-17.91, 25.13) * mm});
            skLineSegment(sketch, "E1307", {"start": v(-17.91, 25.13) * mm, "end": v(-18, 25.02) * mm});
            skLineSegment(sketch, "E1308", {"start": v(-18, 25.02) * mm, "end": v(-18.1, 24.92) * mm});
            skLineSegment(sketch, "E1309", {"start": v(-18.1, 24.92) * mm, "end": v(-18.23, 24.85) * mm});
            skLineSegment(sketch, "E1310", {"start": v(-18.23, 24.85) * mm, "end": v(-18.37, 24.8) * mm});
            skLineSegment(sketch, "E1311", {"start": v(-18.37, 24.8) * mm, "end": v(-18.5, 24.78) * mm});
            skLineSegment(sketch, "E1312", {"start": v(-18.5, 24.78) * mm, "end": v(-18.65, 24.8) * mm});
            skLineSegment(sketch, "E1313", {"start": v(-18.65, 24.8) * mm, "end": v(-18.76, 24.84) * mm});
            skLineSegment(sketch, "E1314", {"start": v(-18.76, 24.84) * mm, "end": v(-18.85, 24.9) * mm});
            skLineSegment(sketch, "E1315", {"start": v(-18.85, 24.9) * mm, "end": v(-18.94, 24.96) * mm});
            skLineSegment(sketch, "E1316", {"start": v(-18.94, 24.96) * mm, "end": v(-19.03, 25.03) * mm});
            skLineSegment(sketch, "E1317", {"start": v(-19.03, 25.03) * mm, "end": v(-19.13, 25.08) * mm});
            skLineSegment(sketch, "E1318", {"start": v(-19.13, 25.08) * mm, "end": v(-19.24, 25.04) * mm});
            skLineSegment(sketch, "E1319", {"start": v(-19.24, 25.04) * mm, "end": v(-19.35, 24.95) * mm});
            skLineSegment(sketch, "E1320", {"start": v(-19.35, 24.95) * mm, "end": v(-19.47, 24.86) * mm});
            skLineSegment(sketch, "E1321", {"start": v(-19.47, 24.86) * mm, "end": v(-19.53, 24.76) * mm});
            skLineSegment(sketch, "E1322", {"start": v(-19.53, 24.76) * mm, "end": v(-19.51, 24.65) * mm});
            skLineSegment(sketch, "E1323", {"start": v(-19.51, 24.65) * mm, "end": v(-19.46, 24.56) * mm});
            skLineSegment(sketch, "E1324", {"start": v(-19.46, 24.56) * mm, "end": v(-19.42, 24.45) * mm});
            skLineSegment(sketch, "E1325", {"start": v(-19.42, 24.45) * mm, "end": v(-19.4, 24.34) * mm});
            skLineSegment(sketch, "E1326", {"start": v(-19.4, 24.34) * mm, "end": v(-19.38, 24.23) * mm});
            skLineSegment(sketch, "E1327", {"start": v(-19.38, 24.23) * mm, "end": v(-19.4, 24.09) * mm});
            skLineSegment(sketch, "E1328", {"start": v(-19.4, 24.09) * mm, "end": v(-19.45, 23.96) * mm});
            skLineSegment(sketch, "E1329", {"start": v(-19.45, 23.96) * mm, "end": v(-19.53, 23.84) * mm});
            skLineSegment(sketch, "E1330", {"start": v(-19.53, 23.84) * mm, "end": v(-19.63, 23.73) * mm});
            skLineSegment(sketch, "E1331", {"start": v(-19.63, 23.73) * mm, "end": v(-19.75, 23.65) * mm});
            skLineSegment(sketch, "E1332", {"start": v(-19.75, 23.65) * mm, "end": v(-19.89, 23.6) * mm});
            skLineSegment(sketch, "E1333", {"start": v(-19.89, 23.6) * mm, "end": v(-20.03, 23.57) * mm});
            skLineSegment(sketch, "E1334", {"start": v(-20.03, 23.57) * mm, "end": v(-20.17, 23.58) * mm});
            skLineSegment(sketch, "E1335", {"start": v(-20.17, 23.58) * mm, "end": v(-20.28, 23.62) * mm});
            skLineSegment(sketch, "E1336", {"start": v(-20.28, 23.62) * mm, "end": v(-20.38, 23.66) * mm});
            skLineSegment(sketch, "E1337", {"start": v(-20.38, 23.66) * mm, "end": v(-20.47, 23.72) * mm});
            skLineSegment(sketch, "E1338", {"start": v(-20.47, 23.72) * mm, "end": v(-20.56, 23.79) * mm});
            skLineSegment(sketch, "E1339", {"start": v(-20.56, 23.79) * mm, "end": v(-20.66, 23.82) * mm});
            skLineSegment(sketch, "E1340", {"start": v(-20.66, 23.82) * mm, "end": v(-20.77, 23.78) * mm});
            skLineSegment(sketch, "E1341", {"start": v(-20.77, 23.78) * mm, "end": v(-20.88, 23.69) * mm});
            skLineSegment(sketch, "E1342", {"start": v(-20.88, 23.69) * mm, "end": v(-21, 23.59) * mm});
            skLineSegment(sketch, "E1343", {"start": v(-21, 23.59) * mm, "end": v(-21.05, 23.49) * mm});
            skLineSegment(sketch, "E1344", {"start": v(-21.05, 23.49) * mm, "end": v(-21.02, 23.38) * mm});
            skLineSegment(sketch, "E1345", {"start": v(-21.02, 23.38) * mm, "end": v(-20.97, 23.29) * mm});
            skLineSegment(sketch, "E1346", {"start": v(-20.97, 23.29) * mm, "end": v(-20.92, 23.19) * mm});
            skLineSegment(sketch, "E1347", {"start": v(-20.92, 23.19) * mm, "end": v(-20.89, 23.08) * mm});
            skLineSegment(sketch, "E1348", {"start": v(-20.89, 23.08) * mm, "end": v(-20.87, 22.97) * mm});
            skLineSegment(sketch, "E1349", {"start": v(-20.87, 22.97) * mm, "end": v(-20.88, 22.82) * mm});
            skLineSegment(sketch, "E1350", {"start": v(-20.88, 22.82) * mm, "end": v(-20.92, 22.69) * mm});
            skLineSegment(sketch, "E1351", {"start": v(-20.92, 22.69) * mm, "end": v(-20.99, 22.56) * mm});
            skLineSegment(sketch, "E1352", {"start": v(-20.99, 22.56) * mm, "end": v(-21.08, 22.45) * mm});
            skLineSegment(sketch, "E1353", {"start": v(-21.08, 22.45) * mm, "end": v(-21.2, 22.36) * mm});
            skLineSegment(sketch, "E1354", {"start": v(-21.2, 22.36) * mm, "end": v(-21.33, 22.3) * mm});
            skLineSegment(sketch, "E1355", {"start": v(-21.33, 22.3) * mm, "end": v(-21.47, 22.27) * mm});
            skLineSegment(sketch, "E1356", {"start": v(-21.47, 22.27) * mm, "end": v(-21.61, 22.27) * mm});
            skLineSegment(sketch, "E1357", {"start": v(-21.61, 22.27) * mm, "end": v(-21.72, 22.3) * mm});
            skLineSegment(sketch, "E1358", {"start": v(-21.72, 22.3) * mm, "end": v(-21.83, 22.34) * mm});
            skLineSegment(sketch, "E1359", {"start": v(-21.83, 22.34) * mm, "end": v(-21.92, 22.39) * mm});
            skLineSegment(sketch, "E1360", {"start": v(-21.92, 22.39) * mm, "end": v(-22.01, 22.45) * mm});
            skLineSegment(sketch, "E1361", {"start": v(-22.01, 22.45) * mm, "end": v(-22.12, 22.48) * mm});
            skLineSegment(sketch, "E1362", {"start": v(-22.12, 22.48) * mm, "end": v(-22.22, 22.43) * mm});
            skLineSegment(sketch, "E1363", {"start": v(-22.22, 22.43) * mm, "end": v(-22.33, 22.33) * mm});
            skLineSegment(sketch, "E1364", {"start": v(-22.33, 22.33) * mm, "end": v(-22.43, 22.22) * mm});
            skLineSegment(sketch, "E1365", {"start": v(-22.43, 22.22) * mm, "end": v(-22.48, 22.12) * mm});
            skLineSegment(sketch, "E1366", {"start": v(-22.48, 22.12) * mm, "end": v(-22.45, 22.01) * mm});
            skLineSegment(sketch, "E1367", {"start": v(-22.45, 22.01) * mm, "end": v(-22.39, 21.92) * mm});
            skLineSegment(sketch, "E1368", {"start": v(-22.39, 21.92) * mm, "end": v(-22.34, 21.83) * mm});
            skLineSegment(sketch, "E1369", {"start": v(-22.34, 21.83) * mm, "end": v(-22.3, 21.72) * mm});
            skLineSegment(sketch, "E1370", {"start": v(-22.3, 21.72) * mm, "end": v(-22.27, 21.61) * mm});
            skLineSegment(sketch, "E1371", {"start": v(-22.27, 21.61) * mm, "end": v(-22.27, 21.47) * mm});
            skLineSegment(sketch, "E1372", {"start": v(-22.27, 21.47) * mm, "end": v(-22.3, 21.33) * mm});
            skLineSegment(sketch, "E1373", {"start": v(-22.3, 21.33) * mm, "end": v(-22.36, 21.2) * mm});
            skLineSegment(sketch, "E1374", {"start": v(-22.36, 21.2) * mm, "end": v(-22.45, 21.08) * mm});
            skLineSegment(sketch, "E1375", {"start": v(-22.45, 21.08) * mm, "end": v(-22.56, 20.99) * mm});
            skLineSegment(sketch, "E1376", {"start": v(-22.56, 20.99) * mm, "end": v(-22.69, 20.92) * mm});
            skLineSegment(sketch, "E1377", {"start": v(-22.69, 20.92) * mm, "end": v(-22.82, 20.88) * mm});
            skLineSegment(sketch, "E1378", {"start": v(-22.82, 20.88) * mm, "end": v(-22.97, 20.87) * mm});
            skLineSegment(sketch, "E1379", {"start": v(-22.97, 20.87) * mm, "end": v(-23.08, 20.89) * mm});
            skLineSegment(sketch, "E1380", {"start": v(-23.08, 20.89) * mm, "end": v(-23.19, 20.92) * mm});
            skLineSegment(sketch, "E1381", {"start": v(-23.19, 20.92) * mm, "end": v(-23.29, 20.97) * mm});
            skLineSegment(sketch, "E1382", {"start": v(-23.29, 20.97) * mm, "end": v(-23.38, 21.02) * mm});
            skLineSegment(sketch, "E1383", {"start": v(-23.38, 21.02) * mm, "end": v(-23.49, 21.05) * mm});
            skLineSegment(sketch, "E1384", {"start": v(-23.49, 21.05) * mm, "end": v(-23.59, 21) * mm});
            skLineSegment(sketch, "E1385", {"start": v(-23.59, 21) * mm, "end": v(-23.69, 20.88) * mm});
            skLineSegment(sketch, "E1386", {"start": v(-23.69, 20.88) * mm, "end": v(-23.78, 20.77) * mm});
            skLineSegment(sketch, "E1387", {"start": v(-23.78, 20.77) * mm, "end": v(-23.82, 20.66) * mm});
            skLineSegment(sketch, "E1388", {"start": v(-23.82, 20.66) * mm, "end": v(-23.79, 20.56) * mm});
            skLineSegment(sketch, "E1389", {"start": v(-23.79, 20.56) * mm, "end": v(-23.72, 20.47) * mm});
            skLineSegment(sketch, "E1390", {"start": v(-23.72, 20.47) * mm, "end": v(-23.66, 20.38) * mm});
            skLineSegment(sketch, "E1391", {"start": v(-23.66, 20.38) * mm, "end": v(-23.62, 20.28) * mm});
            skLineSegment(sketch, "E1392", {"start": v(-23.62, 20.28) * mm, "end": v(-23.58, 20.17) * mm});
            skLineSegment(sketch, "E1393", {"start": v(-23.58, 20.17) * mm, "end": v(-23.57, 20.03) * mm});
            skLineSegment(sketch, "E1394", {"start": v(-23.57, 20.03) * mm, "end": v(-23.6, 19.89) * mm});
            skLineSegment(sketch, "E1395", {"start": v(-23.6, 19.89) * mm, "end": v(-23.65, 19.75) * mm});
            skLineSegment(sketch, "E1396", {"start": v(-23.65, 19.75) * mm, "end": v(-23.73, 19.63) * mm});
            skLineSegment(sketch, "E1397", {"start": v(-23.73, 19.63) * mm, "end": v(-23.84, 19.53) * mm});
            skLineSegment(sketch, "E1398", {"start": v(-23.84, 19.53) * mm, "end": v(-23.96, 19.45) * mm});
            skLineSegment(sketch, "E1399", {"start": v(-23.96, 19.45) * mm, "end": v(-24.09, 19.4) * mm});
            skLineSegment(sketch, "E1400", {"start": v(-24.09, 19.4) * mm, "end": v(-24.23, 19.38) * mm});
            skLineSegment(sketch, "E1401", {"start": v(-24.23, 19.38) * mm, "end": v(-24.34, 19.4) * mm});
            skLineSegment(sketch, "E1402", {"start": v(-24.34, 19.4) * mm, "end": v(-24.45, 19.42) * mm});
            skLineSegment(sketch, "E1403", {"start": v(-24.45, 19.42) * mm, "end": v(-24.56, 19.46) * mm});
            skLineSegment(sketch, "E1404", {"start": v(-24.56, 19.46) * mm, "end": v(-24.65, 19.51) * mm});
            skLineSegment(sketch, "E1405", {"start": v(-24.65, 19.51) * mm, "end": v(-24.76, 19.53) * mm});
            skLineSegment(sketch, "E1406", {"start": v(-24.76, 19.53) * mm, "end": v(-24.86, 19.47) * mm});
            skLineSegment(sketch, "E1407", {"start": v(-24.86, 19.47) * mm, "end": v(-24.95, 19.35) * mm});
            skLineSegment(sketch, "E1408", {"start": v(-24.95, 19.35) * mm, "end": v(-25.04, 19.24) * mm});
            skLineSegment(sketch, "E1409", {"start": v(-25.04, 19.24) * mm, "end": v(-25.08, 19.13) * mm});
            skLineSegment(sketch, "E1410", {"start": v(-25.08, 19.13) * mm, "end": v(-25.03, 19.03) * mm});
            skLineSegment(sketch, "E1411", {"start": v(-25.03, 19.03) * mm, "end": v(-24.96, 18.94) * mm});
            skLineSegment(sketch, "E1412", {"start": v(-24.96, 18.94) * mm, "end": v(-24.9, 18.85) * mm});
            skLineSegment(sketch, "E1413", {"start": v(-24.9, 18.85) * mm, "end": v(-24.84, 18.76) * mm});
            skLineSegment(sketch, "E1414", {"start": v(-24.84, 18.76) * mm, "end": v(-24.8, 18.65) * mm});
            skLineSegment(sketch, "E1415", {"start": v(-24.8, 18.65) * mm, "end": v(-24.78, 18.5) * mm});
            skLineSegment(sketch, "E1416", {"start": v(-24.78, 18.5) * mm, "end": v(-24.8, 18.37) * mm});
            skLineSegment(sketch, "E1417", {"start": v(-24.8, 18.37) * mm, "end": v(-24.85, 18.23) * mm});
            skLineSegment(sketch, "E1418", {"start": v(-24.85, 18.23) * mm, "end": v(-24.92, 18.1) * mm});
            skLineSegment(sketch, "E1419", {"start": v(-24.92, 18.1) * mm, "end": v(-25.02, 18) * mm});
            skLineSegment(sketch, "E1420", {"start": v(-25.02, 18) * mm, "end": v(-25.13, 17.91) * mm});
            skLineSegment(sketch, "E1421", {"start": v(-25.13, 17.91) * mm, "end": v(-25.26, 17.85) * mm});
            skLineSegment(sketch, "E1422", {"start": v(-25.26, 17.85) * mm, "end": v(-25.4, 17.82) * mm});
            skLineSegment(sketch, "E1423", {"start": v(-25.4, 17.82) * mm, "end": v(-25.51, 17.83) * mm});
            skLineSegment(sketch, "E1424", {"start": v(-25.51, 17.83) * mm, "end": v(-25.62, 17.85) * mm});
            skLineSegment(sketch, "E1425", {"start": v(-25.62, 17.85) * mm, "end": v(-25.73, 17.88) * mm});
            skLineSegment(sketch, "E1426", {"start": v(-25.73, 17.88) * mm, "end": v(-25.83, 17.93) * mm});
            skLineSegment(sketch, "E1427", {"start": v(-25.83, 17.93) * mm, "end": v(-25.94, 17.94) * mm});
            skLineSegment(sketch, "E1428", {"start": v(-25.94, 17.94) * mm, "end": v(-26.03, 17.87) * mm});
            skLineSegment(sketch, "E1429", {"start": v(-26.03, 17.87) * mm, "end": v(-26.12, 17.75) * mm});
            skLineSegment(sketch, "E1430", {"start": v(-26.12, 17.75) * mm, "end": v(-26.2, 17.63) * mm});
            skLineSegment(sketch, "E1431", {"start": v(-26.2, 17.63) * mm, "end": v(-26.23, 17.51) * mm});
            skLineSegment(sketch, "E1432", {"start": v(-26.23, 17.51) * mm, "end": v(-26.18, 17.42) * mm});
            skLineSegment(sketch, "E1433", {"start": v(-26.18, 17.42) * mm, "end": v(-26.1, 17.34) * mm});
            skLineSegment(sketch, "E1434", {"start": v(-26.1, 17.34) * mm, "end": v(-26.03, 17.25) * mm});
            skLineSegment(sketch, "E1435", {"start": v(-26.03, 17.25) * mm, "end": v(-25.97, 17.16) * mm});
            skLineSegment(sketch, "E1436", {"start": v(-25.97, 17.16) * mm, "end": v(-25.92, 17.06) * mm});
            skLineSegment(sketch, "E1437", {"start": v(-25.92, 17.06) * mm, "end": v(-25.9, 16.92) * mm});
            skLineSegment(sketch, "E1438", {"start": v(-25.9, 16.92) * mm, "end": v(-25.9, 16.77) * mm});
            skLineSegment(sketch, "E1439", {"start": v(-25.9, 16.77) * mm, "end": v(-25.94, 16.63) * mm});
            skLineSegment(sketch, "E1440", {"start": v(-25.94, 16.63) * mm, "end": v(-26, 16.5) * mm});
            skLineSegment(sketch, "E1441", {"start": v(-26, 16.5) * mm, "end": v(-26.1, 16.4) * mm});
            skLineSegment(sketch, "E1442", {"start": v(-26.1, 16.4) * mm, "end": v(-26.2, 16.3) * mm});
            skLineSegment(sketch, "E1443", {"start": v(-26.2, 16.3) * mm, "end": v(-26.33, 16.23) * mm});
            skLineSegment(sketch, "E1444", {"start": v(-26.33, 16.23) * mm, "end": v(-26.47, 16.2) * mm});
            skLineSegment(sketch, "E1445", {"start": v(-26.47, 16.2) * mm, "end": v(-26.58, 16.2) * mm});
            skLineSegment(sketch, "E1446", {"start": v(-26.58, 16.2) * mm, "end": v(-26.7, 16.2) * mm});
            skLineSegment(sketch, "E1447", {"start": v(-26.7, 16.2) * mm, "end": v(-26.8, 16.23) * mm});
            skLineSegment(sketch, "E1448", {"start": v(-26.8, 16.23) * mm, "end": v(-26.9, 16.27) * mm});
            skLineSegment(sketch, "E1449", {"start": v(-26.9, 16.27) * mm, "end": v(-27.01, 16.27) * mm});
            skLineSegment(sketch, "E1450", {"start": v(-27.01, 16.27) * mm, "end": v(-27.1, 16.2) * mm});
            skLineSegment(sketch, "E1451", {"start": v(-27.1, 16.2) * mm, "end": v(-27.18, 16.07) * mm});
            skLineSegment(sketch, "E1452", {"start": v(-27.18, 16.07) * mm, "end": v(-27.25, 15.95) * mm});
            skLineSegment(sketch, "E1453", {"start": v(-27.25, 15.95) * mm, "end": v(-27.27, 15.83) * mm});
            skLineSegment(sketch, "E1454", {"start": v(-27.27, 15.83) * mm, "end": v(-27.22, 15.74) * mm});
            skLineSegment(sketch, "E1455", {"start": v(-27.22, 15.74) * mm, "end": v(-27.14, 15.67) * mm});
            skLineSegment(sketch, "E1456", {"start": v(-27.14, 15.67) * mm, "end": v(-27.06, 15.59) * mm});
            skLineSegment(sketch, "E1457", {"start": v(-27.06, 15.59) * mm, "end": v(-27, 15.5) * mm});
            skLineSegment(sketch, "E1458", {"start": v(-27, 15.5) * mm, "end": v(-26.94, 15.4) * mm});
            skLineSegment(sketch, "E1459", {"start": v(-26.94, 15.4) * mm, "end": v(-26.9, 15.26) * mm});
            skLineSegment(sketch, "E1460", {"start": v(-26.9, 15.26) * mm, "end": v(-26.9, 15.11) * mm});
            skLineSegment(sketch, "E1461", {"start": v(-26.9, 15.11) * mm, "end": v(-26.93, 14.97) * mm});
            skLineSegment(sketch, "E1462", {"start": v(-26.93, 14.97) * mm, "end": v(-27, 14.84) * mm});
            skLineSegment(sketch, "E1463", {"start": v(-27, 14.84) * mm, "end": v(-27.07, 14.72) * mm});
            skLineSegment(sketch, "E1464", {"start": v(-27.07, 14.72) * mm, "end": v(-27.18, 14.62) * mm});
            skLineSegment(sketch, "E1465", {"start": v(-27.18, 14.62) * mm, "end": v(-27.3, 14.54) * mm});
            skLineSegment(sketch, "E1466", {"start": v(-27.3, 14.54) * mm, "end": v(-27.43, 14.5) * mm});
            skLineSegment(sketch, "E1467", {"start": v(-27.43, 14.5) * mm, "end": v(-27.55, 14.5) * mm});
            skLineSegment(sketch, "E1468", {"start": v(-27.55, 14.5) * mm, "end": v(-27.66, 14.5) * mm});
            skLineSegment(sketch, "E1469", {"start": v(-27.66, 14.5) * mm, "end": v(-27.77, 14.52) * mm});
            skLineSegment(sketch, "E1470", {"start": v(-27.77, 14.52) * mm, "end": v(-27.87, 14.55) * mm});
            skLineSegment(sketch, "E1471", {"start": v(-27.87, 14.55) * mm, "end": v(-27.98, 14.55) * mm});
            skLineSegment(sketch, "E1472", {"start": v(-27.98, 14.55) * mm, "end": v(-28.07, 14.47) * mm});
            skLineSegment(sketch, "E1473", {"start": v(-28.07, 14.47) * mm, "end": v(-28.14, 14.34) * mm});
            skLineSegment(sketch, "E1474", {"start": v(-28.14, 14.34) * mm, "end": v(-28.2, 14.2) * mm});
            skLineSegment(sketch, "E1475", {"start": v(-28.2, 14.2) * mm, "end": v(-28.21, 14.09) * mm});
            skLineSegment(sketch, "E1476", {"start": v(-28.21, 14.09) * mm, "end": v(-28.15, 14) * mm});
            skLineSegment(sketch, "E1477", {"start": v(-28.15, 14) * mm, "end": v(-28.07, 13.93) * mm});
            skLineSegment(sketch, "E1478", {"start": v(-28.07, 13.93) * mm, "end": v(-27.99, 13.86) * mm});
            skLineSegment(sketch, "E1479", {"start": v(-27.99, 13.86) * mm, "end": v(-27.92, 13.77) * mm});
            skLineSegment(sketch, "E1480", {"start": v(-27.92, 13.77) * mm, "end": v(-27.86, 13.67) * mm});
            skLineSegment(sketch, "E1481", {"start": v(-27.86, 13.67) * mm, "end": v(-27.81, 13.54) * mm});
            skLineSegment(sketch, "E1482", {"start": v(-27.81, 13.54) * mm, "end": v(-27.8, 13.4) * mm});
            skLineSegment(sketch, "E1483", {"start": v(-27.8, 13.4) * mm, "end": v(-27.82, 13.25) * mm});
            skLineSegment(sketch, "E1484", {"start": v(-27.82, 13.25) * mm, "end": v(-27.87, 13.11) * mm});
            skLineSegment(sketch, "E1485", {"start": v(-27.87, 13.11) * mm, "end": v(-27.94, 13) * mm});
            skLineSegment(sketch, "E1486", {"start": v(-27.94, 13) * mm, "end": v(-28.04, 12.88) * mm});
            skLineSegment(sketch, "E1487", {"start": v(-28.04, 12.88) * mm, "end": v(-28.16, 12.8) * mm});
            skLineSegment(sketch, "E1488", {"start": v(-28.16, 12.8) * mm, "end": v(-28.3, 12.75) * mm});
            skLineSegment(sketch, "E1489", {"start": v(-28.3, 12.75) * mm, "end": v(-28.4, 12.73) * mm});
            skLineSegment(sketch, "E1490", {"start": v(-28.4, 12.73) * mm, "end": v(-28.52, 12.73) * mm});
            skLineSegment(sketch, "E1491", {"start": v(-28.52, 12.73) * mm, "end": v(-28.62, 12.74) * mm});
            skLineSegment(sketch, "E1492", {"start": v(-28.62, 12.74) * mm, "end": v(-28.73, 12.77) * mm});
            skLineSegment(sketch, "E1493", {"start": v(-28.73, 12.77) * mm, "end": v(-28.84, 12.76) * mm});
            skLineSegment(sketch, "E1494", {"start": v(-28.84, 12.76) * mm, "end": v(-28.92, 12.68) * mm});
            skLineSegment(sketch, "E1495", {"start": v(-28.92, 12.68) * mm, "end": v(-28.98, 12.54) * mm});
            skLineSegment(sketch, "E1496", {"start": v(-28.98, 12.54) * mm, "end": v(-29.04, 12.4) * mm});
            skLineSegment(sketch, "E1497", {"start": v(-29.04, 12.4) * mm, "end": v(-29.04, 12.29) * mm});
            skLineSegment(sketch, "E1498", {"start": v(-29.04, 12.29) * mm, "end": v(-28.98, 12.2) * mm});
            skLineSegment(sketch, "E1499", {"start": v(-28.98, 12.2) * mm, "end": v(-28.89, 12.14) * mm});
            skLineSegment(sketch, "E1500", {"start": v(-28.89, 12.14) * mm, "end": v(-28.8, 12.07) * mm});
            skLineSegment(sketch, "E1501", {"start": v(-28.8, 12.07) * mm, "end": v(-28.73, 11.99) * mm});
            skLineSegment(sketch, "E1502", {"start": v(-28.73, 11.99) * mm, "end": v(-28.66, 11.9) * mm});
            skLineSegment(sketch, "E1503", {"start": v(-28.66, 11.9) * mm, "end": v(-28.6, 11.76) * mm});
            skLineSegment(sketch, "E1504", {"start": v(-28.6, 11.76) * mm, "end": v(-28.59, 11.62) * mm});
            skLineSegment(sketch, "E1505", {"start": v(-28.59, 11.62) * mm, "end": v(-28.6, 11.48) * mm});
            skLineSegment(sketch, "E1506", {"start": v(-28.6, 11.48) * mm, "end": v(-28.64, 11.34) * mm});
            skLineSegment(sketch, "E1507", {"start": v(-28.64, 11.34) * mm, "end": v(-28.7, 11.2) * mm});
            skLineSegment(sketch, "E1508", {"start": v(-28.7, 11.2) * mm, "end": v(-28.8, 11.1) * mm});
            skLineSegment(sketch, "E1509", {"start": v(-28.8, 11.1) * mm, "end": v(-28.9, 11) * mm});
            skLineSegment(sketch, "E1510", {"start": v(-28.9, 11) * mm, "end": v(-29.04, 10.95) * mm});
            skLineSegment(sketch, "E1511", {"start": v(-29.04, 10.95) * mm, "end": v(-29.15, 10.92) * mm});
            skLineSegment(sketch, "E1512", {"start": v(-29.15, 10.92) * mm, "end": v(-29.26, 10.92) * mm});
            skLineSegment(sketch, "E1513", {"start": v(-29.26, 10.92) * mm, "end": v(-29.37, 10.92) * mm});
            skLineSegment(sketch, "E1514", {"start": v(-29.37, 10.92) * mm, "end": v(-29.48, 10.94) * mm});
            skLineSegment(sketch, "E1515", {"start": v(-29.48, 10.94) * mm, "end": v(-29.58, 10.92) * mm});
            skLineSegment(sketch, "E1516", {"start": v(-29.58, 10.92) * mm, "end": v(-29.66, 10.83) * mm});
            skLineSegment(sketch, "E1517", {"start": v(-29.66, 10.83) * mm, "end": v(-29.71, 10.7) * mm});
            skLineSegment(sketch, "E1518", {"start": v(-29.71, 10.7) * mm, "end": v(-29.76, 10.56) * mm});
            skLineSegment(sketch, "E1519", {"start": v(-29.76, 10.56) * mm, "end": v(-29.76, 10.44) * mm});
            skLineSegment(sketch, "E1520", {"start": v(-29.76, 10.44) * mm, "end": v(-29.69, 10.36) * mm});
            skLineSegment(sketch, "E1521", {"start": v(-29.69, 10.36) * mm, "end": v(-29.6, 10.3) * mm});
            skLineSegment(sketch, "E1522", {"start": v(-29.6, 10.3) * mm, "end": v(-29.5, 10.24) * mm});
            skLineSegment(sketch, "E1523", {"start": v(-29.5, 10.24) * mm, "end": v(-29.42, 10.16) * mm});
            skLineSegment(sketch, "E1524", {"start": v(-29.42, 10.16) * mm, "end": v(-29.35, 10.07) * mm});
            skLineSegment(sketch, "E1525", {"start": v(-29.35, 10.07) * mm, "end": v(-29.29, 9.94) * mm});
            skLineSegment(sketch, "E1526", {"start": v(-29.29, 9.94) * mm, "end": v(-29.26, 9.8) * mm});
            skLineSegment(sketch, "E1527", {"start": v(-29.26, 9.8) * mm, "end": v(-29.26, 9.66) * mm});
            skLineSegment(sketch, "E1528", {"start": v(-29.26, 9.66) * mm, "end": v(-29.3, 9.52) * mm});
            skLineSegment(sketch, "E1529", {"start": v(-29.3, 9.52) * mm, "end": v(-29.35, 9.39) * mm});
            skLineSegment(sketch, "E1530", {"start": v(-29.35, 9.39) * mm, "end": v(-29.44, 9.27) * mm});
            skLineSegment(sketch, "E1531", {"start": v(-29.44, 9.27) * mm, "end": v(-29.54, 9.17) * mm});
            skLineSegment(sketch, "E1532", {"start": v(-29.54, 9.17) * mm, "end": v(-29.67, 9.1) * mm});
            skLineSegment(sketch, "E1533", {"start": v(-29.67, 9.1) * mm, "end": v(-29.78, 9.07) * mm});
            skLineSegment(sketch, "E1534", {"start": v(-29.78, 9.07) * mm, "end": v(-29.89, 9.06) * mm});
            skLineSegment(sketch, "E1535", {"start": v(-29.89, 9.06) * mm, "end": v(-30, 9.06) * mm});
            skLineSegment(sketch, "E1536", {"start": v(-30, 9.06) * mm, "end": v(-30.1, 9.07) * mm});
            skLineSegment(sketch, "E1537", {"start": v(-30.1, 9.07) * mm, "end": v(-30.21, 9.04) * mm});
            skLineSegment(sketch, "E1538", {"start": v(-30.21, 9.04) * mm, "end": v(-30.28, 8.95) * mm});
            skLineSegment(sketch, "E1539", {"start": v(-30.28, 8.95) * mm, "end": v(-30.32, 8.8) * mm});
            skLineSegment(sketch, "E1540", {"start": v(-30.32, 8.8) * mm, "end": v(-30.36, 8.67) * mm});
            skLineSegment(sketch, "E1541", {"start": v(-30.36, 8.67) * mm, "end": v(-30.36, 8.55) * mm});
            skLineSegment(sketch, "E1542", {"start": v(-30.36, 8.55) * mm, "end": v(-30.28, 8.47) * mm});
            skLineSegment(sketch, "E1543", {"start": v(-30.28, 8.47) * mm, "end": v(-30.18, 8.43) * mm});
            skLineSegment(sketch, "E1544", {"start": v(-30.18, 8.43) * mm, "end": v(-30.09, 8.37) * mm});
            skLineSegment(sketch, "E1545", {"start": v(-30.09, 8.37) * mm, "end": v(-30, 8.3) * mm});
            skLineSegment(sketch, "E1546", {"start": v(-30, 8.3) * mm, "end": v(-29.92, 8.21) * mm});
            skLineSegment(sketch, "E1547", {"start": v(-29.92, 8.21) * mm, "end": v(-29.86, 8.09) * mm});
            skLineSegment(sketch, "E1548", {"start": v(-29.86, 8.09) * mm, "end": v(-29.82, 7.95) * mm});
            skLineSegment(sketch, "E1549", {"start": v(-29.82, 7.95) * mm, "end": v(-29.81, 7.8) * mm});
            skLineSegment(sketch, "E1550", {"start": v(-29.81, 7.8) * mm, "end": v(-29.83, 7.66) * mm});
            skLineSegment(sketch, "E1551", {"start": v(-29.83, 7.66) * mm, "end": v(-29.88, 7.52) * mm});
            skLineSegment(sketch, "E1552", {"start": v(-29.88, 7.52) * mm, "end": v(-29.96, 7.4) * mm});
            skLineSegment(sketch, "E1553", {"start": v(-29.96, 7.4) * mm, "end": v(-30.06, 7.3) * mm});
            skLineSegment(sketch, "E1554", {"start": v(-30.06, 7.3) * mm, "end": v(-30.18, 7.22) * mm});
            skLineSegment(sketch, "E1555", {"start": v(-30.18, 7.22) * mm, "end": v(-30.29, 7.19) * mm});
            skLineSegment(sketch, "E1556", {"start": v(-30.29, 7.19) * mm, "end": v(-30.4, 7.16) * mm});
            skLineSegment(sketch, "E1557", {"start": v(-30.4, 7.16) * mm, "end": v(-30.5, 7.16) * mm});
            skLineSegment(sketch, "E1558", {"start": v(-30.5, 7.16) * mm, "end": v(-30.62, 7.16) * mm});
            skLineSegment(sketch, "E1559", {"start": v(-30.62, 7.16) * mm, "end": v(-30.72, 7.13) * mm});
            skLineSegment(sketch, "E1560", {"start": v(-30.72, 7.13) * mm, "end": v(-30.78, 7.03) * mm});
            skLineSegment(sketch, "E1561", {"start": v(-30.78, 7.03) * mm, "end": v(-30.82, 6.89) * mm});
            skLineSegment(sketch, "E1562", {"start": v(-30.82, 6.89) * mm, "end": v(-30.85, 6.74) * mm});
            skLineSegment(sketch, "E1563", {"start": v(-30.85, 6.74) * mm, "end": v(-30.83, 6.63) * mm});
            skLineSegment(sketch, "E1564", {"start": v(-30.83, 6.63) * mm, "end": v(-30.75, 6.56) * mm});
            skLineSegment(sketch, "E1565", {"start": v(-30.75, 6.56) * mm, "end": v(-30.65, 6.51) * mm});
            skLineSegment(sketch, "E1566", {"start": v(-30.65, 6.51) * mm, "end": v(-30.55, 6.46) * mm});
            skLineSegment(sketch, "E1567", {"start": v(-30.55, 6.46) * mm, "end": v(-30.46, 6.4) * mm});
            skLineSegment(sketch, "E1568", {"start": v(-30.46, 6.4) * mm, "end": v(-30.38, 6.32) * mm});
            skLineSegment(sketch, "E1569", {"start": v(-30.38, 6.32) * mm, "end": v(-30.3, 6.2) * mm});
            skLineSegment(sketch, "E1570", {"start": v(-30.3, 6.2) * mm, "end": v(-30.26, 6.06) * mm});
            skLineSegment(sketch, "E1571", {"start": v(-30.26, 6.06) * mm, "end": v(-30.24, 5.92) * mm});
            skLineSegment(sketch, "E1572", {"start": v(-30.24, 5.92) * mm, "end": v(-30.26, 5.77) * mm});
            skLineSegment(sketch, "E1573", {"start": v(-30.26, 5.77) * mm, "end": v(-30.3, 5.63) * mm});
            skLineSegment(sketch, "E1574", {"start": v(-30.3, 5.63) * mm, "end": v(-30.36, 5.5) * mm});
            skLineSegment(sketch, "E1575", {"start": v(-30.36, 5.5) * mm, "end": v(-30.46, 5.4) * mm});
            skLineSegment(sketch, "E1576", {"start": v(-30.46, 5.4) * mm, "end": v(-30.57, 5.31) * mm});
            skLineSegment(sketch, "E1577", {"start": v(-30.57, 5.31) * mm, "end": v(-30.68, 5.27) * mm});
            skLineSegment(sketch, "E1578", {"start": v(-30.68, 5.27) * mm, "end": v(-30.79, 5.24) * mm});
            skLineSegment(sketch, "E1579", {"start": v(-30.79, 5.24) * mm, "end": v(-30.9, 5.23) * mm});
            skLineSegment(sketch, "E1580", {"start": v(-30.9, 5.23) * mm, "end": v(-31, 5.22) * mm});
            skLineSegment(sketch, "E1581", {"start": v(-31, 5.22) * mm, "end": v(-31.1, 5.19) * mm});
            skLineSegment(sketch, "E1582", {"start": v(-31.1, 5.19) * mm, "end": v(-31.16, 5.08) * mm});
            skLineSegment(sketch, "E1583", {"start": v(-31.16, 5.08) * mm, "end": v(-31.19, 4.94) * mm});
            skLineSegment(sketch, "E1584", {"start": v(-31.19, 4.94) * mm, "end": v(-31.21, 4.8) * mm});
            skLineSegment(sketch, "E1585", {"start": v(-31.21, 4.8) * mm, "end": v(-31.19, 4.68) * mm});
            skLineSegment(sketch, "E1586", {"start": v(-31.19, 4.68) * mm, "end": v(-31.1, 4.61) * mm});
            skLineSegment(sketch, "E1587", {"start": v(-31.1, 4.61) * mm, "end": v(-31, 4.58) * mm});
            skLineSegment(sketch, "E1588", {"start": v(-31, 4.58) * mm, "end": v(-30.9, 4.53) * mm});
            skLineSegment(sketch, "E1589", {"start": v(-30.9, 4.53) * mm, "end": v(-30.8, 4.47) * mm});
            skLineSegment(sketch, "E1590", {"start": v(-30.8, 4.47) * mm, "end": v(-30.72, 4.4) * mm});
            skLineSegment(sketch, "E1591", {"start": v(-30.72, 4.4) * mm, "end": v(-30.63, 4.28) * mm});
            skLineSegment(sketch, "E1592", {"start": v(-30.63, 4.28) * mm, "end": v(-30.58, 4.15) * mm});
            skLineSegment(sketch, "E1593", {"start": v(-30.58, 4.15) * mm, "end": v(-30.55, 4) * mm});
            skLineSegment(sketch, "E1594", {"start": v(-30.55, 4) * mm, "end": v(-30.56, 3.86) * mm});
            skLineSegment(sketch, "E1595", {"start": v(-30.56, 3.86) * mm, "end": v(-30.6, 3.72) * mm});
            skLineSegment(sketch, "E1596", {"start": v(-30.6, 3.72) * mm, "end": v(-30.65, 3.59) * mm});
            skLineSegment(sketch, "E1597", {"start": v(-30.65, 3.59) * mm, "end": v(-30.74, 3.47) * mm});
            skLineSegment(sketch, "E1598", {"start": v(-30.74, 3.47) * mm, "end": v(-30.85, 3.38) * mm});
            skLineSegment(sketch, "E1599", {"start": v(-30.85, 3.38) * mm, "end": v(-30.95, 3.33) * mm});
            skLineSegment(sketch, "E1600", {"start": v(-30.95, 3.33) * mm, "end": v(-31.05, 3.3) * mm});
            skLineSegment(sketch, "E1601", {"start": v(-31.05, 3.3) * mm, "end": v(-31.16, 3.28) * mm});
            skLineSegment(sketch, "E1602", {"start": v(-31.16, 3.28) * mm, "end": v(-31.27, 3.27) * mm});
            skLineSegment(sketch, "E1603", {"start": v(-31.27, 3.27) * mm, "end": v(-31.37, 3.22) * mm});
            skLineSegment(sketch, "E1604", {"start": v(-31.37, 3.22) * mm, "end": v(-31.42, 3.12) * mm});
            skLineSegment(sketch, "E1605", {"start": v(-31.42, 3.12) * mm, "end": v(-31.44, 2.97) * mm});
            skLineSegment(sketch, "E1606", {"start": v(-31.44, 2.97) * mm, "end": v(-31.45, 2.83) * mm});
            skLineSegment(sketch, "E1607", {"start": v(-31.45, 2.83) * mm, "end": v(-31.42, 2.71) * mm});
            skLineSegment(sketch, "E1608", {"start": v(-31.42, 2.71) * mm, "end": v(-31.33, 2.65) * mm});
            skLineSegment(sketch, "E1609", {"start": v(-31.33, 2.65) * mm, "end": v(-31.22, 2.62) * mm});
            skLineSegment(sketch, "E1610", {"start": v(-31.22, 2.62) * mm, "end": v(-31.12, 2.58) * mm});
            skLineSegment(sketch, "E1611", {"start": v(-31.12, 2.58) * mm, "end": v(-31.02, 2.53) * mm});
            skLineSegment(sketch, "E1612", {"start": v(-31.02, 2.53) * mm, "end": v(-30.93, 2.46) * mm});
            skLineSegment(sketch, "E1613", {"start": v(-30.93, 2.46) * mm, "end": v(-30.84, 2.35) * mm});
            skLineSegment(sketch, "E1614", {"start": v(-30.84, 2.35) * mm, "end": v(-30.78, 2.22) * mm});
            skLineSegment(sketch, "E1615", {"start": v(-30.78, 2.22) * mm, "end": v(-30.75, 2.08) * mm});
            skLineSegment(sketch, "E1616", {"start": v(-30.75, 2.08) * mm, "end": v(-30.74, 1.93) * mm});
            skLineSegment(sketch, "E1617", {"start": v(-30.74, 1.93) * mm, "end": v(-30.76, 1.8) * mm});
            skLineSegment(sketch, "E1618", {"start": v(-30.76, 1.8) * mm, "end": v(-30.82, 1.66) * mm});
            skLineSegment(sketch, "E1619", {"start": v(-30.82, 1.66) * mm, "end": v(-30.9, 1.54) * mm});
            skLineSegment(sketch, "E1620", {"start": v(-30.9, 1.54) * mm, "end": v(-31, 1.44) * mm});
            skLineSegment(sketch, "E1621", {"start": v(-31, 1.44) * mm, "end": v(-31.1, 1.38) * mm});
            skLineSegment(sketch, "E1622", {"start": v(-31.1, 1.38) * mm, "end": v(-31.2, 1.34) * mm});
            skLineSegment(sketch, "E1623", {"start": v(-31.2, 1.34) * mm, "end": v(-31.3, 1.31) * mm});
            skLineSegment(sketch, "E1624", {"start": v(-31.3, 1.31) * mm, "end": v(-31.42, 1.3) * mm});
            skLineSegment(sketch, "E1625", {"start": v(-31.42, 1.3) * mm, "end": v(-31.51, 1.25) * mm});
            skLineSegment(sketch, "E1626", {"start": v(-31.51, 1.25) * mm, "end": v(-31.56, 1.14) * mm});
            skLineSegment(sketch, "E1627", {"start": v(-31.56, 1.14) * mm, "end": v(-31.56, 1) * mm});
            skLineSegment(sketch, "E1628", {"start": v(-31.56, 1) * mm, "end": v(-31.56, 0.84) * mm});
            skLineSegment(sketch, "E1629", {"start": v(-31.56, 0.84) * mm, "end": v(-31.53, 0.73) * mm});
            skLineSegment(sketch, "E1630", {"start": v(-31.53, 0.73) * mm, "end": v(-31.44, 0.68) * mm});
            skLineSegment(sketch, "E1631", {"start": v(-31.44, 0.68) * mm, "end": v(-31.33, 0.66) * mm});
            skLineSegment(sketch, "E1632", {"start": v(-31.33, 0.66) * mm, "end": v(-31.22, 0.62) * mm});
            skLineSegment(sketch, "E1633", {"start": v(-31.22, 0.62) * mm, "end": v(-31.12, 0.57) * mm});
            skLineSegment(sketch, "E1634", {"start": v(-31.12, 0.57) * mm, "end": v(-31.03, 0.51) * mm});
            skLineSegment(sketch, "E1635", {"start": v(-31.03, 0.51) * mm, "end": v(-30.93, 0.4) * mm});
            skLineSegment(sketch, "E1636", {"start": v(-30.93, 0.4) * mm, "end": v(-30.86, 0.28) * mm});
            skLineSegment(sketch, "E1637", {"start": v(-30.86, 0.28) * mm, "end": v(-30.82, 0.14) * mm});
            skLineSegment(sketch, "E1638", {"start": v(-30.82, 0.14) * mm, "end": v(-30.8, 0) * mm});
            skLineSegment(sketch, "E1639", {"start": v(-30.8, 0) * mm, "end": v(-30.82, -0.14) * mm});
            skLineSegment(sketch, "E1640", {"start": v(-30.82, -0.14) * mm, "end": v(-30.86, -0.28) * mm});
            skLineSegment(sketch, "E1641", {"start": v(-30.86, -0.28) * mm, "end": v(-30.93, -0.4) * mm});
            skLineSegment(sketch, "E1642", {"start": v(-30.93, -0.4) * mm, "end": v(-31.03, -0.51) * mm});
            skLineSegment(sketch, "E1643", {"start": v(-31.03, -0.51) * mm, "end": v(-31.12, -0.57) * mm});
            skLineSegment(sketch, "E1644", {"start": v(-31.12, -0.57) * mm, "end": v(-31.22, -0.62) * mm});
            skLineSegment(sketch, "E1645", {"start": v(-31.22, -0.62) * mm, "end": v(-31.33, -0.66) * mm});
            skLineSegment(sketch, "E1646", {"start": v(-31.33, -0.66) * mm, "end": v(-31.44, -0.68) * mm});
            skLineSegment(sketch, "E1647", {"start": v(-31.44, -0.68) * mm, "end": v(-31.53, -0.73) * mm});
            skLineSegment(sketch, "E1648", {"start": v(-31.53, -0.73) * mm, "end": v(-31.56, -0.84) * mm});
            skLineSegment(sketch, "E1649", {"start": v(-31.56, -0.84) * mm, "end": v(-31.56, -1) * mm});
            skLineSegment(sketch, "E1650", {"start": v(-31.56, -1) * mm, "end": v(-31.56, -1.14) * mm});
            skLineSegment(sketch, "E1651", {"start": v(-31.56, -1.14) * mm, "end": v(-31.51, -1.25) * mm});
            skLineSegment(sketch, "E1652", {"start": v(-31.51, -1.25) * mm, "end": v(-31.42, -1.3) * mm});
            skLineSegment(sketch, "E1653", {"start": v(-31.42, -1.3) * mm, "end": v(-31.3, -1.31) * mm});
            skLineSegment(sketch, "E1654", {"start": v(-31.3, -1.31) * mm, "end": v(-31.2, -1.34) * mm});
            skLineSegment(sketch, "E1655", {"start": v(-31.2, -1.34) * mm, "end": v(-31.1, -1.38) * mm});
            skLineSegment(sketch, "E1656", {"start": v(-31.1, -1.38) * mm, "end": v(-31, -1.44) * mm});
            skLineSegment(sketch, "E1657", {"start": v(-31, -1.44) * mm, "end": v(-30.9, -1.54) * mm});
            skLineSegment(sketch, "E1658", {"start": v(-30.9, -1.54) * mm, "end": v(-30.82, -1.66) * mm});
            skLineSegment(sketch, "E1659", {"start": v(-30.82, -1.66) * mm, "end": v(-30.76, -1.8) * mm});
            skLineSegment(sketch, "E1660", {"start": v(-30.76, -1.8) * mm, "end": v(-30.74, -1.93) * mm});
            skLineSegment(sketch, "E1661", {"start": v(-30.74, -1.93) * mm, "end": v(-30.75, -2.08) * mm});
            skLineSegment(sketch, "E1662", {"start": v(-30.75, -2.08) * mm, "end": v(-30.78, -2.22) * mm});
            skLineSegment(sketch, "E1663", {"start": v(-30.78, -2.22) * mm, "end": v(-30.84, -2.35) * mm});
            skLineSegment(sketch, "E1664", {"start": v(-30.84, -2.35) * mm, "end": v(-30.93, -2.46) * mm});
            skLineSegment(sketch, "E1665", {"start": v(-30.93, -2.46) * mm, "end": v(-31.02, -2.53) * mm});
            skLineSegment(sketch, "E1666", {"start": v(-31.02, -2.53) * mm, "end": v(-31.12, -2.58) * mm});
            skLineSegment(sketch, "E1667", {"start": v(-31.12, -2.58) * mm, "end": v(-31.22, -2.62) * mm});
            skLineSegment(sketch, "E1668", {"start": v(-31.22, -2.62) * mm, "end": v(-31.33, -2.65) * mm});
            skLineSegment(sketch, "E1669", {"start": v(-31.33, -2.65) * mm, "end": v(-31.42, -2.71) * mm});
            skLineSegment(sketch, "E1670", {"start": v(-31.42, -2.71) * mm, "end": v(-31.45, -2.83) * mm});
            skLineSegment(sketch, "E1671", {"start": v(-31.45, -2.83) * mm, "end": v(-31.44, -2.97) * mm});
            skLineSegment(sketch, "E1672", {"start": v(-31.44, -2.97) * mm, "end": v(-31.42, -3.12) * mm});
            skLineSegment(sketch, "E1673", {"start": v(-31.42, -3.12) * mm, "end": v(-31.37, -3.22) * mm});
            skLineSegment(sketch, "E1674", {"start": v(-31.37, -3.22) * mm, "end": v(-31.27, -3.27) * mm});
            skLineSegment(sketch, "E1675", {"start": v(-31.27, -3.27) * mm, "end": v(-31.16, -3.28) * mm});
            skLineSegment(sketch, "E1676", {"start": v(-31.16, -3.28) * mm, "end": v(-31.05, -3.3) * mm});
            skLineSegment(sketch, "E1677", {"start": v(-31.05, -3.3) * mm, "end": v(-30.95, -3.33) * mm});
            skLineSegment(sketch, "E1678", {"start": v(-30.95, -3.33) * mm, "end": v(-30.85, -3.38) * mm});
            skLineSegment(sketch, "E1679", {"start": v(-30.85, -3.38) * mm, "end": v(-30.74, -3.47) * mm});
            skLineSegment(sketch, "E1680", {"start": v(-30.74, -3.47) * mm, "end": v(-30.65, -3.59) * mm});
            skLineSegment(sketch, "E1681", {"start": v(-30.65, -3.59) * mm, "end": v(-30.6, -3.72) * mm});
            skLineSegment(sketch, "E1682", {"start": v(-30.6, -3.72) * mm, "end": v(-30.56, -3.86) * mm});
            skLineSegment(sketch, "E1683", {"start": v(-30.56, -3.86) * mm, "end": v(-30.55, -4) * mm});
            skLineSegment(sketch, "E1684", {"start": v(-30.55, -4) * mm, "end": v(-30.58, -4.15) * mm});
            skLineSegment(sketch, "E1685", {"start": v(-30.58, -4.15) * mm, "end": v(-30.63, -4.28) * mm});
            skLineSegment(sketch, "E1686", {"start": v(-30.63, -4.28) * mm, "end": v(-30.72, -4.4) * mm});
            skLineSegment(sketch, "E1687", {"start": v(-30.72, -4.4) * mm, "end": v(-30.8, -4.47) * mm});
            skLineSegment(sketch, "E1688", {"start": v(-30.8, -4.47) * mm, "end": v(-30.9, -4.53) * mm});
            skLineSegment(sketch, "E1689", {"start": v(-30.9, -4.53) * mm, "end": v(-31, -4.58) * mm});
            skLineSegment(sketch, "E1690", {"start": v(-31, -4.58) * mm, "end": v(-31.1, -4.61) * mm});
            skLineSegment(sketch, "E1691", {"start": v(-31.1, -4.61) * mm, "end": v(-31.19, -4.68) * mm});
            skLineSegment(sketch, "E1692", {"start": v(-31.19, -4.68) * mm, "end": v(-31.21, -4.8) * mm});
            skLineSegment(sketch, "E1693", {"start": v(-31.21, -4.8) * mm, "end": v(-31.19, -4.94) * mm});
            skLineSegment(sketch, "E1694", {"start": v(-31.19, -4.94) * mm, "end": v(-31.16, -5.08) * mm});
            skLineSegment(sketch, "E1695", {"start": v(-31.16, -5.08) * mm, "end": v(-31.1, -5.19) * mm});
            skLineSegment(sketch, "E1696", {"start": v(-31.1, -5.19) * mm, "end": v(-31, -5.22) * mm});
            skLineSegment(sketch, "E1697", {"start": v(-31, -5.22) * mm, "end": v(-30.9, -5.23) * mm});
            skLineSegment(sketch, "E1698", {"start": v(-30.9, -5.23) * mm, "end": v(-30.79, -5.24) * mm});
            skLineSegment(sketch, "E1699", {"start": v(-30.79, -5.24) * mm, "end": v(-30.68, -5.27) * mm});
            skLineSegment(sketch, "E1700", {"start": v(-30.68, -5.27) * mm, "end": v(-30.57, -5.31) * mm});
            skLineSegment(sketch, "E1701", {"start": v(-30.57, -5.31) * mm, "end": v(-30.46, -5.4) * mm});
            skLineSegment(sketch, "E1702", {"start": v(-30.46, -5.4) * mm, "end": v(-30.36, -5.5) * mm});
            skLineSegment(sketch, "E1703", {"start": v(-30.36, -5.5) * mm, "end": v(-30.3, -5.63) * mm});
            skLineSegment(sketch, "E1704", {"start": v(-30.3, -5.63) * mm, "end": v(-30.26, -5.77) * mm});
            skLineSegment(sketch, "E1705", {"start": v(-30.26, -5.77) * mm, "end": v(-30.24, -5.92) * mm});
            skLineSegment(sketch, "E1706", {"start": v(-30.24, -5.92) * mm, "end": v(-30.26, -6.06) * mm});
            skLineSegment(sketch, "E1707", {"start": v(-30.26, -6.06) * mm, "end": v(-30.3, -6.2) * mm});
            skLineSegment(sketch, "E1708", {"start": v(-30.3, -6.2) * mm, "end": v(-30.38, -6.32) * mm});
            skLineSegment(sketch, "E1709", {"start": v(-30.38, -6.32) * mm, "end": v(-30.46, -6.4) * mm});
            skLineSegment(sketch, "E1710", {"start": v(-30.46, -6.4) * mm, "end": v(-30.55, -6.46) * mm});
            skLineSegment(sketch, "E1711", {"start": v(-30.55, -6.46) * mm, "end": v(-30.65, -6.51) * mm});
            skLineSegment(sketch, "E1712", {"start": v(-30.65, -6.51) * mm, "end": v(-30.75, -6.56) * mm});
            skLineSegment(sketch, "E1713", {"start": v(-30.75, -6.56) * mm, "end": v(-30.83, -6.63) * mm});
            skLineSegment(sketch, "E1714", {"start": v(-30.83, -6.63) * mm, "end": v(-30.85, -6.74) * mm});
            skLineSegment(sketch, "E1715", {"start": v(-30.85, -6.74) * mm, "end": v(-30.82, -6.89) * mm});
            skLineSegment(sketch, "E1716", {"start": v(-30.82, -6.89) * mm, "end": v(-30.78, -7.03) * mm});
            skLineSegment(sketch, "E1717", {"start": v(-30.78, -7.03) * mm, "end": v(-30.72, -7.13) * mm});
            skLineSegment(sketch, "E1718", {"start": v(-30.72, -7.13) * mm, "end": v(-30.62, -7.16) * mm});
            skLineSegment(sketch, "E1719", {"start": v(-30.62, -7.16) * mm, "end": v(-30.5, -7.16) * mm});
            skLineSegment(sketch, "E1720", {"start": v(-30.5, -7.16) * mm, "end": v(-30.4, -7.16) * mm});
            skLineSegment(sketch, "E1721", {"start": v(-30.4, -7.16) * mm, "end": v(-30.29, -7.19) * mm});
            skLineSegment(sketch, "E1722", {"start": v(-30.29, -7.19) * mm, "end": v(-30.18, -7.22) * mm});
            skLineSegment(sketch, "E1723", {"start": v(-30.18, -7.22) * mm, "end": v(-30.06, -7.3) * mm});
            skLineSegment(sketch, "E1724", {"start": v(-30.06, -7.3) * mm, "end": v(-29.96, -7.4) * mm});
            skLineSegment(sketch, "E1725", {"start": v(-29.96, -7.4) * mm, "end": v(-29.88, -7.52) * mm});
            skLineSegment(sketch, "E1726", {"start": v(-29.88, -7.52) * mm, "end": v(-29.83, -7.66) * mm});
            skLineSegment(sketch, "E1727", {"start": v(-29.83, -7.66) * mm, "end": v(-29.81, -7.8) * mm});
            skLineSegment(sketch, "E1728", {"start": v(-29.81, -7.8) * mm, "end": v(-29.82, -7.95) * mm});
            skLineSegment(sketch, "E1729", {"start": v(-29.82, -7.95) * mm, "end": v(-29.86, -8.09) * mm});
            skLineSegment(sketch, "E1730", {"start": v(-29.86, -8.09) * mm, "end": v(-29.92, -8.21) * mm});
            skLineSegment(sketch, "E1731", {"start": v(-29.92, -8.21) * mm, "end": v(-30, -8.3) * mm});
            skLineSegment(sketch, "E1732", {"start": v(-30, -8.3) * mm, "end": v(-30.09, -8.37) * mm});
            skLineSegment(sketch, "E1733", {"start": v(-30.09, -8.37) * mm, "end": v(-30.18, -8.43) * mm});
            skLineSegment(sketch, "E1734", {"start": v(-30.18, -8.43) * mm, "end": v(-30.28, -8.47) * mm});
            skLineSegment(sketch, "E1735", {"start": v(-30.28, -8.47) * mm, "end": v(-30.36, -8.55) * mm});
            skLineSegment(sketch, "E1736", {"start": v(-30.36, -8.55) * mm, "end": v(-30.36, -8.67) * mm});
            skLineSegment(sketch, "E1737", {"start": v(-30.36, -8.67) * mm, "end": v(-30.32, -8.8) * mm});
            skLineSegment(sketch, "E1738", {"start": v(-30.32, -8.8) * mm, "end": v(-30.28, -8.95) * mm});
            skLineSegment(sketch, "E1739", {"start": v(-30.28, -8.95) * mm, "end": v(-30.21, -9.04) * mm});
            skLineSegment(sketch, "E1740", {"start": v(-30.21, -9.04) * mm, "end": v(-30.1, -9.07) * mm});
            skLineSegment(sketch, "E1741", {"start": v(-30.1, -9.07) * mm, "end": v(-30, -9.06) * mm});
            skLineSegment(sketch, "E1742", {"start": v(-30, -9.06) * mm, "end": v(-29.89, -9.06) * mm});
            skLineSegment(sketch, "E1743", {"start": v(-29.89, -9.06) * mm, "end": v(-29.78, -9.07) * mm});
            skLineSegment(sketch, "E1744", {"start": v(-29.78, -9.07) * mm, "end": v(-29.67, -9.1) * mm});
            skLineSegment(sketch, "E1745", {"start": v(-29.67, -9.1) * mm, "end": v(-29.54, -9.17) * mm});
            skLineSegment(sketch, "E1746", {"start": v(-29.54, -9.17) * mm, "end": v(-29.44, -9.27) * mm});
            skLineSegment(sketch, "E1747", {"start": v(-29.44, -9.27) * mm, "end": v(-29.35, -9.39) * mm});
            skLineSegment(sketch, "E1748", {"start": v(-29.35, -9.39) * mm, "end": v(-29.3, -9.52) * mm});
            skLineSegment(sketch, "E1749", {"start": v(-29.3, -9.52) * mm, "end": v(-29.26, -9.66) * mm});
            skLineSegment(sketch, "E1750", {"start": v(-29.26, -9.66) * mm, "end": v(-29.26, -9.8) * mm});
            skLineSegment(sketch, "E1751", {"start": v(-29.26, -9.8) * mm, "end": v(-29.29, -9.94) * mm});
            skLineSegment(sketch, "E1752", {"start": v(-29.29, -9.94) * mm, "end": v(-29.35, -10.07) * mm});
            skLineSegment(sketch, "E1753", {"start": v(-29.35, -10.07) * mm, "end": v(-29.42, -10.16) * mm});
            skLineSegment(sketch, "E1754", {"start": v(-29.42, -10.16) * mm, "end": v(-29.5, -10.24) * mm});
            skLineSegment(sketch, "E1755", {"start": v(-29.5, -10.24) * mm, "end": v(-29.6, -10.3) * mm});
            skLineSegment(sketch, "E1756", {"start": v(-29.6, -10.3) * mm, "end": v(-29.69, -10.36) * mm});
            skLineSegment(sketch, "E1757", {"start": v(-29.69, -10.36) * mm, "end": v(-29.76, -10.44) * mm});
            skLineSegment(sketch, "E1758", {"start": v(-29.76, -10.44) * mm, "end": v(-29.76, -10.56) * mm});
            skLineSegment(sketch, "E1759", {"start": v(-29.76, -10.56) * mm, "end": v(-29.71, -10.7) * mm});
            skLineSegment(sketch, "E1760", {"start": v(-29.71, -10.7) * mm, "end": v(-29.66, -10.83) * mm});
            skLineSegment(sketch, "E1761", {"start": v(-29.66, -10.83) * mm, "end": v(-29.58, -10.92) * mm});
            skLineSegment(sketch, "E1762", {"start": v(-29.58, -10.92) * mm, "end": v(-29.48, -10.94) * mm});
            skLineSegment(sketch, "E1763", {"start": v(-29.48, -10.94) * mm, "end": v(-29.37, -10.92) * mm});
            skLineSegment(sketch, "E1764", {"start": v(-29.37, -10.92) * mm, "end": v(-29.26, -10.92) * mm});
            skLineSegment(sketch, "E1765", {"start": v(-29.26, -10.92) * mm, "end": v(-29.15, -10.92) * mm});
            skLineSegment(sketch, "E1766", {"start": v(-29.15, -10.92) * mm, "end": v(-29.04, -10.95) * mm});
            skLineSegment(sketch, "E1767", {"start": v(-29.04, -10.95) * mm, "end": v(-28.9, -11) * mm});
            skLineSegment(sketch, "E1768", {"start": v(-28.9, -11) * mm, "end": v(-28.8, -11.1) * mm});
            skLineSegment(sketch, "E1769", {"start": v(-28.8, -11.1) * mm, "end": v(-28.7, -11.2) * mm});
            skLineSegment(sketch, "E1770", {"start": v(-28.7, -11.2) * mm, "end": v(-28.64, -11.34) * mm});
            skLineSegment(sketch, "E1771", {"start": v(-28.64, -11.34) * mm, "end": v(-28.6, -11.48) * mm});
            skLineSegment(sketch, "E1772", {"start": v(-28.6, -11.48) * mm, "end": v(-28.59, -11.62) * mm});
            skLineSegment(sketch, "E1773", {"start": v(-28.59, -11.62) * mm, "end": v(-28.6, -11.76) * mm});
            skLineSegment(sketch, "E1774", {"start": v(-28.6, -11.76) * mm, "end": v(-28.66, -11.9) * mm});
            skLineSegment(sketch, "E1775", {"start": v(-28.66, -11.9) * mm, "end": v(-28.73, -11.99) * mm});
            skLineSegment(sketch, "E1776", {"start": v(-28.73, -11.99) * mm, "end": v(-28.8, -12.07) * mm});
            skLineSegment(sketch, "E1777", {"start": v(-28.8, -12.07) * mm, "end": v(-28.89, -12.14) * mm});
            skLineSegment(sketch, "E1778", {"start": v(-28.89, -12.14) * mm, "end": v(-28.98, -12.2) * mm});
            skLineSegment(sketch, "E1779", {"start": v(-28.98, -12.2) * mm, "end": v(-29.04, -12.29) * mm});
            skLineSegment(sketch, "E1780", {"start": v(-29.04, -12.29) * mm, "end": v(-29.04, -12.4) * mm});
            skLineSegment(sketch, "E1781", {"start": v(-29.04, -12.4) * mm, "end": v(-28.98, -12.54) * mm});
            skLineSegment(sketch, "E1782", {"start": v(-28.98, -12.54) * mm, "end": v(-28.92, -12.68) * mm});
            skLineSegment(sketch, "E1783", {"start": v(-28.92, -12.68) * mm, "end": v(-28.84, -12.76) * mm});
            skLineSegment(sketch, "E1784", {"start": v(-28.84, -12.76) * mm, "end": v(-28.73, -12.77) * mm});
            skLineSegment(sketch, "E1785", {"start": v(-28.73, -12.77) * mm, "end": v(-28.62, -12.74) * mm});
            skLineSegment(sketch, "E1786", {"start": v(-28.62, -12.74) * mm, "end": v(-28.52, -12.73) * mm});
            skLineSegment(sketch, "E1787", {"start": v(-28.52, -12.73) * mm, "end": v(-28.4, -12.73) * mm});
            skLineSegment(sketch, "E1788", {"start": v(-28.4, -12.73) * mm, "end": v(-28.3, -12.75) * mm});
            skLineSegment(sketch, "E1789", {"start": v(-28.3, -12.75) * mm, "end": v(-28.16, -12.8) * mm});
            skLineSegment(sketch, "E1790", {"start": v(-28.16, -12.8) * mm, "end": v(-28.04, -12.88) * mm});
            skLineSegment(sketch, "E1791", {"start": v(-28.04, -12.88) * mm, "end": v(-27.94, -13) * mm});
            skLineSegment(sketch, "E1792", {"start": v(-27.94, -13) * mm, "end": v(-27.87, -13.11) * mm});
            skLineSegment(sketch, "E1793", {"start": v(-27.87, -13.11) * mm, "end": v(-27.82, -13.25) * mm});
            skLineSegment(sketch, "E1794", {"start": v(-27.82, -13.25) * mm, "end": v(-27.8, -13.4) * mm});
            skLineSegment(sketch, "E1795", {"start": v(-27.8, -13.4) * mm, "end": v(-27.81, -13.54) * mm});
            skLineSegment(sketch, "E1796", {"start": v(-27.81, -13.54) * mm, "end": v(-27.86, -13.67) * mm});
            skLineSegment(sketch, "E1797", {"start": v(-27.86, -13.67) * mm, "end": v(-27.92, -13.77) * mm});
            skLineSegment(sketch, "E1798", {"start": v(-27.92, -13.77) * mm, "end": v(-27.99, -13.86) * mm});
            skLineSegment(sketch, "E1799", {"start": v(-27.99, -13.86) * mm, "end": v(-28.07, -13.93) * mm});
            skLineSegment(sketch, "E1800", {"start": v(-28.07, -13.93) * mm, "end": v(-28.15, -14) * mm});
            skLineSegment(sketch, "E1801", {"start": v(-28.15, -14) * mm, "end": v(-28.21, -14.09) * mm});
            skLineSegment(sketch, "E1802", {"start": v(-28.21, -14.09) * mm, "end": v(-28.2, -14.2) * mm});
            skLineSegment(sketch, "E1803", {"start": v(-28.2, -14.2) * mm, "end": v(-28.14, -14.34) * mm});
            skLineSegment(sketch, "E1804", {"start": v(-28.14, -14.34) * mm, "end": v(-28.07, -14.47) * mm});
            skLineSegment(sketch, "E1805", {"start": v(-28.07, -14.47) * mm, "end": v(-27.98, -14.55) * mm});
            skLineSegment(sketch, "E1806", {"start": v(-27.98, -14.55) * mm, "end": v(-27.87, -14.55) * mm});
            skLineSegment(sketch, "E1807", {"start": v(-27.87, -14.55) * mm, "end": v(-27.77, -14.52) * mm});
            skLineSegment(sketch, "E1808", {"start": v(-27.77, -14.52) * mm, "end": v(-27.66, -14.5) * mm});
            skLineSegment(sketch, "E1809", {"start": v(-27.66, -14.5) * mm, "end": v(-27.55, -14.5) * mm});
            skLineSegment(sketch, "E1810", {"start": v(-27.55, -14.5) * mm, "end": v(-27.43, -14.5) * mm});
            skLineSegment(sketch, "E1811", {"start": v(-27.43, -14.5) * mm, "end": v(-27.3, -14.54) * mm});
            skLineSegment(sketch, "E1812", {"start": v(-27.3, -14.54) * mm, "end": v(-27.18, -14.62) * mm});
            skLineSegment(sketch, "E1813", {"start": v(-27.18, -14.62) * mm, "end": v(-27.07, -14.72) * mm});
            skLineSegment(sketch, "E1814", {"start": v(-27.07, -14.72) * mm, "end": v(-27, -14.84) * mm});
            skLineSegment(sketch, "E1815", {"start": v(-27, -14.84) * mm, "end": v(-26.93, -14.97) * mm});
            skLineSegment(sketch, "E1816", {"start": v(-26.93, -14.97) * mm, "end": v(-26.9, -15.11) * mm});
            skLineSegment(sketch, "E1817", {"start": v(-26.9, -15.11) * mm, "end": v(-26.9, -15.26) * mm});
            skLineSegment(sketch, "E1818", {"start": v(-26.9, -15.26) * mm, "end": v(-26.94, -15.4) * mm});
            skLineSegment(sketch, "E1819", {"start": v(-26.94, -15.4) * mm, "end": v(-27, -15.5) * mm});
            skLineSegment(sketch, "E1820", {"start": v(-27, -15.5) * mm, "end": v(-27.06, -15.59) * mm});
            skLineSegment(sketch, "E1821", {"start": v(-27.06, -15.59) * mm, "end": v(-27.14, -15.67) * mm});
            skLineSegment(sketch, "E1822", {"start": v(-27.14, -15.67) * mm, "end": v(-27.22, -15.74) * mm});
            skLineSegment(sketch, "E1823", {"start": v(-27.22, -15.74) * mm, "end": v(-27.27, -15.83) * mm});
            skLineSegment(sketch, "E1824", {"start": v(-27.27, -15.83) * mm, "end": v(-27.25, -15.95) * mm});
            skLineSegment(sketch, "E1825", {"start": v(-27.25, -15.95) * mm, "end": v(-27.18, -16.07) * mm});
            skLineSegment(sketch, "E1826", {"start": v(-27.18, -16.07) * mm, "end": v(-27.1, -16.2) * mm});
            skLineSegment(sketch, "E1827", {"start": v(-27.1, -16.2) * mm, "end": v(-27.01, -16.27) * mm});
            skLineSegment(sketch, "E1828", {"start": v(-27.01, -16.27) * mm, "end": v(-26.9, -16.27) * mm});
            skLineSegment(sketch, "E1829", {"start": v(-26.9, -16.27) * mm, "end": v(-26.8, -16.23) * mm});
            skLineSegment(sketch, "E1830", {"start": v(-26.8, -16.23) * mm, "end": v(-26.7, -16.2) * mm});
            skLineSegment(sketch, "E1831", {"start": v(-26.7, -16.2) * mm, "end": v(-26.58, -16.2) * mm});
            skLineSegment(sketch, "E1832", {"start": v(-26.58, -16.2) * mm, "end": v(-26.47, -16.2) * mm});
            skLineSegment(sketch, "E1833", {"start": v(-26.47, -16.2) * mm, "end": v(-26.33, -16.23) * mm});
            skLineSegment(sketch, "E1834", {"start": v(-26.33, -16.23) * mm, "end": v(-26.2, -16.3) * mm});
            skLineSegment(sketch, "E1835", {"start": v(-26.2, -16.3) * mm, "end": v(-26.1, -16.4) * mm});
            skLineSegment(sketch, "E1836", {"start": v(-26.1, -16.4) * mm, "end": v(-26, -16.5) * mm});
            skLineSegment(sketch, "E1837", {"start": v(-26, -16.5) * mm, "end": v(-25.94, -16.63) * mm});
            skLineSegment(sketch, "E1838", {"start": v(-25.94, -16.63) * mm, "end": v(-25.9, -16.77) * mm});
            skLineSegment(sketch, "E1839", {"start": v(-25.9, -16.77) * mm, "end": v(-25.9, -16.92) * mm});
            skLineSegment(sketch, "E1840", {"start": v(-25.9, -16.92) * mm, "end": v(-25.92, -17.06) * mm});
            skLineSegment(sketch, "E1841", {"start": v(-25.92, -17.06) * mm, "end": v(-25.97, -17.16) * mm});
            skLineSegment(sketch, "E1842", {"start": v(-25.97, -17.16) * mm, "end": v(-26.03, -17.25) * mm});
            skLineSegment(sketch, "E1843", {"start": v(-26.03, -17.25) * mm, "end": v(-26.1, -17.34) * mm});
            skLineSegment(sketch, "E1844", {"start": v(-26.1, -17.34) * mm, "end": v(-26.18, -17.42) * mm});
            skLineSegment(sketch, "E1845", {"start": v(-26.18, -17.42) * mm, "end": v(-26.23, -17.51) * mm});
            skLineSegment(sketch, "E1846", {"start": v(-26.23, -17.51) * mm, "end": v(-26.2, -17.63) * mm});
            skLineSegment(sketch, "E1847", {"start": v(-26.2, -17.63) * mm, "end": v(-26.12, -17.75) * mm});
            skLineSegment(sketch, "E1848", {"start": v(-26.12, -17.75) * mm, "end": v(-26.03, -17.87) * mm});
            skLineSegment(sketch, "E1849", {"start": v(-26.03, -17.87) * mm, "end": v(-25.94, -17.94) * mm});
            skLineSegment(sketch, "E1850", {"start": v(-25.94, -17.94) * mm, "end": v(-25.83, -17.93) * mm});
            skLineSegment(sketch, "E1851", {"start": v(-25.83, -17.93) * mm, "end": v(-25.73, -17.88) * mm});
            skLineSegment(sketch, "E1852", {"start": v(-25.73, -17.88) * mm, "end": v(-25.62, -17.85) * mm});
            skLineSegment(sketch, "E1853", {"start": v(-25.62, -17.85) * mm, "end": v(-25.51, -17.83) * mm});
            skLineSegment(sketch, "E1854", {"start": v(-25.51, -17.83) * mm, "end": v(-25.4, -17.82) * mm});
            skLineSegment(sketch, "E1855", {"start": v(-25.4, -17.82) * mm, "end": v(-25.26, -17.85) * mm});
            skLineSegment(sketch, "E1856", {"start": v(-25.26, -17.85) * mm, "end": v(-25.13, -17.91) * mm});
            skLineSegment(sketch, "E1857", {"start": v(-25.13, -17.91) * mm, "end": v(-25.02, -18) * mm});
            skLineSegment(sketch, "E1858", {"start": v(-25.02, -18) * mm, "end": v(-24.92, -18.1) * mm});
            skLineSegment(sketch, "E1859", {"start": v(-24.92, -18.1) * mm, "end": v(-24.85, -18.23) * mm});
            skLineSegment(sketch, "E1860", {"start": v(-24.85, -18.23) * mm, "end": v(-24.8, -18.37) * mm});
            skLineSegment(sketch, "E1861", {"start": v(-24.8, -18.37) * mm, "end": v(-24.78, -18.5) * mm});
            skLineSegment(sketch, "E1862", {"start": v(-24.78, -18.5) * mm, "end": v(-24.8, -18.65) * mm});
            skLineSegment(sketch, "E1863", {"start": v(-24.8, -18.65) * mm, "end": v(-24.84, -18.76) * mm});
            skLineSegment(sketch, "E1864", {"start": v(-24.84, -18.76) * mm, "end": v(-24.9, -18.85) * mm});
            skLineSegment(sketch, "E1865", {"start": v(-24.9, -18.85) * mm, "end": v(-24.96, -18.94) * mm});
            skLineSegment(sketch, "E1866", {"start": v(-24.96, -18.94) * mm, "end": v(-25.03, -19.03) * mm});
            skLineSegment(sketch, "E1867", {"start": v(-25.03, -19.03) * mm, "end": v(-25.08, -19.13) * mm});
            skLineSegment(sketch, "E1868", {"start": v(-25.08, -19.13) * mm, "end": v(-25.04, -19.24) * mm});
            skLineSegment(sketch, "E1869", {"start": v(-25.04, -19.24) * mm, "end": v(-24.95, -19.35) * mm});
            skLineSegment(sketch, "E1870", {"start": v(-24.95, -19.35) * mm, "end": v(-24.86, -19.47) * mm});
            skLineSegment(sketch, "E1871", {"start": v(-24.86, -19.47) * mm, "end": v(-24.76, -19.53) * mm});
            skLineSegment(sketch, "E1872", {"start": v(-24.76, -19.53) * mm, "end": v(-24.65, -19.51) * mm});
            skLineSegment(sketch, "E1873", {"start": v(-24.65, -19.51) * mm, "end": v(-24.56, -19.46) * mm});
            skLineSegment(sketch, "E1874", {"start": v(-24.56, -19.46) * mm, "end": v(-24.45, -19.42) * mm});
            skLineSegment(sketch, "E1875", {"start": v(-24.45, -19.42) * mm, "end": v(-24.34, -19.4) * mm});
            skLineSegment(sketch, "E1876", {"start": v(-24.34, -19.4) * mm, "end": v(-24.23, -19.38) * mm});
            skLineSegment(sketch, "E1877", {"start": v(-24.23, -19.38) * mm, "end": v(-24.09, -19.4) * mm});
            skLineSegment(sketch, "E1878", {"start": v(-24.09, -19.4) * mm, "end": v(-23.96, -19.45) * mm});
            skLineSegment(sketch, "E1879", {"start": v(-23.96, -19.45) * mm, "end": v(-23.84, -19.53) * mm});
            skLineSegment(sketch, "E1880", {"start": v(-23.84, -19.53) * mm, "end": v(-23.73, -19.63) * mm});
            skLineSegment(sketch, "E1881", {"start": v(-23.73, -19.63) * mm, "end": v(-23.65, -19.75) * mm});
            skLineSegment(sketch, "E1882", {"start": v(-23.65, -19.75) * mm, "end": v(-23.6, -19.89) * mm});
            skLineSegment(sketch, "E1883", {"start": v(-23.6, -19.89) * mm, "end": v(-23.57, -20.03) * mm});
            skLineSegment(sketch, "E1884", {"start": v(-23.57, -20.03) * mm, "end": v(-23.58, -20.17) * mm});
            skLineSegment(sketch, "E1885", {"start": v(-23.58, -20.17) * mm, "end": v(-23.62, -20.28) * mm});
            skLineSegment(sketch, "E1886", {"start": v(-23.62, -20.28) * mm, "end": v(-23.66, -20.38) * mm});
            skLineSegment(sketch, "E1887", {"start": v(-23.66, -20.38) * mm, "end": v(-23.72, -20.47) * mm});
            skLineSegment(sketch, "E1888", {"start": v(-23.72, -20.47) * mm, "end": v(-23.79, -20.56) * mm});
            skLineSegment(sketch, "E1889", {"start": v(-23.79, -20.56) * mm, "end": v(-23.82, -20.66) * mm});
            skLineSegment(sketch, "E1890", {"start": v(-23.82, -20.66) * mm, "end": v(-23.78, -20.77) * mm});
            skLineSegment(sketch, "E1891", {"start": v(-23.78, -20.77) * mm, "end": v(-23.69, -20.88) * mm});
            skLineSegment(sketch, "E1892", {"start": v(-23.69, -20.88) * mm, "end": v(-23.59, -21) * mm});
            skLineSegment(sketch, "E1893", {"start": v(-23.59, -21) * mm, "end": v(-23.49, -21.05) * mm});
            skLineSegment(sketch, "E1894", {"start": v(-23.49, -21.05) * mm, "end": v(-23.38, -21.02) * mm});
            skLineSegment(sketch, "E1895", {"start": v(-23.38, -21.02) * mm, "end": v(-23.29, -20.97) * mm});
            skLineSegment(sketch, "E1896", {"start": v(-23.29, -20.97) * mm, "end": v(-23.19, -20.92) * mm});
            skLineSegment(sketch, "E1897", {"start": v(-23.19, -20.92) * mm, "end": v(-23.08, -20.89) * mm});
            skLineSegment(sketch, "E1898", {"start": v(-23.08, -20.89) * mm, "end": v(-22.97, -20.87) * mm});
            skLineSegment(sketch, "E1899", {"start": v(-22.97, -20.87) * mm, "end": v(-22.82, -20.88) * mm});
            skLineSegment(sketch, "E1900", {"start": v(-22.82, -20.88) * mm, "end": v(-22.69, -20.92) * mm});
            skLineSegment(sketch, "E1901", {"start": v(-22.69, -20.92) * mm, "end": v(-22.56, -20.99) * mm});
            skLineSegment(sketch, "E1902", {"start": v(-22.56, -20.99) * mm, "end": v(-22.45, -21.08) * mm});
            skLineSegment(sketch, "E1903", {"start": v(-22.45, -21.08) * mm, "end": v(-22.36, -21.2) * mm});
            skLineSegment(sketch, "E1904", {"start": v(-22.36, -21.2) * mm, "end": v(-22.3, -21.33) * mm});
            skLineSegment(sketch, "E1905", {"start": v(-22.3, -21.33) * mm, "end": v(-22.27, -21.47) * mm});
            skLineSegment(sketch, "E1906", {"start": v(-22.27, -21.47) * mm, "end": v(-22.27, -21.61) * mm});
            skLineSegment(sketch, "E1907", {"start": v(-22.27, -21.61) * mm, "end": v(-22.3, -21.72) * mm});
            skLineSegment(sketch, "E1908", {"start": v(-22.3, -21.72) * mm, "end": v(-22.34, -21.83) * mm});
            skLineSegment(sketch, "E1909", {"start": v(-22.34, -21.83) * mm, "end": v(-22.39, -21.92) * mm});
            skLineSegment(sketch, "E1910", {"start": v(-22.39, -21.92) * mm, "end": v(-22.45, -22.01) * mm});
            skLineSegment(sketch, "E1911", {"start": v(-22.45, -22.01) * mm, "end": v(-22.48, -22.12) * mm});
            skLineSegment(sketch, "E1912", {"start": v(-22.48, -22.12) * mm, "end": v(-22.43, -22.22) * mm});
            skLineSegment(sketch, "E1913", {"start": v(-22.43, -22.22) * mm, "end": v(-22.33, -22.33) * mm});
            skLineSegment(sketch, "E1914", {"start": v(-22.33, -22.33) * mm, "end": v(-22.22, -22.43) * mm});
            skLineSegment(sketch, "E1915", {"start": v(-22.22, -22.43) * mm, "end": v(-22.12, -22.48) * mm});
            skLineSegment(sketch, "E1916", {"start": v(-22.12, -22.48) * mm, "end": v(-22.01, -22.45) * mm});
            skLineSegment(sketch, "E1917", {"start": v(-22.01, -22.45) * mm, "end": v(-21.92, -22.39) * mm});
            skLineSegment(sketch, "E1918", {"start": v(-21.92, -22.39) * mm, "end": v(-21.83, -22.34) * mm});
            skLineSegment(sketch, "E1919", {"start": v(-21.83, -22.34) * mm, "end": v(-21.72, -22.3) * mm});
            skLineSegment(sketch, "E1920", {"start": v(-21.72, -22.3) * mm, "end": v(-21.61, -22.27) * mm});
            skLineSegment(sketch, "E1921", {"start": v(-21.61, -22.27) * mm, "end": v(-21.47, -22.27) * mm});
            skLineSegment(sketch, "E1922", {"start": v(-21.47, -22.27) * mm, "end": v(-21.33, -22.3) * mm});
            skLineSegment(sketch, "E1923", {"start": v(-21.33, -22.3) * mm, "end": v(-21.2, -22.36) * mm});
            skLineSegment(sketch, "E1924", {"start": v(-21.2, -22.36) * mm, "end": v(-21.08, -22.45) * mm});
            skLineSegment(sketch, "E1925", {"start": v(-21.08, -22.45) * mm, "end": v(-20.99, -22.56) * mm});
            skLineSegment(sketch, "E1926", {"start": v(-20.99, -22.56) * mm, "end": v(-20.92, -22.69) * mm});
            skLineSegment(sketch, "E1927", {"start": v(-20.92, -22.69) * mm, "end": v(-20.88, -22.82) * mm});
            skLineSegment(sketch, "E1928", {"start": v(-20.88, -22.82) * mm, "end": v(-20.87, -22.97) * mm});
            skLineSegment(sketch, "E1929", {"start": v(-20.87, -22.97) * mm, "end": v(-20.89, -23.08) * mm});
            skLineSegment(sketch, "E1930", {"start": v(-20.89, -23.08) * mm, "end": v(-20.92, -23.19) * mm});
            skLineSegment(sketch, "E1931", {"start": v(-20.92, -23.19) * mm, "end": v(-20.97, -23.29) * mm});
            skLineSegment(sketch, "E1932", {"start": v(-20.97, -23.29) * mm, "end": v(-21.02, -23.38) * mm});
            skLineSegment(sketch, "E1933", {"start": v(-21.02, -23.38) * mm, "end": v(-21.05, -23.49) * mm});
            skLineSegment(sketch, "E1934", {"start": v(-21.05, -23.49) * mm, "end": v(-21, -23.59) * mm});
            skLineSegment(sketch, "E1935", {"start": v(-21, -23.59) * mm, "end": v(-20.88, -23.69) * mm});
            skLineSegment(sketch, "E1936", {"start": v(-20.88, -23.69) * mm, "end": v(-20.77, -23.78) * mm});
            skLineSegment(sketch, "E1937", {"start": v(-20.77, -23.78) * mm, "end": v(-20.66, -23.82) * mm});
            skLineSegment(sketch, "E1938", {"start": v(-20.66, -23.82) * mm, "end": v(-20.56, -23.79) * mm});
            skLineSegment(sketch, "E1939", {"start": v(-20.56, -23.79) * mm, "end": v(-20.47, -23.72) * mm});
            skLineSegment(sketch, "E1940", {"start": v(-20.47, -23.72) * mm, "end": v(-20.38, -23.66) * mm});
            skLineSegment(sketch, "E1941", {"start": v(-20.38, -23.66) * mm, "end": v(-20.28, -23.62) * mm});
            skLineSegment(sketch, "E1942", {"start": v(-20.28, -23.62) * mm, "end": v(-20.17, -23.58) * mm});
            skLineSegment(sketch, "E1943", {"start": v(-20.17, -23.58) * mm, "end": v(-20.03, -23.57) * mm});
            skLineSegment(sketch, "E1944", {"start": v(-20.03, -23.57) * mm, "end": v(-19.89, -23.6) * mm});
            skLineSegment(sketch, "E1945", {"start": v(-19.89, -23.6) * mm, "end": v(-19.75, -23.65) * mm});
            skLineSegment(sketch, "E1946", {"start": v(-19.75, -23.65) * mm, "end": v(-19.63, -23.73) * mm});
            skLineSegment(sketch, "E1947", {"start": v(-19.63, -23.73) * mm, "end": v(-19.53, -23.84) * mm});
            skLineSegment(sketch, "E1948", {"start": v(-19.53, -23.84) * mm, "end": v(-19.45, -23.96) * mm});
            skLineSegment(sketch, "E1949", {"start": v(-19.45, -23.96) * mm, "end": v(-19.4, -24.09) * mm});
            skLineSegment(sketch, "E1950", {"start": v(-19.4, -24.09) * mm, "end": v(-19.38, -24.23) * mm});
            skLineSegment(sketch, "E1951", {"start": v(-19.38, -24.23) * mm, "end": v(-19.4, -24.34) * mm});
            skLineSegment(sketch, "E1952", {"start": v(-19.4, -24.34) * mm, "end": v(-19.42, -24.45) * mm});
            skLineSegment(sketch, "E1953", {"start": v(-19.42, -24.45) * mm, "end": v(-19.46, -24.56) * mm});
            skLineSegment(sketch, "E1954", {"start": v(-19.46, -24.56) * mm, "end": v(-19.51, -24.65) * mm});
            skLineSegment(sketch, "E1955", {"start": v(-19.51, -24.65) * mm, "end": v(-19.53, -24.76) * mm});
            skLineSegment(sketch, "E1956", {"start": v(-19.53, -24.76) * mm, "end": v(-19.47, -24.86) * mm});
            skLineSegment(sketch, "E1957", {"start": v(-19.47, -24.86) * mm, "end": v(-19.35, -24.95) * mm});
            skLineSegment(sketch, "E1958", {"start": v(-19.35, -24.95) * mm, "end": v(-19.24, -25.04) * mm});
            skLineSegment(sketch, "E1959", {"start": v(-19.24, -25.04) * mm, "end": v(-19.13, -25.08) * mm});
            skLineSegment(sketch, "E1960", {"start": v(-19.13, -25.08) * mm, "end": v(-19.03, -25.03) * mm});
            skLineSegment(sketch, "E1961", {"start": v(-19.03, -25.03) * mm, "end": v(-18.94, -24.96) * mm});
            skLineSegment(sketch, "E1962", {"start": v(-18.94, -24.96) * mm, "end": v(-18.85, -24.9) * mm});
            skLineSegment(sketch, "E1963", {"start": v(-18.85, -24.9) * mm, "end": v(-18.76, -24.84) * mm});
            skLineSegment(sketch, "E1964", {"start": v(-18.76, -24.84) * mm, "end": v(-18.65, -24.8) * mm});
            skLineSegment(sketch, "E1965", {"start": v(-18.65, -24.8) * mm, "end": v(-18.5, -24.78) * mm});
            skLineSegment(sketch, "E1966", {"start": v(-18.5, -24.78) * mm, "end": v(-18.37, -24.8) * mm});
            skLineSegment(sketch, "E1967", {"start": v(-18.37, -24.8) * mm, "end": v(-18.23, -24.85) * mm});
            skLineSegment(sketch, "E1968", {"start": v(-18.23, -24.85) * mm, "end": v(-18.1, -24.92) * mm});
            skLineSegment(sketch, "E1969", {"start": v(-18.1, -24.92) * mm, "end": v(-18, -25.02) * mm});
            skLineSegment(sketch, "E1970", {"start": v(-18, -25.02) * mm, "end": v(-17.91, -25.13) * mm});
            skLineSegment(sketch, "E1971", {"start": v(-17.91, -25.13) * mm, "end": v(-17.85, -25.26) * mm});
            skLineSegment(sketch, "E1972", {"start": v(-17.85, -25.26) * mm, "end": v(-17.82, -25.4) * mm});
            skLineSegment(sketch, "E1973", {"start": v(-17.82, -25.4) * mm, "end": v(-17.83, -25.51) * mm});
            skLineSegment(sketch, "E1974", {"start": v(-17.83, -25.51) * mm, "end": v(-17.85, -25.62) * mm});
            skLineSegment(sketch, "E1975", {"start": v(-17.85, -25.62) * mm, "end": v(-17.88, -25.73) * mm});
            skLineSegment(sketch, "E1976", {"start": v(-17.88, -25.73) * mm, "end": v(-17.93, -25.83) * mm});
            skLineSegment(sketch, "E1977", {"start": v(-17.93, -25.83) * mm, "end": v(-17.94, -25.94) * mm});
            skLineSegment(sketch, "E1978", {"start": v(-17.94, -25.94) * mm, "end": v(-17.87, -26.03) * mm});
            skLineSegment(sketch, "E1979", {"start": v(-17.87, -26.03) * mm, "end": v(-17.75, -26.12) * mm});
            skLineSegment(sketch, "E1980", {"start": v(-17.75, -26.12) * mm, "end": v(-17.63, -26.2) * mm});
            skLineSegment(sketch, "E1981", {"start": v(-17.63, -26.2) * mm, "end": v(-17.51, -26.23) * mm});
            skLineSegment(sketch, "E1982", {"start": v(-17.51, -26.23) * mm, "end": v(-17.42, -26.18) * mm});
            skLineSegment(sketch, "E1983", {"start": v(-17.42, -26.18) * mm, "end": v(-17.34, -26.1) * mm});
            skLineSegment(sketch, "E1984", {"start": v(-17.34, -26.1) * mm, "end": v(-17.25, -26.03) * mm});
            skLineSegment(sketch, "E1985", {"start": v(-17.25, -26.03) * mm, "end": v(-17.16, -25.97) * mm});
            skLineSegment(sketch, "E1986", {"start": v(-17.16, -25.97) * mm, "end": v(-17.06, -25.92) * mm});
            skLineSegment(sketch, "E1987", {"start": v(-17.06, -25.92) * mm, "end": v(-16.92, -25.9) * mm});
            skLineSegment(sketch, "E1988", {"start": v(-16.92, -25.9) * mm, "end": v(-16.77, -25.9) * mm});
            skLineSegment(sketch, "E1989", {"start": v(-16.77, -25.9) * mm, "end": v(-16.63, -25.94) * mm});
            skLineSegment(sketch, "E1990", {"start": v(-16.63, -25.94) * mm, "end": v(-16.5, -26) * mm});
            skLineSegment(sketch, "E1991", {"start": v(-16.5, -26) * mm, "end": v(-16.4, -26.1) * mm});
            skLineSegment(sketch, "E1992", {"start": v(-16.4, -26.1) * mm, "end": v(-16.3, -26.2) * mm});
            skLineSegment(sketch, "E1993", {"start": v(-16.3, -26.2) * mm, "end": v(-16.23, -26.33) * mm});
            skLineSegment(sketch, "E1994", {"start": v(-16.23, -26.33) * mm, "end": v(-16.2, -26.47) * mm});
            skLineSegment(sketch, "E1995", {"start": v(-16.2, -26.47) * mm, "end": v(-16.2, -26.58) * mm});
            skLineSegment(sketch, "E1996", {"start": v(-16.2, -26.58) * mm, "end": v(-16.2, -26.7) * mm});
            skLineSegment(sketch, "E1997", {"start": v(-16.2, -26.7) * mm, "end": v(-16.23, -26.8) * mm});
            skLineSegment(sketch, "E1998", {"start": v(-16.23, -26.8) * mm, "end": v(-16.27, -26.9) * mm});
            skLineSegment(sketch, "E1999", {"start": v(-16.27, -26.9) * mm, "end": v(-16.27, -27.01) * mm});
            skLineSegment(sketch, "E2000", {"start": v(-16.27, -27.01) * mm, "end": v(-16.2, -27.1) * mm});
            skLineSegment(sketch, "E2001", {"start": v(-16.2, -27.1) * mm, "end": v(-16.07, -27.18) * mm});
            skLineSegment(sketch, "E2002", {"start": v(-16.07, -27.18) * mm, "end": v(-15.95, -27.25) * mm});
            skLineSegment(sketch, "E2003", {"start": v(-15.95, -27.25) * mm, "end": v(-15.83, -27.27) * mm});
            skLineSegment(sketch, "E2004", {"start": v(-15.83, -27.27) * mm, "end": v(-15.74, -27.22) * mm});
            skLineSegment(sketch, "E2005", {"start": v(-15.74, -27.22) * mm, "end": v(-15.67, -27.14) * mm});
            skLineSegment(sketch, "E2006", {"start": v(-15.67, -27.14) * mm, "end": v(-15.59, -27.06) * mm});
            skLineSegment(sketch, "E2007", {"start": v(-15.59, -27.06) * mm, "end": v(-15.5, -27) * mm});
            skLineSegment(sketch, "E2008", {"start": v(-15.5, -27) * mm, "end": v(-15.4, -26.94) * mm});
            skLineSegment(sketch, "E2009", {"start": v(-15.4, -26.94) * mm, "end": v(-15.26, -26.9) * mm});
            skLineSegment(sketch, "E2010", {"start": v(-15.26, -26.9) * mm, "end": v(-15.11, -26.9) * mm});
            skLineSegment(sketch, "E2011", {"start": v(-15.11, -26.9) * mm, "end": v(-14.97, -26.93) * mm});
            skLineSegment(sketch, "E2012", {"start": v(-14.97, -26.93) * mm, "end": v(-14.84, -27) * mm});
            skLineSegment(sketch, "E2013", {"start": v(-14.84, -27) * mm, "end": v(-14.72, -27.07) * mm});
            skLineSegment(sketch, "E2014", {"start": v(-14.72, -27.07) * mm, "end": v(-14.62, -27.18) * mm});
            skLineSegment(sketch, "E2015", {"start": v(-14.62, -27.18) * mm, "end": v(-14.54, -27.3) * mm});
            skLineSegment(sketch, "E2016", {"start": v(-14.54, -27.3) * mm, "end": v(-14.5, -27.43) * mm});
            skLineSegment(sketch, "E2017", {"start": v(-14.5, -27.43) * mm, "end": v(-14.5, -27.55) * mm});
            skLineSegment(sketch, "E2018", {"start": v(-14.5, -27.55) * mm, "end": v(-14.5, -27.66) * mm});
            skLineSegment(sketch, "E2019", {"start": v(-14.5, -27.66) * mm, "end": v(-14.52, -27.77) * mm});
            skLineSegment(sketch, "E2020", {"start": v(-14.52, -27.77) * mm, "end": v(-14.55, -27.87) * mm});
            skLineSegment(sketch, "E2021", {"start": v(-14.55, -27.87) * mm, "end": v(-14.55, -27.98) * mm});
            skLineSegment(sketch, "E2022", {"start": v(-14.55, -27.98) * mm, "end": v(-14.47, -28.07) * mm});
            skLineSegment(sketch, "E2023", {"start": v(-14.47, -28.07) * mm, "end": v(-14.34, -28.14) * mm});
            skLineSegment(sketch, "E2024", {"start": v(-14.34, -28.14) * mm, "end": v(-14.2, -28.2) * mm});
            skLineSegment(sketch, "E2025", {"start": v(-14.2, -28.2) * mm, "end": v(-14.09, -28.21) * mm});
            skLineSegment(sketch, "E2026", {"start": v(-14.09, -28.21) * mm, "end": v(-14, -28.15) * mm});
            skLineSegment(sketch, "E2027", {"start": v(-14, -28.15) * mm, "end": v(-13.93, -28.07) * mm});
            skLineSegment(sketch, "E2028", {"start": v(-13.93, -28.07) * mm, "end": v(-13.86, -27.99) * mm});
            skLineSegment(sketch, "E2029", {"start": v(-13.86, -27.99) * mm, "end": v(-13.77, -27.92) * mm});
            skLineSegment(sketch, "E2030", {"start": v(-13.77, -27.92) * mm, "end": v(-13.67, -27.86) * mm});
            skLineSegment(sketch, "E2031", {"start": v(-13.67, -27.86) * mm, "end": v(-13.54, -27.81) * mm});
            skLineSegment(sketch, "E2032", {"start": v(-13.54, -27.81) * mm, "end": v(-13.4, -27.8) * mm});
            skLineSegment(sketch, "E2033", {"start": v(-13.4, -27.8) * mm, "end": v(-13.25, -27.82) * mm});
            skLineSegment(sketch, "E2034", {"start": v(-13.25, -27.82) * mm, "end": v(-13.11, -27.87) * mm});
            skLineSegment(sketch, "E2035", {"start": v(-13.11, -27.87) * mm, "end": v(-13, -27.94) * mm});
            skLineSegment(sketch, "E2036", {"start": v(-13, -27.94) * mm, "end": v(-12.88, -28.04) * mm});
            skLineSegment(sketch, "E2037", {"start": v(-12.88, -28.04) * mm, "end": v(-12.8, -28.16) * mm});
            skLineSegment(sketch, "E2038", {"start": v(-12.8, -28.16) * mm, "end": v(-12.75, -28.3) * mm});
            skLineSegment(sketch, "E2039", {"start": v(-12.75, -28.3) * mm, "end": v(-12.73, -28.4) * mm});
            skLineSegment(sketch, "E2040", {"start": v(-12.73, -28.4) * mm, "end": v(-12.73, -28.52) * mm});
            skLineSegment(sketch, "E2041", {"start": v(-12.73, -28.52) * mm, "end": v(-12.74, -28.62) * mm});
            skLineSegment(sketch, "E2042", {"start": v(-12.74, -28.62) * mm, "end": v(-12.77, -28.73) * mm});
            skLineSegment(sketch, "E2043", {"start": v(-12.77, -28.73) * mm, "end": v(-12.76, -28.84) * mm});
            skLineSegment(sketch, "E2044", {"start": v(-12.76, -28.84) * mm, "end": v(-12.68, -28.92) * mm});
            skLineSegment(sketch, "E2045", {"start": v(-12.68, -28.92) * mm, "end": v(-12.54, -28.98) * mm});
            skLineSegment(sketch, "E2046", {"start": v(-12.54, -28.98) * mm, "end": v(-12.4, -29.04) * mm});
            skLineSegment(sketch, "E2047", {"start": v(-12.4, -29.04) * mm, "end": v(-12.29, -29.04) * mm});
            skLineSegment(sketch, "E2048", {"start": v(-12.29, -29.04) * mm, "end": v(-12.2, -28.98) * mm});
            skLineSegment(sketch, "E2049", {"start": v(-12.2, -28.98) * mm, "end": v(-12.14, -28.89) * mm});
            skLineSegment(sketch, "E2050", {"start": v(-12.14, -28.89) * mm, "end": v(-12.07, -28.8) * mm});
            skLineSegment(sketch, "E2051", {"start": v(-12.07, -28.8) * mm, "end": v(-11.99, -28.73) * mm});
            skLineSegment(sketch, "E2052", {"start": v(-11.99, -28.73) * mm, "end": v(-11.9, -28.66) * mm});
            skLineSegment(sketch, "E2053", {"start": v(-11.9, -28.66) * mm, "end": v(-11.76, -28.6) * mm});
            skLineSegment(sketch, "E2054", {"start": v(-11.76, -28.6) * mm, "end": v(-11.62, -28.59) * mm});
            skLineSegment(sketch, "E2055", {"start": v(-11.62, -28.59) * mm, "end": v(-11.48, -28.6) * mm});
            skLineSegment(sketch, "E2056", {"start": v(-11.48, -28.6) * mm, "end": v(-11.34, -28.64) * mm});
            skLineSegment(sketch, "E2057", {"start": v(-11.34, -28.64) * mm, "end": v(-11.2, -28.7) * mm});
            skLineSegment(sketch, "E2058", {"start": v(-11.2, -28.7) * mm, "end": v(-11.1, -28.8) * mm});
            skLineSegment(sketch, "E2059", {"start": v(-11.1, -28.8) * mm, "end": v(-11, -28.9) * mm});
            skLineSegment(sketch, "E2060", {"start": v(-11, -28.9) * mm, "end": v(-10.95, -29.04) * mm});
            skLineSegment(sketch, "E2061", {"start": v(-10.95, -29.04) * mm, "end": v(-10.92, -29.15) * mm});
            skLineSegment(sketch, "E2062", {"start": v(-10.92, -29.15) * mm, "end": v(-10.92, -29.26) * mm});
            skLineSegment(sketch, "E2063", {"start": v(-10.92, -29.26) * mm, "end": v(-10.92, -29.37) * mm});
            skLineSegment(sketch, "E2064", {"start": v(-10.92, -29.37) * mm, "end": v(-10.94, -29.48) * mm});
            skLineSegment(sketch, "E2065", {"start": v(-10.94, -29.48) * mm, "end": v(-10.92, -29.58) * mm});
            skLineSegment(sketch, "E2066", {"start": v(-10.92, -29.58) * mm, "end": v(-10.83, -29.66) * mm});
            skLineSegment(sketch, "E2067", {"start": v(-10.83, -29.66) * mm, "end": v(-10.7, -29.71) * mm});
            skLineSegment(sketch, "E2068", {"start": v(-10.7, -29.71) * mm, "end": v(-10.56, -29.76) * mm});
            skLineSegment(sketch, "E2069", {"start": v(-10.56, -29.76) * mm, "end": v(-10.44, -29.76) * mm});
            skLineSegment(sketch, "E2070", {"start": v(-10.44, -29.76) * mm, "end": v(-10.36, -29.69) * mm});
            skLineSegment(sketch, "E2071", {"start": v(-10.36, -29.69) * mm, "end": v(-10.3, -29.6) * mm});
            skLineSegment(sketch, "E2072", {"start": v(-10.3, -29.6) * mm, "end": v(-10.24, -29.5) * mm});
            skLineSegment(sketch, "E2073", {"start": v(-10.24, -29.5) * mm, "end": v(-10.16, -29.42) * mm});
            skLineSegment(sketch, "E2074", {"start": v(-10.16, -29.42) * mm, "end": v(-10.07, -29.35) * mm});
            skLineSegment(sketch, "E2075", {"start": v(-10.07, -29.35) * mm, "end": v(-9.94, -29.29) * mm});
            skLineSegment(sketch, "E2076", {"start": v(-9.94, -29.29) * mm, "end": v(-9.8, -29.26) * mm});
            skLineSegment(sketch, "E2077", {"start": v(-9.8, -29.26) * mm, "end": v(-9.66, -29.26) * mm});
            skLineSegment(sketch, "E2078", {"start": v(-9.66, -29.26) * mm, "end": v(-9.52, -29.3) * mm});
            skLineSegment(sketch, "E2079", {"start": v(-9.52, -29.3) * mm, "end": v(-9.39, -29.35) * mm});
            skLineSegment(sketch, "E2080", {"start": v(-9.39, -29.35) * mm, "end": v(-9.27, -29.44) * mm});
            skLineSegment(sketch, "E2081", {"start": v(-9.27, -29.44) * mm, "end": v(-9.17, -29.54) * mm});
            skLineSegment(sketch, "E2082", {"start": v(-9.17, -29.54) * mm, "end": v(-9.1, -29.67) * mm});
            skLineSegment(sketch, "E2083", {"start": v(-9.1, -29.67) * mm, "end": v(-9.07, -29.78) * mm});
            skLineSegment(sketch, "E2084", {"start": v(-9.07, -29.78) * mm, "end": v(-9.06, -29.89) * mm});
            skLineSegment(sketch, "E2085", {"start": v(-9.06, -29.89) * mm, "end": v(-9.06, -30) * mm});
            skLineSegment(sketch, "E2086", {"start": v(-9.06, -30) * mm, "end": v(-9.07, -30.1) * mm});
            skLineSegment(sketch, "E2087", {"start": v(-9.07, -30.1) * mm, "end": v(-9.04, -30.21) * mm});
            skLineSegment(sketch, "E2088", {"start": v(-9.04, -30.21) * mm, "end": v(-8.95, -30.28) * mm});
            skLineSegment(sketch, "E2089", {"start": v(-8.95, -30.28) * mm, "end": v(-8.8, -30.32) * mm});
            skLineSegment(sketch, "E2090", {"start": v(-8.8, -30.32) * mm, "end": v(-8.67, -30.36) * mm});
            skLineSegment(sketch, "E2091", {"start": v(-8.67, -30.36) * mm, "end": v(-8.55, -30.36) * mm});
            skLineSegment(sketch, "E2092", {"start": v(-8.55, -30.36) * mm, "end": v(-8.47, -30.28) * mm});
            skLineSegment(sketch, "E2093", {"start": v(-8.47, -30.28) * mm, "end": v(-8.43, -30.18) * mm});
            skLineSegment(sketch, "E2094", {"start": v(-8.43, -30.18) * mm, "end": v(-8.37, -30.09) * mm});
            skLineSegment(sketch, "E2095", {"start": v(-8.37, -30.09) * mm, "end": v(-8.3, -30) * mm});
            skLineSegment(sketch, "E2096", {"start": v(-8.3, -30) * mm, "end": v(-8.21, -29.92) * mm});
            skLineSegment(sketch, "E2097", {"start": v(-8.21, -29.92) * mm, "end": v(-8.09, -29.86) * mm});
            skLineSegment(sketch, "E2098", {"start": v(-8.09, -29.86) * mm, "end": v(-7.95, -29.82) * mm});
            skLineSegment(sketch, "E2099", {"start": v(-7.95, -29.82) * mm, "end": v(-7.8, -29.81) * mm});
            skLineSegment(sketch, "E2100", {"start": v(-7.8, -29.81) * mm, "end": v(-7.66, -29.83) * mm});
            skLineSegment(sketch, "E2101", {"start": v(-7.66, -29.83) * mm, "end": v(-7.52, -29.88) * mm});
            skLineSegment(sketch, "E2102", {"start": v(-7.52, -29.88) * mm, "end": v(-7.4, -29.96) * mm});
            skLineSegment(sketch, "E2103", {"start": v(-7.4, -29.96) * mm, "end": v(-7.3, -30.06) * mm});
            skLineSegment(sketch, "E2104", {"start": v(-7.3, -30.06) * mm, "end": v(-7.22, -30.18) * mm});
            skLineSegment(sketch, "E2105", {"start": v(-7.22, -30.18) * mm, "end": v(-7.19, -30.29) * mm});
            skLineSegment(sketch, "E2106", {"start": v(-7.19, -30.29) * mm, "end": v(-7.16, -30.4) * mm});
            skLineSegment(sketch, "E2107", {"start": v(-7.16, -30.4) * mm, "end": v(-7.16, -30.5) * mm});
            skLineSegment(sketch, "E2108", {"start": v(-7.16, -30.5) * mm, "end": v(-7.16, -30.62) * mm});
            skLineSegment(sketch, "E2109", {"start": v(-7.16, -30.62) * mm, "end": v(-7.13, -30.72) * mm});
            skLineSegment(sketch, "E2110", {"start": v(-7.13, -30.72) * mm, "end": v(-7.03, -30.78) * mm});
            skLineSegment(sketch, "E2111", {"start": v(-7.03, -30.78) * mm, "end": v(-6.89, -30.82) * mm});
            skLineSegment(sketch, "E2112", {"start": v(-6.89, -30.82) * mm, "end": v(-6.74, -30.85) * mm});
            skLineSegment(sketch, "E2113", {"start": v(-6.74, -30.85) * mm, "end": v(-6.63, -30.83) * mm});
            skLineSegment(sketch, "E2114", {"start": v(-6.63, -30.83) * mm, "end": v(-6.56, -30.75) * mm});
            skLineSegment(sketch, "E2115", {"start": v(-6.56, -30.75) * mm, "end": v(-6.51, -30.65) * mm});
            skLineSegment(sketch, "E2116", {"start": v(-6.51, -30.65) * mm, "end": v(-6.46, -30.55) * mm});
            skLineSegment(sketch, "E2117", {"start": v(-6.46, -30.55) * mm, "end": v(-6.4, -30.46) * mm});
            skLineSegment(sketch, "E2118", {"start": v(-6.4, -30.46) * mm, "end": v(-6.32, -30.38) * mm});
            skLineSegment(sketch, "E2119", {"start": v(-6.32, -30.38) * mm, "end": v(-6.2, -30.3) * mm});
            skLineSegment(sketch, "E2120", {"start": v(-6.2, -30.3) * mm, "end": v(-6.06, -30.26) * mm});
            skLineSegment(sketch, "E2121", {"start": v(-6.06, -30.26) * mm, "end": v(-5.92, -30.24) * mm});
            skLineSegment(sketch, "E2122", {"start": v(-5.92, -30.24) * mm, "end": v(-5.77, -30.26) * mm});
            skLineSegment(sketch, "E2123", {"start": v(-5.77, -30.26) * mm, "end": v(-5.63, -30.3) * mm});
            skLineSegment(sketch, "E2124", {"start": v(-5.63, -30.3) * mm, "end": v(-5.5, -30.36) * mm});
            skLineSegment(sketch, "E2125", {"start": v(-5.5, -30.36) * mm, "end": v(-5.4, -30.46) * mm});
            skLineSegment(sketch, "E2126", {"start": v(-5.4, -30.46) * mm, "end": v(-5.31, -30.57) * mm});
            skLineSegment(sketch, "E2127", {"start": v(-5.31, -30.57) * mm, "end": v(-5.27, -30.68) * mm});
            skLineSegment(sketch, "E2128", {"start": v(-5.27, -30.68) * mm, "end": v(-5.24, -30.79) * mm});
            skLineSegment(sketch, "E2129", {"start": v(-5.24, -30.79) * mm, "end": v(-5.23, -30.9) * mm});
            skLineSegment(sketch, "E2130", {"start": v(-5.23, -30.9) * mm, "end": v(-5.22, -31) * mm});
            skLineSegment(sketch, "E2131", {"start": v(-5.22, -31) * mm, "end": v(-5.19, -31.1) * mm});
            skLineSegment(sketch, "E2132", {"start": v(-5.19, -31.1) * mm, "end": v(-5.08, -31.16) * mm});
            skLineSegment(sketch, "E2133", {"start": v(-5.08, -31.16) * mm, "end": v(-4.94, -31.19) * mm});
            skLineSegment(sketch, "E2134", {"start": v(-4.94, -31.19) * mm, "end": v(-4.8, -31.21) * mm});
            skLineSegment(sketch, "E2135", {"start": v(-4.8, -31.21) * mm, "end": v(-4.68, -31.19) * mm});
            skLineSegment(sketch, "E2136", {"start": v(-4.68, -31.19) * mm, "end": v(-4.61, -31.1) * mm});
            skLineSegment(sketch, "E2137", {"start": v(-4.61, -31.1) * mm, "end": v(-4.58, -31) * mm});
            skLineSegment(sketch, "E2138", {"start": v(-4.58, -31) * mm, "end": v(-4.53, -30.9) * mm});
            skLineSegment(sketch, "E2139", {"start": v(-4.53, -30.9) * mm, "end": v(-4.47, -30.8) * mm});
            skLineSegment(sketch, "E2140", {"start": v(-4.47, -30.8) * mm, "end": v(-4.4, -30.72) * mm});
            skLineSegment(sketch, "E2141", {"start": v(-4.4, -30.72) * mm, "end": v(-4.28, -30.63) * mm});
            skLineSegment(sketch, "E2142", {"start": v(-4.28, -30.63) * mm, "end": v(-4.15, -30.58) * mm});
            skLineSegment(sketch, "E2143", {"start": v(-4.15, -30.58) * mm, "end": v(-4, -30.55) * mm});
            skLineSegment(sketch, "E2144", {"start": v(-4, -30.55) * mm, "end": v(-3.86, -30.56) * mm});
            skLineSegment(sketch, "E2145", {"start": v(-3.86, -30.56) * mm, "end": v(-3.72, -30.6) * mm});
            skLineSegment(sketch, "E2146", {"start": v(-3.72, -30.6) * mm, "end": v(-3.59, -30.65) * mm});
            skLineSegment(sketch, "E2147", {"start": v(-3.59, -30.65) * mm, "end": v(-3.47, -30.74) * mm});
            skLineSegment(sketch, "E2148", {"start": v(-3.47, -30.74) * mm, "end": v(-3.38, -30.85) * mm});
            skLineSegment(sketch, "E2149", {"start": v(-3.38, -30.85) * mm, "end": v(-3.33, -30.95) * mm});
            skLineSegment(sketch, "E2150", {"start": v(-3.33, -30.95) * mm, "end": v(-3.3, -31.05) * mm});
            skLineSegment(sketch, "E2151", {"start": v(-3.3, -31.05) * mm, "end": v(-3.28, -31.16) * mm});
            skLineSegment(sketch, "E2152", {"start": v(-3.28, -31.16) * mm, "end": v(-3.27, -31.27) * mm});
            skLineSegment(sketch, "E2153", {"start": v(-3.27, -31.27) * mm, "end": v(-3.22, -31.37) * mm});
            skLineSegment(sketch, "E2154", {"start": v(-3.22, -31.37) * mm, "end": v(-3.12, -31.42) * mm});
            skLineSegment(sketch, "E2155", {"start": v(-3.12, -31.42) * mm, "end": v(-2.97, -31.44) * mm});
            skLineSegment(sketch, "E2156", {"start": v(-2.97, -31.44) * mm, "end": v(-2.83, -31.45) * mm});
            skLineSegment(sketch, "E2157", {"start": v(-2.83, -31.45) * mm, "end": v(-2.71, -31.42) * mm});
            skLineSegment(sketch, "E2158", {"start": v(-2.71, -31.42) * mm, "end": v(-2.65, -31.33) * mm});
            skLineSegment(sketch, "E2159", {"start": v(-2.65, -31.33) * mm, "end": v(-2.62, -31.22) * mm});
            skLineSegment(sketch, "E2160", {"start": v(-2.62, -31.22) * mm, "end": v(-2.58, -31.12) * mm});
            skLineSegment(sketch, "E2161", {"start": v(-2.58, -31.12) * mm, "end": v(-2.53, -31.02) * mm});
            skLineSegment(sketch, "E2162", {"start": v(-2.53, -31.02) * mm, "end": v(-2.46, -30.93) * mm});
            skLineSegment(sketch, "E2163", {"start": v(-2.46, -30.93) * mm, "end": v(-2.35, -30.84) * mm});
            skLineSegment(sketch, "E2164", {"start": v(-2.35, -30.84) * mm, "end": v(-2.22, -30.78) * mm});
            skLineSegment(sketch, "E2165", {"start": v(-2.22, -30.78) * mm, "end": v(-2.08, -30.75) * mm});
            skLineSegment(sketch, "E2166", {"start": v(-2.08, -30.75) * mm, "end": v(-1.93, -30.74) * mm});
            skLineSegment(sketch, "E2167", {"start": v(-1.93, -30.74) * mm, "end": v(-1.8, -30.76) * mm});
            skLineSegment(sketch, "E2168", {"start": v(-1.8, -30.76) * mm, "end": v(-1.66, -30.82) * mm});
            skLineSegment(sketch, "E2169", {"start": v(-1.66, -30.82) * mm, "end": v(-1.54, -30.9) * mm});
            skLineSegment(sketch, "E2170", {"start": v(-1.54, -30.9) * mm, "end": v(-1.44, -31) * mm});
            skLineSegment(sketch, "E2171", {"start": v(-1.44, -31) * mm, "end": v(-1.38, -31.1) * mm});
            skLineSegment(sketch, "E2172", {"start": v(-1.38, -31.1) * mm, "end": v(-1.34, -31.2) * mm});
            skLineSegment(sketch, "E2173", {"start": v(-1.34, -31.2) * mm, "end": v(-1.31, -31.3) * mm});
            skLineSegment(sketch, "E2174", {"start": v(-1.31, -31.3) * mm, "end": v(-1.3, -31.42) * mm});
            skLineSegment(sketch, "E2175", {"start": v(-1.3, -31.42) * mm, "end": v(-1.25, -31.51) * mm});
            skLineSegment(sketch, "E2176", {"start": v(-1.25, -31.51) * mm, "end": v(-1.14, -31.56) * mm});
            skLineSegment(sketch, "E2177", {"start": v(-1.14, -31.56) * mm, "end": v(-1, -31.56) * mm});
            skLineSegment(sketch, "E2178", {"start": v(-1, -31.56) * mm, "end": v(-0.84, -31.56) * mm});
            skLineSegment(sketch, "E2179", {"start": v(-0.84, -31.56) * mm, "end": v(-0.73, -31.53) * mm});
            skLineSegment(sketch, "E2180", {"start": v(-0.73, -31.53) * mm, "end": v(-0.68, -31.44) * mm});
            skLineSegment(sketch, "E2181", {"start": v(-0.68, -31.44) * mm, "end": v(-0.66, -31.33) * mm});
            skLineSegment(sketch, "E2182", {"start": v(-0.66, -31.33) * mm, "end": v(-0.62, -31.22) * mm});
            skLineSegment(sketch, "E2183", {"start": v(-0.62, -31.22) * mm, "end": v(-0.57, -31.12) * mm});
            skLineSegment(sketch, "E2184", {"start": v(-0.57, -31.12) * mm, "end": v(-0.51, -31.03) * mm});
            skLineSegment(sketch, "E2185", {"start": v(-0.51, -31.03) * mm, "end": v(-0.4, -30.93) * mm});
            skLineSegment(sketch, "E2186", {"start": v(-0.4, -30.93) * mm, "end": v(-0.28, -30.86) * mm});
            skLineSegment(sketch, "E2187", {"start": v(-0.28, -30.86) * mm, "end": v(-0.14, -30.82) * mm});
            skLineSegment(sketch, "E2188", {"start": v(-0.14, -30.82) * mm, "end": v(0, -30.8) * mm});
            skLineSegment(sketch, "E2189", {"start": v(0, -30.8) * mm, "end": v(0.14, -30.82) * mm});
            skLineSegment(sketch, "E2190", {"start": v(0.14, -30.82) * mm, "end": v(0.28, -30.86) * mm});
            skLineSegment(sketch, "E2191", {"start": v(0.28, -30.86) * mm, "end": v(0.4, -30.93) * mm});
            skLineSegment(sketch, "E2192", {"start": v(0.4, -30.93) * mm, "end": v(0.51, -31.03) * mm});
            skLineSegment(sketch, "E2193", {"start": v(0.51, -31.03) * mm, "end": v(0.57, -31.12) * mm});
            skLineSegment(sketch, "E2194", {"start": v(0.57, -31.12) * mm, "end": v(0.62, -31.22) * mm});
            skLineSegment(sketch, "E2195", {"start": v(0.62, -31.22) * mm, "end": v(0.66, -31.33) * mm});
            skLineSegment(sketch, "E2196", {"start": v(0.66, -31.33) * mm, "end": v(0.68, -31.44) * mm});
            skLineSegment(sketch, "E2197", {"start": v(0.68, -31.44) * mm, "end": v(0.73, -31.53) * mm});
            skLineSegment(sketch, "E2198", {"start": v(0.73, -31.53) * mm, "end": v(0.84, -31.56) * mm});
            skLineSegment(sketch, "E2199", {"start": v(0.84, -31.56) * mm, "end": v(1, -31.56) * mm});
            skLineSegment(sketch, "E2200", {"start": v(-0.8, -2.47) * mm, "end": v(-1.53, -2.1) * mm});
            skLineSegment(sketch, "E2201", {"start": v(-1.53, -2.1) * mm, "end": v(-2.1, -1.53) * mm});
            skLineSegment(sketch, "E2202", {"start": v(-2.1, -1.53) * mm, "end": v(-2.47, -0.8) * mm});
            skLineSegment(sketch, "E2203", {"start": v(-2.47, -0.8) * mm, "end": v(-2.6, 0) * mm});
            skLineSegment(sketch, "E2204", {"start": v(-2.6, 0) * mm, "end": v(-2.47, 0.8) * mm});
            skLineSegment(sketch, "E2205", {"start": v(-2.47, 0.8) * mm, "end": v(-2.1, 1.53) * mm});
            skLineSegment(sketch, "E2206", {"start": v(-2.1, 1.53) * mm, "end": v(-1.53, 2.1) * mm});
            skLineSegment(sketch, "E2207", {"start": v(-1.53, 2.1) * mm, "end": v(-0.8, 2.47) * mm});
            skLineSegment(sketch, "E2208", {"start": v(-0.8, 2.47) * mm, "end": v(0, 2.6) * mm});
            skLineSegment(sketch, "E2209", {"start": v(0, 2.6) * mm, "end": v(0.8, 2.47) * mm});
            skLineSegment(sketch, "E2210", {"start": v(0.8, 2.47) * mm, "end": v(1.53, 2.1) * mm});
            skLineSegment(sketch, "E2211", {"start": v(1.53, 2.1) * mm, "end": v(2.1, 1.53) * mm});
            skLineSegment(sketch, "E2212", {"start": v(2.1, 1.53) * mm, "end": v(2.47, 0.8) * mm});
            skLineSegment(sketch, "E2213", {"start": v(2.47, 0.8) * mm, "end": v(2.6, 0) * mm});
            skLineSegment(sketch, "E2214", {"start": v(2.6, 0) * mm, "end": v(2.47, -0.8) * mm});
            skLineSegment(sketch, "E2215", {"start": v(2.47, -0.8) * mm, "end": v(2.1, -1.53) * mm});
            skLineSegment(sketch, "E2216", {"start": v(2.1, -1.53) * mm, "end": v(1.53, -2.1) * mm});
            skLineSegment(sketch, "E2217", {"start": v(1.53, -2.1) * mm, "end": v(0.8, -2.47) * mm});
            skLineSegment(sketch, "E2218", {"start": v(0.8, -2.47) * mm, "end": v(0, -2.6) * mm});
            skLineSegment(sketch, "E2219", {"start": v(0, -2.6) * mm, "end": v(-0.8, -2.47) * mm});
            skSolve(sketch);
        }
        {
            var Q0;
            Q0=makeQuery(id+"F1.imprint","IMPRINT",FACE,{"disambiguationData":[TD([[makeQuery(id+"F1.imprint","IMPRINT",EDGE,{"derivedFrom":sQuery(id+"F1.wireOp",EDGE,"E0")}),1.0]])]});
            extrude(context, id + "F2", {"entities" : qUnion([Q0]), "endBound" : BoundingType.SYMMETRIC, "depth" : getVariable(context, 'thMat'), "offsetDistance" : 25 * mm});
        }
    });
